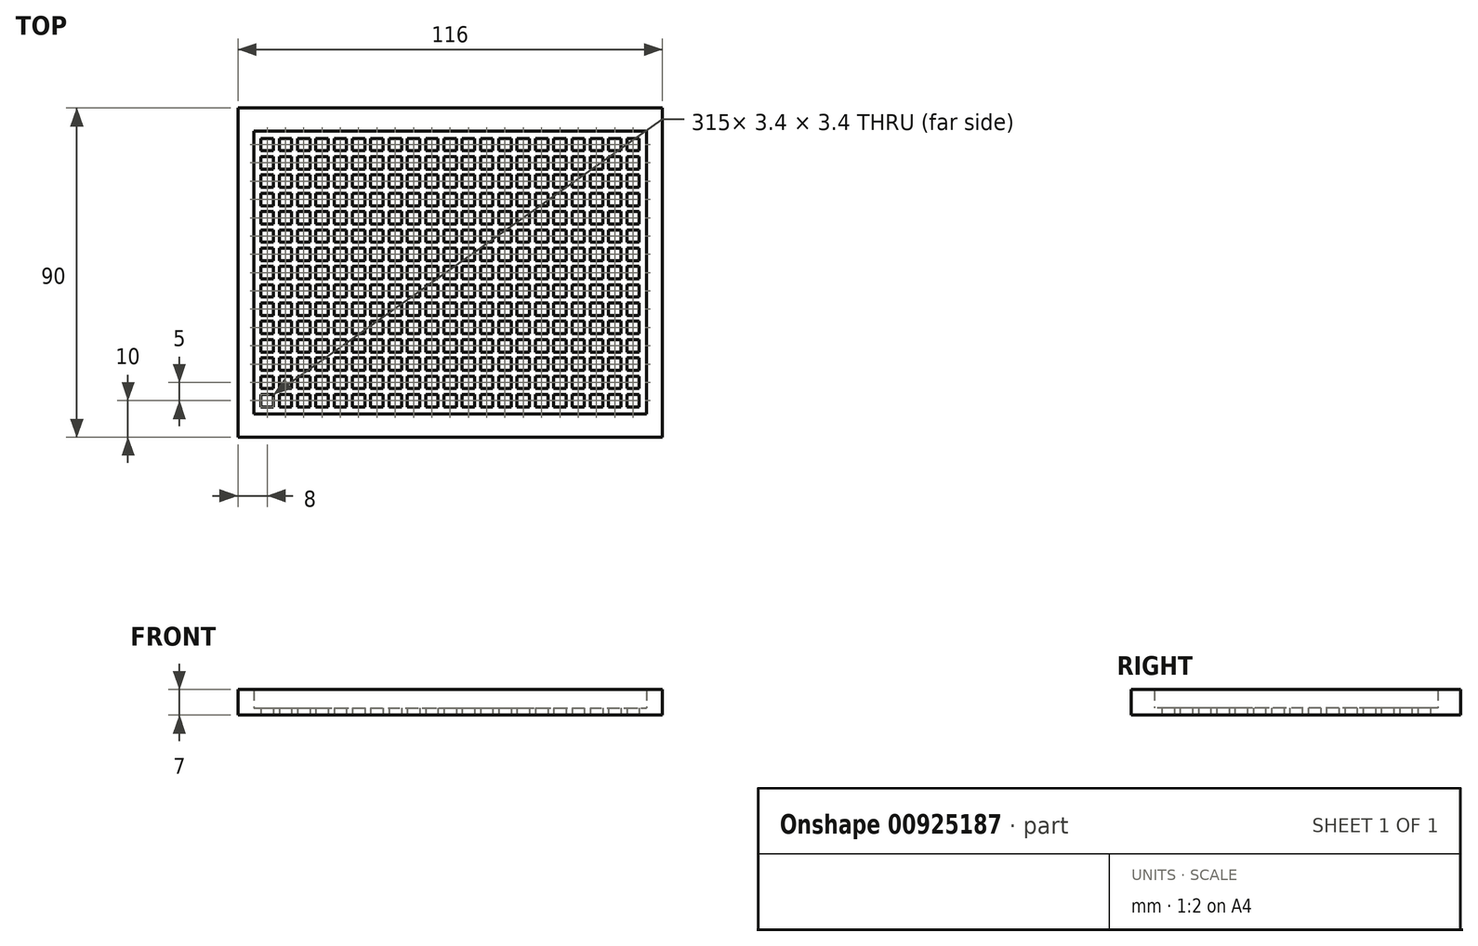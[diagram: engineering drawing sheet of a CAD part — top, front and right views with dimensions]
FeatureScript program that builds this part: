
annotation { "Feature Type Name" : "Feature", "Feature Type Description" : "" }
export const myFeature = defineFeature(function(context is Context, id is Id, definition is map)
    precondition{}
    {
        {
            var Q0;
            Q0=qCreatedBy(makeId("Top.planeOp"),FACE);
            var sketch = newSketch(context, id + "F0", { "sketchPlane" : qUnion([Q0])});
            skLineSegment(sketch, "E0.bottom", {"start": v(-58, 45) * mm, "end": v(58, 45) * mm});
            skLineSegment(sketch, "E0.top", {"start": v(-58, -45) * mm, "end": v(58, -45) * mm});
            skLineSegment(sketch, "E0.left", {"start": v(-58, 45) * mm, "end": v(-58, -45) * mm});
            skLineSegment(sketch, "E0.right", {"start": v(58, 45) * mm, "end": v(58, -45) * mm});
            skLineSegment(sketch, "E1.10.0.0", {"start": v(48.3, 1.7) * mm, "end": v(51.7, 1.7) * mm});
            skLineSegment(sketch, "E1.10.0.1", {"start": v(51.7, 1.7) * mm, "end": v(51.7, -1.7) * mm});
            skLineSegment(sketch, "E1.10.0.2", {"start": v(48.3, -1.7) * mm, "end": v(51.7, -1.7) * mm});
            skLineSegment(sketch, "E1.10.0.3", {"start": v(48.3, 1.7) * mm, "end": v(48.3, -1.7) * mm});
            skLineSegment(sketch, "E1.10.1.0", {"start": v(48.3, 6.7) * mm, "end": v(51.7, 6.7) * mm});
            skLineSegment(sketch, "E1.10.1.1", {"start": v(51.7, 6.7) * mm, "end": v(51.7, 3.3) * mm});
            skLineSegment(sketch, "E1.10.1.2", {"start": v(48.3, 3.3) * mm, "end": v(51.7, 3.3) * mm});
            skLineSegment(sketch, "E1.10.1.3", {"start": v(48.3, 6.7) * mm, "end": v(48.3, 3.3) * mm});
            skLineSegment(sketch, "E1.10.2.0", {"start": v(48.3, 11.7) * mm, "end": v(51.7, 11.7) * mm});
            skLineSegment(sketch, "E1.10.2.1", {"start": v(51.7, 11.7) * mm, "end": v(51.7, 8.3) * mm});
            skLineSegment(sketch, "E1.10.2.2", {"start": v(48.3, 8.3) * mm, "end": v(51.7, 8.3) * mm});
            skLineSegment(sketch, "E1.10.2.3", {"start": v(48.3, 11.7) * mm, "end": v(48.3, 8.3) * mm});
            skLineSegment(sketch, "E1.10.3.0", {"start": v(48.3, 16.7) * mm, "end": v(51.7, 16.7) * mm});
            skLineSegment(sketch, "E1.10.3.1", {"start": v(51.7, 16.7) * mm, "end": v(51.7, 13.3) * mm});
            skLineSegment(sketch, "E1.10.3.2", {"start": v(48.3, 13.3) * mm, "end": v(51.7, 13.3) * mm});
            skLineSegment(sketch, "E1.10.3.3", {"start": v(48.3, 16.7) * mm, "end": v(48.3, 13.3) * mm});
            skLineSegment(sketch, "E1.10.4.0", {"start": v(48.3, 21.7) * mm, "end": v(51.7, 21.7) * mm});
            skLineSegment(sketch, "E1.10.4.1", {"start": v(51.7, 21.7) * mm, "end": v(51.7, 18.3) * mm});
            skLineSegment(sketch, "E1.10.4.2", {"start": v(48.3, 18.3) * mm, "end": v(51.7, 18.3) * mm});
            skLineSegment(sketch, "E1.10.4.3", {"start": v(48.3, 21.7) * mm, "end": v(48.3, 18.3) * mm});
            skLineSegment(sketch, "E1.10.5.0", {"start": v(48.3, 26.7) * mm, "end": v(51.7, 26.7) * mm});
            skLineSegment(sketch, "E1.10.5.1", {"start": v(51.7, 26.7) * mm, "end": v(51.7, 23.3) * mm});
            skLineSegment(sketch, "E1.10.5.2", {"start": v(48.3, 23.3) * mm, "end": v(51.7, 23.3) * mm});
            skLineSegment(sketch, "E1.10.5.3", {"start": v(48.3, 26.7) * mm, "end": v(48.3, 23.3) * mm});
            skLineSegment(sketch, "E1.10.6.0", {"start": v(48.3, 31.7) * mm, "end": v(51.7, 31.7) * mm});
            skLineSegment(sketch, "E1.10.6.1", {"start": v(51.7, 31.7) * mm, "end": v(51.7, 28.3) * mm});
            skLineSegment(sketch, "E1.10.6.2", {"start": v(48.3, 28.3) * mm, "end": v(51.7, 28.3) * mm});
            skLineSegment(sketch, "E1.10.6.3", {"start": v(48.3, 31.7) * mm, "end": v(48.3, 28.3) * mm});
            skLineSegment(sketch, "E1.10.7.0", {"start": v(48.3, 36.7) * mm, "end": v(51.7, 36.7) * mm});
            skLineSegment(sketch, "E1.10.7.1", {"start": v(51.7, 36.7) * mm, "end": v(51.7, 33.3) * mm});
            skLineSegment(sketch, "E1.10.7.2", {"start": v(48.3, 33.3) * mm, "end": v(51.7, 33.3) * mm});
            skLineSegment(sketch, "E1.10.7.3", {"start": v(48.3, 36.7) * mm, "end": v(48.3, 33.3) * mm});
            skLineSegment(sketch, "E2.0.1.4", {"start": v(48.3, -3.3) * mm, "end": v(51.7, -3.3) * mm});
            skLineSegment(sketch, "E2.0.1.13", {"start": v(48.3, -3.3) * mm, "end": v(48.3, -6.7) * mm});
            skLineSegment(sketch, "E2.0.1.19", {"start": v(51.7, -3.3) * mm, "end": v(51.7, -6.7) * mm});
            skLineSegment(sketch, "E2.0.1.21", {"start": v(48.3, -6.7) * mm, "end": v(51.7, -6.7) * mm});
            skLineSegment(sketch, "E2.0.2.4", {"start": v(48.3, -8.3) * mm, "end": v(51.7, -8.3) * mm});
            skLineSegment(sketch, "E2.0.2.13", {"start": v(48.3, -8.3) * mm, "end": v(48.3, -11.7) * mm});
            skLineSegment(sketch, "E2.0.2.19", {"start": v(51.7, -8.3) * mm, "end": v(51.7, -11.7) * mm});
            skLineSegment(sketch, "E2.0.2.21", {"start": v(48.3, -11.7) * mm, "end": v(51.7, -11.7) * mm});
            skLineSegment(sketch, "E2.0.3.4", {"start": v(48.3, -13.3) * mm, "end": v(51.7, -13.3) * mm});
            skLineSegment(sketch, "E2.0.3.13", {"start": v(48.3, -13.3) * mm, "end": v(48.3, -16.7) * mm});
            skLineSegment(sketch, "E2.0.3.19", {"start": v(51.7, -13.3) * mm, "end": v(51.7, -16.7) * mm});
            skLineSegment(sketch, "E2.0.3.21", {"start": v(48.3, -16.7) * mm, "end": v(51.7, -16.7) * mm});
            skLineSegment(sketch, "E2.0.4.4", {"start": v(48.3, -18.3) * mm, "end": v(51.7, -18.3) * mm});
            skLineSegment(sketch, "E2.0.4.13", {"start": v(48.3, -18.3) * mm, "end": v(48.3, -21.7) * mm});
            skLineSegment(sketch, "E2.0.4.19", {"start": v(51.7, -18.3) * mm, "end": v(51.7, -21.7) * mm});
            skLineSegment(sketch, "E2.0.4.21", {"start": v(48.3, -21.7) * mm, "end": v(51.7, -21.7) * mm});
            skLineSegment(sketch, "E2.0.5.4", {"start": v(48.3, -23.3) * mm, "end": v(51.7, -23.3) * mm});
            skLineSegment(sketch, "E2.0.5.13", {"start": v(48.3, -23.3) * mm, "end": v(48.3, -26.7) * mm});
            skLineSegment(sketch, "E2.0.5.19", {"start": v(51.7, -23.3) * mm, "end": v(51.7, -26.7) * mm});
            skLineSegment(sketch, "E2.0.5.21", {"start": v(48.3, -26.7) * mm, "end": v(51.7, -26.7) * mm});
            skLineSegment(sketch, "E2.0.6.4", {"start": v(48.3, -28.3) * mm, "end": v(51.7, -28.3) * mm});
            skLineSegment(sketch, "E2.0.6.13", {"start": v(48.3, -28.3) * mm, "end": v(48.3, -31.7) * mm});
            skLineSegment(sketch, "E2.0.6.19", {"start": v(51.7, -28.3) * mm, "end": v(51.7, -31.7) * mm});
            skLineSegment(sketch, "E2.0.6.21", {"start": v(48.3, -31.7) * mm, "end": v(51.7, -31.7) * mm});
            skLineSegment(sketch, "E2.0.7.4", {"start": v(48.3, -33.3) * mm, "end": v(51.7, -33.3) * mm});
            skLineSegment(sketch, "E2.0.7.13", {"start": v(48.3, -33.3) * mm, "end": v(48.3, -36.7) * mm});
            skLineSegment(sketch, "E2.0.7.19", {"start": v(51.7, -33.3) * mm, "end": v(51.7, -36.7) * mm});
            skLineSegment(sketch, "E2.0.7.21", {"start": v(48.3, -36.7) * mm, "end": v(51.7, -36.7) * mm});
            skLineSegment(sketch, "E3.1.0.0", {"start": v(43.3, 36.7) * mm, "end": v(43.3, 33.3) * mm});
            skLineSegment(sketch, "E3.1.0.1", {"start": v(43.3, -21.7) * mm, "end": v(46.7, -21.7) * mm});
            skLineSegment(sketch, "E3.1.0.2", {"start": v(43.3, -3.3) * mm, "end": v(43.3, -6.7) * mm});
            skLineSegment(sketch, "E3.1.0.3", {"start": v(43.3, 8.3) * mm, "end": v(46.7, 8.3) * mm});
            skLineSegment(sketch, "E3.1.0.4", {"start": v(43.3, -33.3) * mm, "end": v(46.7, -33.3) * mm});
            skLineSegment(sketch, "E3.1.0.5", {"start": v(43.3, 31.7) * mm, "end": v(43.3, 28.3) * mm});
            skLineSegment(sketch, "E3.1.0.6", {"start": v(43.3, 1.7) * mm, "end": v(43.3, -1.7) * mm});
            skLineSegment(sketch, "E3.1.0.7", {"start": v(43.3, -18.3) * mm, "end": v(43.3, -21.7) * mm});
            skLineSegment(sketch, "E3.1.0.8", {"start": v(46.7, -33.3) * mm, "end": v(46.7, -36.7) * mm});
            skLineSegment(sketch, "E3.1.0.9", {"start": v(43.3, 16.7) * mm, "end": v(43.3, 13.3) * mm});
            skLineSegment(sketch, "E3.1.0.10", {"start": v(43.3, -8.3) * mm, "end": v(43.3, -11.7) * mm});
            skLineSegment(sketch, "E3.1.0.11", {"start": v(43.3, -36.7) * mm, "end": v(46.7, -36.7) * mm});
            skLineSegment(sketch, "E3.1.0.12", {"start": v(46.7, 26.7) * mm, "end": v(46.7, 23.3) * mm});
            skLineSegment(sketch, "E3.1.0.13", {"start": v(46.7, -28.3) * mm, "end": v(46.7, -31.7) * mm});
            skLineSegment(sketch, "E3.1.0.14", {"start": v(43.3, 23.3) * mm, "end": v(46.7, 23.3) * mm});
            skLineSegment(sketch, "E3.1.0.15", {"start": v(46.7, 6.7) * mm, "end": v(46.7, 3.3) * mm});
            skLineSegment(sketch, "E3.1.0.16", {"start": v(43.3, -28.3) * mm, "end": v(46.7, -28.3) * mm});
            skLineSegment(sketch, "E3.1.0.17", {"start": v(43.3, 13.3) * mm, "end": v(46.7, 13.3) * mm});
            skLineSegment(sketch, "E3.1.0.18", {"start": v(43.3, 33.3) * mm, "end": v(46.7, 33.3) * mm});
            skLineSegment(sketch, "E3.1.0.19", {"start": v(43.3, 3.3) * mm, "end": v(46.7, 3.3) * mm});
            skLineSegment(sketch, "E3.1.0.20", {"start": v(46.7, -13.3) * mm, "end": v(46.7, -16.7) * mm});
            skLineSegment(sketch, "E3.1.0.21", {"start": v(46.7, 16.7) * mm, "end": v(46.7, 13.3) * mm});
            skLineSegment(sketch, "E3.1.0.22", {"start": v(43.3, -23.3) * mm, "end": v(43.3, -26.7) * mm});
            skLineSegment(sketch, "E3.1.0.23", {"start": v(43.3, -28.3) * mm, "end": v(43.3, -31.7) * mm});
            skLineSegment(sketch, "E3.1.0.24", {"start": v(43.3, -13.3) * mm, "end": v(43.3, -16.7) * mm});
            skLineSegment(sketch, "E3.1.0.25", {"start": v(43.3, -23.3) * mm, "end": v(46.7, -23.3) * mm});
            skLineSegment(sketch, "E3.1.0.26", {"start": v(43.3, 1.7) * mm, "end": v(46.7, 1.7) * mm});
            skLineSegment(sketch, "E3.1.0.27", {"start": v(46.7, -3.3) * mm, "end": v(46.7, -6.7) * mm});
            skLineSegment(sketch, "E3.1.0.28", {"start": v(43.3, 28.3) * mm, "end": v(46.7, 28.3) * mm});
            skLineSegment(sketch, "E3.1.0.29", {"start": v(43.3, 21.7) * mm, "end": v(46.7, 21.7) * mm});
            skLineSegment(sketch, "E3.1.0.30", {"start": v(43.3, -18.3) * mm, "end": v(46.7, -18.3) * mm});
            skLineSegment(sketch, "E3.1.0.31", {"start": v(43.3, -13.3) * mm, "end": v(46.7, -13.3) * mm});
            skLineSegment(sketch, "E3.1.0.32", {"start": v(46.7, 1.7) * mm, "end": v(46.7, -1.7) * mm});
            skLineSegment(sketch, "E3.1.0.33", {"start": v(46.7, 36.7) * mm, "end": v(46.7, 33.3) * mm});
            skLineSegment(sketch, "E3.1.0.34", {"start": v(43.3, 18.3) * mm, "end": v(46.7, 18.3) * mm});
            skLineSegment(sketch, "E3.1.0.35", {"start": v(46.7, -18.3) * mm, "end": v(46.7, -21.7) * mm});
            skLineSegment(sketch, "E3.1.0.36", {"start": v(43.3, -33.3) * mm, "end": v(43.3, -36.7) * mm});
            skLineSegment(sketch, "E3.1.0.37", {"start": v(43.3, -3.3) * mm, "end": v(46.7, -3.3) * mm});
            skLineSegment(sketch, "E3.1.0.38", {"start": v(46.7, 21.7) * mm, "end": v(46.7, 18.3) * mm});
            skLineSegment(sketch, "E3.1.0.39", {"start": v(46.7, -8.3) * mm, "end": v(46.7, -11.7) * mm});
            skLineSegment(sketch, "E3.1.0.40", {"start": v(43.3, -16.7) * mm, "end": v(46.7, -16.7) * mm});
            skLineSegment(sketch, "E3.1.0.41", {"start": v(43.3, -31.7) * mm, "end": v(46.7, -31.7) * mm});
            skLineSegment(sketch, "E3.1.0.42", {"start": v(46.7, 31.7) * mm, "end": v(46.7, 28.3) * mm});
            skLineSegment(sketch, "E3.1.0.43", {"start": v(43.3, 26.7) * mm, "end": v(43.3, 23.3) * mm});
            skLineSegment(sketch, "E3.1.0.44", {"start": v(43.3, -1.7) * mm, "end": v(46.7, -1.7) * mm});
            skLineSegment(sketch, "E3.1.0.45", {"start": v(43.3, -26.7) * mm, "end": v(46.7, -26.7) * mm});
            skLineSegment(sketch, "E3.1.0.46", {"start": v(43.3, -8.3) * mm, "end": v(46.7, -8.3) * mm});
            skLineSegment(sketch, "E3.1.0.47", {"start": v(46.7, 11.7) * mm, "end": v(46.7, 8.3) * mm});
            skLineSegment(sketch, "E3.1.0.48", {"start": v(43.3, 6.7) * mm, "end": v(43.3, 3.3) * mm});
            skLineSegment(sketch, "E3.1.0.49", {"start": v(43.3, 16.7) * mm, "end": v(46.7, 16.7) * mm});
            skLineSegment(sketch, "E3.1.0.50", {"start": v(43.3, -11.7) * mm, "end": v(46.7, -11.7) * mm});
            skLineSegment(sketch, "E3.1.0.51", {"start": v(43.3, 6.7) * mm, "end": v(46.7, 6.7) * mm});
            skLineSegment(sketch, "E3.1.0.52", {"start": v(43.3, 11.7) * mm, "end": v(43.3, 8.3) * mm});
            skLineSegment(sketch, "E3.1.0.53", {"start": v(43.3, 11.7) * mm, "end": v(46.7, 11.7) * mm});
            skLineSegment(sketch, "E3.1.0.54", {"start": v(43.3, 36.7) * mm, "end": v(46.7, 36.7) * mm});
            skLineSegment(sketch, "E3.1.0.55", {"start": v(46.7, -23.3) * mm, "end": v(46.7, -26.7) * mm});
            skLineSegment(sketch, "E3.1.0.56", {"start": v(43.3, 26.7) * mm, "end": v(46.7, 26.7) * mm});
            skLineSegment(sketch, "E3.1.0.57", {"start": v(43.3, 31.7) * mm, "end": v(46.7, 31.7) * mm});
            skLineSegment(sketch, "E3.1.0.58", {"start": v(43.3, 21.7) * mm, "end": v(43.3, 18.3) * mm});
            skLineSegment(sketch, "E3.1.0.59", {"start": v(43.3, -6.7) * mm, "end": v(46.7, -6.7) * mm});
            skLineSegment(sketch, "E3.2.0.0", {"start": v(38.3, 36.7) * mm, "end": v(38.3, 33.3) * mm});
            skLineSegment(sketch, "E3.2.0.1", {"start": v(38.3, -21.7) * mm, "end": v(41.7, -21.7) * mm});
            skLineSegment(sketch, "E3.2.0.2", {"start": v(38.3, -3.3) * mm, "end": v(38.3, -6.7) * mm});
            skLineSegment(sketch, "E3.2.0.3", {"start": v(38.3, 8.3) * mm, "end": v(41.7, 8.3) * mm});
            skLineSegment(sketch, "E3.2.0.4", {"start": v(38.3, -33.3) * mm, "end": v(41.7, -33.3) * mm});
            skLineSegment(sketch, "E3.2.0.5", {"start": v(38.3, 31.7) * mm, "end": v(38.3, 28.3) * mm});
            skLineSegment(sketch, "E3.2.0.6", {"start": v(38.3, 1.7) * mm, "end": v(38.3, -1.7) * mm});
            skLineSegment(sketch, "E3.2.0.7", {"start": v(38.3, -18.3) * mm, "end": v(38.3, -21.7) * mm});
            skLineSegment(sketch, "E3.2.0.8", {"start": v(41.7, -33.3) * mm, "end": v(41.7, -36.7) * mm});
            skLineSegment(sketch, "E3.2.0.9", {"start": v(38.3, 16.7) * mm, "end": v(38.3, 13.3) * mm});
            skLineSegment(sketch, "E3.2.0.10", {"start": v(38.3, -8.3) * mm, "end": v(38.3, -11.7) * mm});
            skLineSegment(sketch, "E3.2.0.11", {"start": v(38.3, -36.7) * mm, "end": v(41.7, -36.7) * mm});
            skLineSegment(sketch, "E3.2.0.12", {"start": v(41.7, 26.7) * mm, "end": v(41.7, 23.3) * mm});
            skLineSegment(sketch, "E3.2.0.13", {"start": v(41.7, -28.3) * mm, "end": v(41.7, -31.7) * mm});
            skLineSegment(sketch, "E3.2.0.14", {"start": v(38.3, 23.3) * mm, "end": v(41.7, 23.3) * mm});
            skLineSegment(sketch, "E3.2.0.15", {"start": v(41.7, 6.7) * mm, "end": v(41.7, 3.3) * mm});
            skLineSegment(sketch, "E3.2.0.16", {"start": v(38.3, -28.3) * mm, "end": v(41.7, -28.3) * mm});
            skLineSegment(sketch, "E3.2.0.17", {"start": v(38.3, 13.3) * mm, "end": v(41.7, 13.3) * mm});
            skLineSegment(sketch, "E3.2.0.18", {"start": v(38.3, 33.3) * mm, "end": v(41.7, 33.3) * mm});
            skLineSegment(sketch, "E3.2.0.19", {"start": v(38.3, 3.3) * mm, "end": v(41.7, 3.3) * mm});
            skLineSegment(sketch, "E3.2.0.20", {"start": v(41.7, -13.3) * mm, "end": v(41.7, -16.7) * mm});
            skLineSegment(sketch, "E3.2.0.21", {"start": v(41.7, 16.7) * mm, "end": v(41.7, 13.3) * mm});
            skLineSegment(sketch, "E3.2.0.22", {"start": v(38.3, -23.3) * mm, "end": v(38.3, -26.7) * mm});
            skLineSegment(sketch, "E3.2.0.23", {"start": v(38.3, -28.3) * mm, "end": v(38.3, -31.7) * mm});
            skLineSegment(sketch, "E3.2.0.24", {"start": v(38.3, -13.3) * mm, "end": v(38.3, -16.7) * mm});
            skLineSegment(sketch, "E3.2.0.25", {"start": v(38.3, -23.3) * mm, "end": v(41.7, -23.3) * mm});
            skLineSegment(sketch, "E3.2.0.26", {"start": v(38.3, 1.7) * mm, "end": v(41.7, 1.7) * mm});
            skLineSegment(sketch, "E3.2.0.27", {"start": v(41.7, -3.3) * mm, "end": v(41.7, -6.7) * mm});
            skLineSegment(sketch, "E3.2.0.28", {"start": v(38.3, 28.3) * mm, "end": v(41.7, 28.3) * mm});
            skLineSegment(sketch, "E3.2.0.29", {"start": v(38.3, 21.7) * mm, "end": v(41.7, 21.7) * mm});
            skLineSegment(sketch, "E3.2.0.30", {"start": v(38.3, -18.3) * mm, "end": v(41.7, -18.3) * mm});
            skLineSegment(sketch, "E3.2.0.31", {"start": v(38.3, -13.3) * mm, "end": v(41.7, -13.3) * mm});
            skLineSegment(sketch, "E3.2.0.32", {"start": v(41.7, 1.7) * mm, "end": v(41.7, -1.7) * mm});
            skLineSegment(sketch, "E3.2.0.33", {"start": v(41.7, 36.7) * mm, "end": v(41.7, 33.3) * mm});
            skLineSegment(sketch, "E3.2.0.34", {"start": v(38.3, 18.3) * mm, "end": v(41.7, 18.3) * mm});
            skLineSegment(sketch, "E3.2.0.35", {"start": v(41.7, -18.3) * mm, "end": v(41.7, -21.7) * mm});
            skLineSegment(sketch, "E3.2.0.36", {"start": v(38.3, -33.3) * mm, "end": v(38.3, -36.7) * mm});
            skLineSegment(sketch, "E3.2.0.37", {"start": v(38.3, -3.3) * mm, "end": v(41.7, -3.3) * mm});
            skLineSegment(sketch, "E3.2.0.38", {"start": v(41.7, 21.7) * mm, "end": v(41.7, 18.3) * mm});
            skLineSegment(sketch, "E3.2.0.39", {"start": v(41.7, -8.3) * mm, "end": v(41.7, -11.7) * mm});
            skLineSegment(sketch, "E3.2.0.40", {"start": v(38.3, -16.7) * mm, "end": v(41.7, -16.7) * mm});
            skLineSegment(sketch, "E3.2.0.41", {"start": v(38.3, -31.7) * mm, "end": v(41.7, -31.7) * mm});
            skLineSegment(sketch, "E3.2.0.42", {"start": v(41.7, 31.7) * mm, "end": v(41.7, 28.3) * mm});
            skLineSegment(sketch, "E3.2.0.43", {"start": v(38.3, 26.7) * mm, "end": v(38.3, 23.3) * mm});
            skLineSegment(sketch, "E3.2.0.44", {"start": v(38.3, -1.7) * mm, "end": v(41.7, -1.7) * mm});
            skLineSegment(sketch, "E3.2.0.45", {"start": v(38.3, -26.7) * mm, "end": v(41.7, -26.7) * mm});
            skLineSegment(sketch, "E3.2.0.46", {"start": v(38.3, -8.3) * mm, "end": v(41.7, -8.3) * mm});
            skLineSegment(sketch, "E3.2.0.47", {"start": v(41.7, 11.7) * mm, "end": v(41.7, 8.3) * mm});
            skLineSegment(sketch, "E3.2.0.48", {"start": v(38.3, 6.7) * mm, "end": v(38.3, 3.3) * mm});
            skLineSegment(sketch, "E3.2.0.49", {"start": v(38.3, 16.7) * mm, "end": v(41.7, 16.7) * mm});
            skLineSegment(sketch, "E3.2.0.50", {"start": v(38.3, -11.7) * mm, "end": v(41.7, -11.7) * mm});
            skLineSegment(sketch, "E3.2.0.51", {"start": v(38.3, 6.7) * mm, "end": v(41.7, 6.7) * mm});
            skLineSegment(sketch, "E3.2.0.52", {"start": v(38.3, 11.7) * mm, "end": v(38.3, 8.3) * mm});
            skLineSegment(sketch, "E3.2.0.53", {"start": v(38.3, 11.7) * mm, "end": v(41.7, 11.7) * mm});
            skLineSegment(sketch, "E3.2.0.54", {"start": v(38.3, 36.7) * mm, "end": v(41.7, 36.7) * mm});
            skLineSegment(sketch, "E3.2.0.55", {"start": v(41.7, -23.3) * mm, "end": v(41.7, -26.7) * mm});
            skLineSegment(sketch, "E3.2.0.56", {"start": v(38.3, 26.7) * mm, "end": v(41.7, 26.7) * mm});
            skLineSegment(sketch, "E3.2.0.57", {"start": v(38.3, 31.7) * mm, "end": v(41.7, 31.7) * mm});
            skLineSegment(sketch, "E3.2.0.58", {"start": v(38.3, 21.7) * mm, "end": v(38.3, 18.3) * mm});
            skLineSegment(sketch, "E3.2.0.59", {"start": v(38.3, -6.7) * mm, "end": v(41.7, -6.7) * mm});
            skLineSegment(sketch, "E3.3.0.0", {"start": v(33.3, 36.7) * mm, "end": v(33.3, 33.3) * mm});
            skLineSegment(sketch, "E3.3.0.1", {"start": v(33.3, -21.7) * mm, "end": v(36.7, -21.7) * mm});
            skLineSegment(sketch, "E3.3.0.2", {"start": v(33.3, -3.3) * mm, "end": v(33.3, -6.7) * mm});
            skLineSegment(sketch, "E3.3.0.3", {"start": v(33.3, 8.3) * mm, "end": v(36.7, 8.3) * mm});
            skLineSegment(sketch, "E3.3.0.4", {"start": v(33.3, -33.3) * mm, "end": v(36.7, -33.3) * mm});
            skLineSegment(sketch, "E3.3.0.5", {"start": v(33.3, 31.7) * mm, "end": v(33.3, 28.3) * mm});
            skLineSegment(sketch, "E3.3.0.6", {"start": v(33.3, 1.7) * mm, "end": v(33.3, -1.7) * mm});
            skLineSegment(sketch, "E3.3.0.7", {"start": v(33.3, -18.3) * mm, "end": v(33.3, -21.7) * mm});
            skLineSegment(sketch, "E3.3.0.8", {"start": v(36.7, -33.3) * mm, "end": v(36.7, -36.7) * mm});
            skLineSegment(sketch, "E3.3.0.9", {"start": v(33.3, 16.7) * mm, "end": v(33.3, 13.3) * mm});
            skLineSegment(sketch, "E3.3.0.10", {"start": v(33.3, -8.3) * mm, "end": v(33.3, -11.7) * mm});
            skLineSegment(sketch, "E3.3.0.11", {"start": v(33.3, -36.7) * mm, "end": v(36.7, -36.7) * mm});
            skLineSegment(sketch, "E3.3.0.12", {"start": v(36.7, 26.7) * mm, "end": v(36.7, 23.3) * mm});
            skLineSegment(sketch, "E3.3.0.13", {"start": v(36.7, -28.3) * mm, "end": v(36.7, -31.7) * mm});
            skLineSegment(sketch, "E3.3.0.14", {"start": v(33.3, 23.3) * mm, "end": v(36.7, 23.3) * mm});
            skLineSegment(sketch, "E3.3.0.15", {"start": v(36.7, 6.7) * mm, "end": v(36.7, 3.3) * mm});
            skLineSegment(sketch, "E3.3.0.16", {"start": v(33.3, -28.3) * mm, "end": v(36.7, -28.3) * mm});
            skLineSegment(sketch, "E3.3.0.17", {"start": v(33.3, 13.3) * mm, "end": v(36.7, 13.3) * mm});
            skLineSegment(sketch, "E3.3.0.18", {"start": v(33.3, 33.3) * mm, "end": v(36.7, 33.3) * mm});
            skLineSegment(sketch, "E3.3.0.19", {"start": v(33.3, 3.3) * mm, "end": v(36.7, 3.3) * mm});
            skLineSegment(sketch, "E3.3.0.20", {"start": v(36.7, -13.3) * mm, "end": v(36.7, -16.7) * mm});
            skLineSegment(sketch, "E3.3.0.21", {"start": v(36.7, 16.7) * mm, "end": v(36.7, 13.3) * mm});
            skLineSegment(sketch, "E3.3.0.22", {"start": v(33.3, -23.3) * mm, "end": v(33.3, -26.7) * mm});
            skLineSegment(sketch, "E3.3.0.23", {"start": v(33.3, -28.3) * mm, "end": v(33.3, -31.7) * mm});
            skLineSegment(sketch, "E3.3.0.24", {"start": v(33.3, -13.3) * mm, "end": v(33.3, -16.7) * mm});
            skLineSegment(sketch, "E3.3.0.25", {"start": v(33.3, -23.3) * mm, "end": v(36.7, -23.3) * mm});
            skLineSegment(sketch, "E3.3.0.26", {"start": v(33.3, 1.7) * mm, "end": v(36.7, 1.7) * mm});
            skLineSegment(sketch, "E3.3.0.27", {"start": v(36.7, -3.3) * mm, "end": v(36.7, -6.7) * mm});
            skLineSegment(sketch, "E3.3.0.28", {"start": v(33.3, 28.3) * mm, "end": v(36.7, 28.3) * mm});
            skLineSegment(sketch, "E3.3.0.29", {"start": v(33.3, 21.7) * mm, "end": v(36.7, 21.7) * mm});
            skLineSegment(sketch, "E3.3.0.30", {"start": v(33.3, -18.3) * mm, "end": v(36.7, -18.3) * mm});
            skLineSegment(sketch, "E3.3.0.31", {"start": v(33.3, -13.3) * mm, "end": v(36.7, -13.3) * mm});
            skLineSegment(sketch, "E3.3.0.32", {"start": v(36.7, 1.7) * mm, "end": v(36.7, -1.7) * mm});
            skLineSegment(sketch, "E3.3.0.33", {"start": v(36.7, 36.7) * mm, "end": v(36.7, 33.3) * mm});
            skLineSegment(sketch, "E3.3.0.34", {"start": v(33.3, 18.3) * mm, "end": v(36.7, 18.3) * mm});
            skLineSegment(sketch, "E3.3.0.35", {"start": v(36.7, -18.3) * mm, "end": v(36.7, -21.7) * mm});
            skLineSegment(sketch, "E3.3.0.36", {"start": v(33.3, -33.3) * mm, "end": v(33.3, -36.7) * mm});
            skLineSegment(sketch, "E3.3.0.37", {"start": v(33.3, -3.3) * mm, "end": v(36.7, -3.3) * mm});
            skLineSegment(sketch, "E3.3.0.38", {"start": v(36.7, 21.7) * mm, "end": v(36.7, 18.3) * mm});
            skLineSegment(sketch, "E3.3.0.39", {"start": v(36.7, -8.3) * mm, "end": v(36.7, -11.7) * mm});
            skLineSegment(sketch, "E3.3.0.40", {"start": v(33.3, -16.7) * mm, "end": v(36.7, -16.7) * mm});
            skLineSegment(sketch, "E3.3.0.41", {"start": v(33.3, -31.7) * mm, "end": v(36.7, -31.7) * mm});
            skLineSegment(sketch, "E3.3.0.42", {"start": v(36.7, 31.7) * mm, "end": v(36.7, 28.3) * mm});
            skLineSegment(sketch, "E3.3.0.43", {"start": v(33.3, 26.7) * mm, "end": v(33.3, 23.3) * mm});
            skLineSegment(sketch, "E3.3.0.44", {"start": v(33.3, -1.7) * mm, "end": v(36.7, -1.7) * mm});
            skLineSegment(sketch, "E3.3.0.45", {"start": v(33.3, -26.7) * mm, "end": v(36.7, -26.7) * mm});
            skLineSegment(sketch, "E3.3.0.46", {"start": v(33.3, -8.3) * mm, "end": v(36.7, -8.3) * mm});
            skLineSegment(sketch, "E3.3.0.47", {"start": v(36.7, 11.7) * mm, "end": v(36.7, 8.3) * mm});
            skLineSegment(sketch, "E3.3.0.48", {"start": v(33.3, 6.7) * mm, "end": v(33.3, 3.3) * mm});
            skLineSegment(sketch, "E3.3.0.49", {"start": v(33.3, 16.7) * mm, "end": v(36.7, 16.7) * mm});
            skLineSegment(sketch, "E3.3.0.50", {"start": v(33.3, -11.7) * mm, "end": v(36.7, -11.7) * mm});
            skLineSegment(sketch, "E3.3.0.51", {"start": v(33.3, 6.7) * mm, "end": v(36.7, 6.7) * mm});
            skLineSegment(sketch, "E3.3.0.52", {"start": v(33.3, 11.7) * mm, "end": v(33.3, 8.3) * mm});
            skLineSegment(sketch, "E3.3.0.53", {"start": v(33.3, 11.7) * mm, "end": v(36.7, 11.7) * mm});
            skLineSegment(sketch, "E3.3.0.54", {"start": v(33.3, 36.7) * mm, "end": v(36.7, 36.7) * mm});
            skLineSegment(sketch, "E3.3.0.55", {"start": v(36.7, -23.3) * mm, "end": v(36.7, -26.7) * mm});
            skLineSegment(sketch, "E3.3.0.56", {"start": v(33.3, 26.7) * mm, "end": v(36.7, 26.7) * mm});
            skLineSegment(sketch, "E3.3.0.57", {"start": v(33.3, 31.7) * mm, "end": v(36.7, 31.7) * mm});
            skLineSegment(sketch, "E3.3.0.58", {"start": v(33.3, 21.7) * mm, "end": v(33.3, 18.3) * mm});
            skLineSegment(sketch, "E3.3.0.59", {"start": v(33.3, -6.7) * mm, "end": v(36.7, -6.7) * mm});
            skLineSegment(sketch, "E3.4.0.0", {"start": v(28.3, 36.7) * mm, "end": v(28.3, 33.3) * mm});
            skLineSegment(sketch, "E3.4.0.1", {"start": v(28.3, -21.7) * mm, "end": v(31.7, -21.7) * mm});
            skLineSegment(sketch, "E3.4.0.2", {"start": v(28.3, -3.3) * mm, "end": v(28.3, -6.7) * mm});
            skLineSegment(sketch, "E3.4.0.3", {"start": v(28.3, 8.3) * mm, "end": v(31.7, 8.3) * mm});
            skLineSegment(sketch, "E3.4.0.4", {"start": v(28.3, -33.3) * mm, "end": v(31.7, -33.3) * mm});
            skLineSegment(sketch, "E3.4.0.5", {"start": v(28.3, 31.7) * mm, "end": v(28.3, 28.3) * mm});
            skLineSegment(sketch, "E3.4.0.6", {"start": v(28.3, 1.7) * mm, "end": v(28.3, -1.7) * mm});
            skLineSegment(sketch, "E3.4.0.7", {"start": v(28.3, -18.3) * mm, "end": v(28.3, -21.7) * mm});
            skLineSegment(sketch, "E3.4.0.8", {"start": v(31.7, -33.3) * mm, "end": v(31.7, -36.7) * mm});
            skLineSegment(sketch, "E3.4.0.9", {"start": v(28.3, 16.7) * mm, "end": v(28.3, 13.3) * mm});
            skLineSegment(sketch, "E3.4.0.10", {"start": v(28.3, -8.3) * mm, "end": v(28.3, -11.7) * mm});
            skLineSegment(sketch, "E3.4.0.11", {"start": v(28.3, -36.7) * mm, "end": v(31.7, -36.7) * mm});
            skLineSegment(sketch, "E3.4.0.12", {"start": v(31.7, 26.7) * mm, "end": v(31.7, 23.3) * mm});
            skLineSegment(sketch, "E3.4.0.13", {"start": v(31.7, -28.3) * mm, "end": v(31.7, -31.7) * mm});
            skLineSegment(sketch, "E3.4.0.14", {"start": v(28.3, 23.3) * mm, "end": v(31.7, 23.3) * mm});
            skLineSegment(sketch, "E3.4.0.15", {"start": v(31.7, 6.7) * mm, "end": v(31.7, 3.3) * mm});
            skLineSegment(sketch, "E3.4.0.16", {"start": v(28.3, -28.3) * mm, "end": v(31.7, -28.3) * mm});
            skLineSegment(sketch, "E3.4.0.17", {"start": v(28.3, 13.3) * mm, "end": v(31.7, 13.3) * mm});
            skLineSegment(sketch, "E3.4.0.18", {"start": v(28.3, 33.3) * mm, "end": v(31.7, 33.3) * mm});
            skLineSegment(sketch, "E3.4.0.19", {"start": v(28.3, 3.3) * mm, "end": v(31.7, 3.3) * mm});
            skLineSegment(sketch, "E3.4.0.20", {"start": v(31.7, -13.3) * mm, "end": v(31.7, -16.7) * mm});
            skLineSegment(sketch, "E3.4.0.21", {"start": v(31.7, 16.7) * mm, "end": v(31.7, 13.3) * mm});
            skLineSegment(sketch, "E3.4.0.22", {"start": v(28.3, -23.3) * mm, "end": v(28.3, -26.7) * mm});
            skLineSegment(sketch, "E3.4.0.23", {"start": v(28.3, -28.3) * mm, "end": v(28.3, -31.7) * mm});
            skLineSegment(sketch, "E3.4.0.24", {"start": v(28.3, -13.3) * mm, "end": v(28.3, -16.7) * mm});
            skLineSegment(sketch, "E3.4.0.25", {"start": v(28.3, -23.3) * mm, "end": v(31.7, -23.3) * mm});
            skLineSegment(sketch, "E3.4.0.26", {"start": v(28.3, 1.7) * mm, "end": v(31.7, 1.7) * mm});
            skLineSegment(sketch, "E3.4.0.27", {"start": v(31.7, -3.3) * mm, "end": v(31.7, -6.7) * mm});
            skLineSegment(sketch, "E3.4.0.28", {"start": v(28.3, 28.3) * mm, "end": v(31.7, 28.3) * mm});
            skLineSegment(sketch, "E3.4.0.29", {"start": v(28.3, 21.7) * mm, "end": v(31.7, 21.7) * mm});
            skLineSegment(sketch, "E3.4.0.30", {"start": v(28.3, -18.3) * mm, "end": v(31.7, -18.3) * mm});
            skLineSegment(sketch, "E3.4.0.31", {"start": v(28.3, -13.3) * mm, "end": v(31.7, -13.3) * mm});
            skLineSegment(sketch, "E3.4.0.32", {"start": v(31.7, 1.7) * mm, "end": v(31.7, -1.7) * mm});
            skLineSegment(sketch, "E3.4.0.33", {"start": v(31.7, 36.7) * mm, "end": v(31.7, 33.3) * mm});
            skLineSegment(sketch, "E3.4.0.34", {"start": v(28.3, 18.3) * mm, "end": v(31.7, 18.3) * mm});
            skLineSegment(sketch, "E3.4.0.35", {"start": v(31.7, -18.3) * mm, "end": v(31.7, -21.7) * mm});
            skLineSegment(sketch, "E3.4.0.36", {"start": v(28.3, -33.3) * mm, "end": v(28.3, -36.7) * mm});
            skLineSegment(sketch, "E3.4.0.37", {"start": v(28.3, -3.3) * mm, "end": v(31.7, -3.3) * mm});
            skLineSegment(sketch, "E3.4.0.38", {"start": v(31.7, 21.7) * mm, "end": v(31.7, 18.3) * mm});
            skLineSegment(sketch, "E3.4.0.39", {"start": v(31.7, -8.3) * mm, "end": v(31.7, -11.7) * mm});
            skLineSegment(sketch, "E3.4.0.40", {"start": v(28.3, -16.7) * mm, "end": v(31.7, -16.7) * mm});
            skLineSegment(sketch, "E3.4.0.41", {"start": v(28.3, -31.7) * mm, "end": v(31.7, -31.7) * mm});
            skLineSegment(sketch, "E3.4.0.42", {"start": v(31.7, 31.7) * mm, "end": v(31.7, 28.3) * mm});
            skLineSegment(sketch, "E3.4.0.43", {"start": v(28.3, 26.7) * mm, "end": v(28.3, 23.3) * mm});
            skLineSegment(sketch, "E3.4.0.44", {"start": v(28.3, -1.7) * mm, "end": v(31.7, -1.7) * mm});
            skLineSegment(sketch, "E3.4.0.45", {"start": v(28.3, -26.7) * mm, "end": v(31.7, -26.7) * mm});
            skLineSegment(sketch, "E3.4.0.46", {"start": v(28.3, -8.3) * mm, "end": v(31.7, -8.3) * mm});
            skLineSegment(sketch, "E3.4.0.47", {"start": v(31.7, 11.7) * mm, "end": v(31.7, 8.3) * mm});
            skLineSegment(sketch, "E3.4.0.48", {"start": v(28.3, 6.7) * mm, "end": v(28.3, 3.3) * mm});
            skLineSegment(sketch, "E3.4.0.49", {"start": v(28.3, 16.7) * mm, "end": v(31.7, 16.7) * mm});
            skLineSegment(sketch, "E3.4.0.50", {"start": v(28.3, -11.7) * mm, "end": v(31.7, -11.7) * mm});
            skLineSegment(sketch, "E3.4.0.51", {"start": v(28.3, 6.7) * mm, "end": v(31.7, 6.7) * mm});
            skLineSegment(sketch, "E3.4.0.52", {"start": v(28.3, 11.7) * mm, "end": v(28.3, 8.3) * mm});
            skLineSegment(sketch, "E3.4.0.53", {"start": v(28.3, 11.7) * mm, "end": v(31.7, 11.7) * mm});
            skLineSegment(sketch, "E3.4.0.54", {"start": v(28.3, 36.7) * mm, "end": v(31.7, 36.7) * mm});
            skLineSegment(sketch, "E3.4.0.55", {"start": v(31.7, -23.3) * mm, "end": v(31.7, -26.7) * mm});
            skLineSegment(sketch, "E3.4.0.56", {"start": v(28.3, 26.7) * mm, "end": v(31.7, 26.7) * mm});
            skLineSegment(sketch, "E3.4.0.57", {"start": v(28.3, 31.7) * mm, "end": v(31.7, 31.7) * mm});
            skLineSegment(sketch, "E3.4.0.58", {"start": v(28.3, 21.7) * mm, "end": v(28.3, 18.3) * mm});
            skLineSegment(sketch, "E3.4.0.59", {"start": v(28.3, -6.7) * mm, "end": v(31.7, -6.7) * mm});
            skLineSegment(sketch, "E3.5.0.0", {"start": v(23.3, 36.7) * mm, "end": v(23.3, 33.3) * mm});
            skLineSegment(sketch, "E3.5.0.1", {"start": v(23.3, -21.7) * mm, "end": v(26.7, -21.7) * mm});
            skLineSegment(sketch, "E3.5.0.2", {"start": v(23.3, -3.3) * mm, "end": v(23.3, -6.7) * mm});
            skLineSegment(sketch, "E3.5.0.3", {"start": v(23.3, 8.3) * mm, "end": v(26.7, 8.3) * mm});
            skLineSegment(sketch, "E3.5.0.4", {"start": v(23.3, -33.3) * mm, "end": v(26.7, -33.3) * mm});
            skLineSegment(sketch, "E3.5.0.5", {"start": v(23.3, 31.7) * mm, "end": v(23.3, 28.3) * mm});
            skLineSegment(sketch, "E3.5.0.6", {"start": v(23.3, 1.7) * mm, "end": v(23.3, -1.7) * mm});
            skLineSegment(sketch, "E3.5.0.7", {"start": v(23.3, -18.3) * mm, "end": v(23.3, -21.7) * mm});
            skLineSegment(sketch, "E3.5.0.8", {"start": v(26.7, -33.3) * mm, "end": v(26.7, -36.7) * mm});
            skLineSegment(sketch, "E3.5.0.9", {"start": v(23.3, 16.7) * mm, "end": v(23.3, 13.3) * mm});
            skLineSegment(sketch, "E3.5.0.10", {"start": v(23.3, -8.3) * mm, "end": v(23.3, -11.7) * mm});
            skLineSegment(sketch, "E3.5.0.11", {"start": v(23.3, -36.7) * mm, "end": v(26.7, -36.7) * mm});
            skLineSegment(sketch, "E3.5.0.12", {"start": v(26.7, 26.7) * mm, "end": v(26.7, 23.3) * mm});
            skLineSegment(sketch, "E3.5.0.13", {"start": v(26.7, -28.3) * mm, "end": v(26.7, -31.7) * mm});
            skLineSegment(sketch, "E3.5.0.14", {"start": v(23.3, 23.3) * mm, "end": v(26.7, 23.3) * mm});
            skLineSegment(sketch, "E3.5.0.15", {"start": v(26.7, 6.7) * mm, "end": v(26.7, 3.3) * mm});
            skLineSegment(sketch, "E3.5.0.16", {"start": v(23.3, -28.3) * mm, "end": v(26.7, -28.3) * mm});
            skLineSegment(sketch, "E3.5.0.17", {"start": v(23.3, 13.3) * mm, "end": v(26.7, 13.3) * mm});
            skLineSegment(sketch, "E3.5.0.18", {"start": v(23.3, 33.3) * mm, "end": v(26.7, 33.3) * mm});
            skLineSegment(sketch, "E3.5.0.19", {"start": v(23.3, 3.3) * mm, "end": v(26.7, 3.3) * mm});
            skLineSegment(sketch, "E3.5.0.20", {"start": v(26.7, -13.3) * mm, "end": v(26.7, -16.7) * mm});
            skLineSegment(sketch, "E3.5.0.21", {"start": v(26.7, 16.7) * mm, "end": v(26.7, 13.3) * mm});
            skLineSegment(sketch, "E3.5.0.22", {"start": v(23.3, -23.3) * mm, "end": v(23.3, -26.7) * mm});
            skLineSegment(sketch, "E3.5.0.23", {"start": v(23.3, -28.3) * mm, "end": v(23.3, -31.7) * mm});
            skLineSegment(sketch, "E3.5.0.24", {"start": v(23.3, -13.3) * mm, "end": v(23.3, -16.7) * mm});
            skLineSegment(sketch, "E3.5.0.25", {"start": v(23.3, -23.3) * mm, "end": v(26.7, -23.3) * mm});
            skLineSegment(sketch, "E3.5.0.26", {"start": v(23.3, 1.7) * mm, "end": v(26.7, 1.7) * mm});
            skLineSegment(sketch, "E3.5.0.27", {"start": v(26.7, -3.3) * mm, "end": v(26.7, -6.7) * mm});
            skLineSegment(sketch, "E3.5.0.28", {"start": v(23.3, 28.3) * mm, "end": v(26.7, 28.3) * mm});
            skLineSegment(sketch, "E3.5.0.29", {"start": v(23.3, 21.7) * mm, "end": v(26.7, 21.7) * mm});
            skLineSegment(sketch, "E3.5.0.30", {"start": v(23.3, -18.3) * mm, "end": v(26.7, -18.3) * mm});
            skLineSegment(sketch, "E3.5.0.31", {"start": v(23.3, -13.3) * mm, "end": v(26.7, -13.3) * mm});
            skLineSegment(sketch, "E3.5.0.32", {"start": v(26.7, 1.7) * mm, "end": v(26.7, -1.7) * mm});
            skLineSegment(sketch, "E3.5.0.33", {"start": v(26.7, 36.7) * mm, "end": v(26.7, 33.3) * mm});
            skLineSegment(sketch, "E3.5.0.34", {"start": v(23.3, 18.3) * mm, "end": v(26.7, 18.3) * mm});
            skLineSegment(sketch, "E3.5.0.35", {"start": v(26.7, -18.3) * mm, "end": v(26.7, -21.7) * mm});
            skLineSegment(sketch, "E3.5.0.36", {"start": v(23.3, -33.3) * mm, "end": v(23.3, -36.7) * mm});
            skLineSegment(sketch, "E3.5.0.37", {"start": v(23.3, -3.3) * mm, "end": v(26.7, -3.3) * mm});
            skLineSegment(sketch, "E3.5.0.38", {"start": v(26.7, 21.7) * mm, "end": v(26.7, 18.3) * mm});
            skLineSegment(sketch, "E3.5.0.39", {"start": v(26.7, -8.3) * mm, "end": v(26.7, -11.7) * mm});
            skLineSegment(sketch, "E3.5.0.40", {"start": v(23.3, -16.7) * mm, "end": v(26.7, -16.7) * mm});
            skLineSegment(sketch, "E3.5.0.41", {"start": v(23.3, -31.7) * mm, "end": v(26.7, -31.7) * mm});
            skLineSegment(sketch, "E3.5.0.42", {"start": v(26.7, 31.7) * mm, "end": v(26.7, 28.3) * mm});
            skLineSegment(sketch, "E3.5.0.43", {"start": v(23.3, 26.7) * mm, "end": v(23.3, 23.3) * mm});
            skLineSegment(sketch, "E3.5.0.44", {"start": v(23.3, -1.7) * mm, "end": v(26.7, -1.7) * mm});
            skLineSegment(sketch, "E3.5.0.45", {"start": v(23.3, -26.7) * mm, "end": v(26.7, -26.7) * mm});
            skLineSegment(sketch, "E3.5.0.46", {"start": v(23.3, -8.3) * mm, "end": v(26.7, -8.3) * mm});
            skLineSegment(sketch, "E3.5.0.47", {"start": v(26.7, 11.7) * mm, "end": v(26.7, 8.3) * mm});
            skLineSegment(sketch, "E3.5.0.48", {"start": v(23.3, 6.7) * mm, "end": v(23.3, 3.3) * mm});
            skLineSegment(sketch, "E3.5.0.49", {"start": v(23.3, 16.7) * mm, "end": v(26.7, 16.7) * mm});
            skLineSegment(sketch, "E3.5.0.50", {"start": v(23.3, -11.7) * mm, "end": v(26.7, -11.7) * mm});
            skLineSegment(sketch, "E3.5.0.51", {"start": v(23.3, 6.7) * mm, "end": v(26.7, 6.7) * mm});
            skLineSegment(sketch, "E3.5.0.52", {"start": v(23.3, 11.7) * mm, "end": v(23.3, 8.3) * mm});
            skLineSegment(sketch, "E3.5.0.53", {"start": v(23.3, 11.7) * mm, "end": v(26.7, 11.7) * mm});
            skLineSegment(sketch, "E3.5.0.54", {"start": v(23.3, 36.7) * mm, "end": v(26.7, 36.7) * mm});
            skLineSegment(sketch, "E3.5.0.55", {"start": v(26.7, -23.3) * mm, "end": v(26.7, -26.7) * mm});
            skLineSegment(sketch, "E3.5.0.56", {"start": v(23.3, 26.7) * mm, "end": v(26.7, 26.7) * mm});
            skLineSegment(sketch, "E3.5.0.57", {"start": v(23.3, 31.7) * mm, "end": v(26.7, 31.7) * mm});
            skLineSegment(sketch, "E3.5.0.58", {"start": v(23.3, 21.7) * mm, "end": v(23.3, 18.3) * mm});
            skLineSegment(sketch, "E3.5.0.59", {"start": v(23.3, -6.7) * mm, "end": v(26.7, -6.7) * mm});
            skLineSegment(sketch, "E3.6.0.0", {"start": v(18.3, 36.7) * mm, "end": v(18.3, 33.3) * mm});
            skLineSegment(sketch, "E3.6.0.1", {"start": v(18.3, -21.7) * mm, "end": v(21.7, -21.7) * mm});
            skLineSegment(sketch, "E3.6.0.2", {"start": v(18.3, -3.3) * mm, "end": v(18.3, -6.7) * mm});
            skLineSegment(sketch, "E3.6.0.3", {"start": v(18.3, 8.3) * mm, "end": v(21.7, 8.3) * mm});
            skLineSegment(sketch, "E3.6.0.4", {"start": v(18.3, -33.3) * mm, "end": v(21.7, -33.3) * mm});
            skLineSegment(sketch, "E3.6.0.5", {"start": v(18.3, 31.7) * mm, "end": v(18.3, 28.3) * mm});
            skLineSegment(sketch, "E3.6.0.6", {"start": v(18.3, 1.7) * mm, "end": v(18.3, -1.7) * mm});
            skLineSegment(sketch, "E3.6.0.7", {"start": v(18.3, -18.3) * mm, "end": v(18.3, -21.7) * mm});
            skLineSegment(sketch, "E3.6.0.8", {"start": v(21.7, -33.3) * mm, "end": v(21.7, -36.7) * mm});
            skLineSegment(sketch, "E3.6.0.9", {"start": v(18.3, 16.7) * mm, "end": v(18.3, 13.3) * mm});
            skLineSegment(sketch, "E3.6.0.10", {"start": v(18.3, -8.3) * mm, "end": v(18.3, -11.7) * mm});
            skLineSegment(sketch, "E3.6.0.11", {"start": v(18.3, -36.7) * mm, "end": v(21.7, -36.7) * mm});
            skLineSegment(sketch, "E3.6.0.12", {"start": v(21.7, 26.7) * mm, "end": v(21.7, 23.3) * mm});
            skLineSegment(sketch, "E3.6.0.13", {"start": v(21.7, -28.3) * mm, "end": v(21.7, -31.7) * mm});
            skLineSegment(sketch, "E3.6.0.14", {"start": v(18.3, 23.3) * mm, "end": v(21.7, 23.3) * mm});
            skLineSegment(sketch, "E3.6.0.15", {"start": v(21.7, 6.7) * mm, "end": v(21.7, 3.3) * mm});
            skLineSegment(sketch, "E3.6.0.16", {"start": v(18.3, -28.3) * mm, "end": v(21.7, -28.3) * mm});
            skLineSegment(sketch, "E3.6.0.17", {"start": v(18.3, 13.3) * mm, "end": v(21.7, 13.3) * mm});
            skLineSegment(sketch, "E3.6.0.18", {"start": v(18.3, 33.3) * mm, "end": v(21.7, 33.3) * mm});
            skLineSegment(sketch, "E3.6.0.19", {"start": v(18.3, 3.3) * mm, "end": v(21.7, 3.3) * mm});
            skLineSegment(sketch, "E3.6.0.20", {"start": v(21.7, -13.3) * mm, "end": v(21.7, -16.7) * mm});
            skLineSegment(sketch, "E3.6.0.21", {"start": v(21.7, 16.7) * mm, "end": v(21.7, 13.3) * mm});
            skLineSegment(sketch, "E3.6.0.22", {"start": v(18.3, -23.3) * mm, "end": v(18.3, -26.7) * mm});
            skLineSegment(sketch, "E3.6.0.23", {"start": v(18.3, -28.3) * mm, "end": v(18.3, -31.7) * mm});
            skLineSegment(sketch, "E3.6.0.24", {"start": v(18.3, -13.3) * mm, "end": v(18.3, -16.7) * mm});
            skLineSegment(sketch, "E3.6.0.25", {"start": v(18.3, -23.3) * mm, "end": v(21.7, -23.3) * mm});
            skLineSegment(sketch, "E3.6.0.26", {"start": v(18.3, 1.7) * mm, "end": v(21.7, 1.7) * mm});
            skLineSegment(sketch, "E3.6.0.27", {"start": v(21.7, -3.3) * mm, "end": v(21.7, -6.7) * mm});
            skLineSegment(sketch, "E3.6.0.28", {"start": v(18.3, 28.3) * mm, "end": v(21.7, 28.3) * mm});
            skLineSegment(sketch, "E3.6.0.29", {"start": v(18.3, 21.7) * mm, "end": v(21.7, 21.7) * mm});
            skLineSegment(sketch, "E3.6.0.30", {"start": v(18.3, -18.3) * mm, "end": v(21.7, -18.3) * mm});
            skLineSegment(sketch, "E3.6.0.31", {"start": v(18.3, -13.3) * mm, "end": v(21.7, -13.3) * mm});
            skLineSegment(sketch, "E3.6.0.32", {"start": v(21.7, 1.7) * mm, "end": v(21.7, -1.7) * mm});
            skLineSegment(sketch, "E3.6.0.33", {"start": v(21.7, 36.7) * mm, "end": v(21.7, 33.3) * mm});
            skLineSegment(sketch, "E3.6.0.34", {"start": v(18.3, 18.3) * mm, "end": v(21.7, 18.3) * mm});
            skLineSegment(sketch, "E3.6.0.35", {"start": v(21.7, -18.3) * mm, "end": v(21.7, -21.7) * mm});
            skLineSegment(sketch, "E3.6.0.36", {"start": v(18.3, -33.3) * mm, "end": v(18.3, -36.7) * mm});
            skLineSegment(sketch, "E3.6.0.37", {"start": v(18.3, -3.3) * mm, "end": v(21.7, -3.3) * mm});
            skLineSegment(sketch, "E3.6.0.38", {"start": v(21.7, 21.7) * mm, "end": v(21.7, 18.3) * mm});
            skLineSegment(sketch, "E3.6.0.39", {"start": v(21.7, -8.3) * mm, "end": v(21.7, -11.7) * mm});
            skLineSegment(sketch, "E3.6.0.40", {"start": v(18.3, -16.7) * mm, "end": v(21.7, -16.7) * mm});
            skLineSegment(sketch, "E3.6.0.41", {"start": v(18.3, -31.7) * mm, "end": v(21.7, -31.7) * mm});
            skLineSegment(sketch, "E3.6.0.42", {"start": v(21.7, 31.7) * mm, "end": v(21.7, 28.3) * mm});
            skLineSegment(sketch, "E3.6.0.43", {"start": v(18.3, 26.7) * mm, "end": v(18.3, 23.3) * mm});
            skLineSegment(sketch, "E3.6.0.44", {"start": v(18.3, -1.7) * mm, "end": v(21.7, -1.7) * mm});
            skLineSegment(sketch, "E3.6.0.45", {"start": v(18.3, -26.7) * mm, "end": v(21.7, -26.7) * mm});
            skLineSegment(sketch, "E3.6.0.46", {"start": v(18.3, -8.3) * mm, "end": v(21.7, -8.3) * mm});
            skLineSegment(sketch, "E3.6.0.47", {"start": v(21.7, 11.7) * mm, "end": v(21.7, 8.3) * mm});
            skLineSegment(sketch, "E3.6.0.48", {"start": v(18.3, 6.7) * mm, "end": v(18.3, 3.3) * mm});
            skLineSegment(sketch, "E3.6.0.49", {"start": v(18.3, 16.7) * mm, "end": v(21.7, 16.7) * mm});
            skLineSegment(sketch, "E3.6.0.50", {"start": v(18.3, -11.7) * mm, "end": v(21.7, -11.7) * mm});
            skLineSegment(sketch, "E3.6.0.51", {"start": v(18.3, 6.7) * mm, "end": v(21.7, 6.7) * mm});
            skLineSegment(sketch, "E3.6.0.52", {"start": v(18.3, 11.7) * mm, "end": v(18.3, 8.3) * mm});
            skLineSegment(sketch, "E3.6.0.53", {"start": v(18.3, 11.7) * mm, "end": v(21.7, 11.7) * mm});
            skLineSegment(sketch, "E3.6.0.54", {"start": v(18.3, 36.7) * mm, "end": v(21.7, 36.7) * mm});
            skLineSegment(sketch, "E3.6.0.55", {"start": v(21.7, -23.3) * mm, "end": v(21.7, -26.7) * mm});
            skLineSegment(sketch, "E3.6.0.56", {"start": v(18.3, 26.7) * mm, "end": v(21.7, 26.7) * mm});
            skLineSegment(sketch, "E3.6.0.57", {"start": v(18.3, 31.7) * mm, "end": v(21.7, 31.7) * mm});
            skLineSegment(sketch, "E3.6.0.58", {"start": v(18.3, 21.7) * mm, "end": v(18.3, 18.3) * mm});
            skLineSegment(sketch, "E3.6.0.59", {"start": v(18.3, -6.7) * mm, "end": v(21.7, -6.7) * mm});
            skLineSegment(sketch, "E3.7.0.0", {"start": v(13.3, 36.7) * mm, "end": v(13.3, 33.3) * mm});
            skLineSegment(sketch, "E3.7.0.1", {"start": v(13.3, -21.7) * mm, "end": v(16.7, -21.7) * mm});
            skLineSegment(sketch, "E3.7.0.2", {"start": v(13.3, -3.3) * mm, "end": v(13.3, -6.7) * mm});
            skLineSegment(sketch, "E3.7.0.3", {"start": v(13.3, 8.3) * mm, "end": v(16.7, 8.3) * mm});
            skLineSegment(sketch, "E3.7.0.4", {"start": v(13.3, -33.3) * mm, "end": v(16.7, -33.3) * mm});
            skLineSegment(sketch, "E3.7.0.5", {"start": v(13.3, 31.7) * mm, "end": v(13.3, 28.3) * mm});
            skLineSegment(sketch, "E3.7.0.6", {"start": v(13.3, 1.7) * mm, "end": v(13.3, -1.7) * mm});
            skLineSegment(sketch, "E3.7.0.7", {"start": v(13.3, -18.3) * mm, "end": v(13.3, -21.7) * mm});
            skLineSegment(sketch, "E3.7.0.8", {"start": v(16.7, -33.3) * mm, "end": v(16.7, -36.7) * mm});
            skLineSegment(sketch, "E3.7.0.9", {"start": v(13.3, 16.7) * mm, "end": v(13.3, 13.3) * mm});
            skLineSegment(sketch, "E3.7.0.10", {"start": v(13.3, -8.3) * mm, "end": v(13.3, -11.7) * mm});
            skLineSegment(sketch, "E3.7.0.11", {"start": v(13.3, -36.7) * mm, "end": v(16.7, -36.7) * mm});
            skLineSegment(sketch, "E3.7.0.12", {"start": v(16.7, 26.7) * mm, "end": v(16.7, 23.3) * mm});
            skLineSegment(sketch, "E3.7.0.13", {"start": v(16.7, -28.3) * mm, "end": v(16.7, -31.7) * mm});
            skLineSegment(sketch, "E3.7.0.14", {"start": v(13.3, 23.3) * mm, "end": v(16.7, 23.3) * mm});
            skLineSegment(sketch, "E3.7.0.15", {"start": v(16.7, 6.7) * mm, "end": v(16.7, 3.3) * mm});
            skLineSegment(sketch, "E3.7.0.16", {"start": v(13.3, -28.3) * mm, "end": v(16.7, -28.3) * mm});
            skLineSegment(sketch, "E3.7.0.17", {"start": v(13.3, 13.3) * mm, "end": v(16.7, 13.3) * mm});
            skLineSegment(sketch, "E3.7.0.18", {"start": v(13.3, 33.3) * mm, "end": v(16.7, 33.3) * mm});
            skLineSegment(sketch, "E3.7.0.19", {"start": v(13.3, 3.3) * mm, "end": v(16.7, 3.3) * mm});
            skLineSegment(sketch, "E3.7.0.20", {"start": v(16.7, -13.3) * mm, "end": v(16.7, -16.7) * mm});
            skLineSegment(sketch, "E3.7.0.21", {"start": v(16.7, 16.7) * mm, "end": v(16.7, 13.3) * mm});
            skLineSegment(sketch, "E3.7.0.22", {"start": v(13.3, -23.3) * mm, "end": v(13.3, -26.7) * mm});
            skLineSegment(sketch, "E3.7.0.23", {"start": v(13.3, -28.3) * mm, "end": v(13.3, -31.7) * mm});
            skLineSegment(sketch, "E3.7.0.24", {"start": v(13.3, -13.3) * mm, "end": v(13.3, -16.7) * mm});
            skLineSegment(sketch, "E3.7.0.25", {"start": v(13.3, -23.3) * mm, "end": v(16.7, -23.3) * mm});
            skLineSegment(sketch, "E3.7.0.26", {"start": v(13.3, 1.7) * mm, "end": v(16.7, 1.7) * mm});
            skLineSegment(sketch, "E3.7.0.27", {"start": v(16.7, -3.3) * mm, "end": v(16.7, -6.7) * mm});
            skLineSegment(sketch, "E3.7.0.28", {"start": v(13.3, 28.3) * mm, "end": v(16.7, 28.3) * mm});
            skLineSegment(sketch, "E3.7.0.29", {"start": v(13.3, 21.7) * mm, "end": v(16.7, 21.7) * mm});
            skLineSegment(sketch, "E3.7.0.30", {"start": v(13.3, -18.3) * mm, "end": v(16.7, -18.3) * mm});
            skLineSegment(sketch, "E3.7.0.31", {"start": v(13.3, -13.3) * mm, "end": v(16.7, -13.3) * mm});
            skLineSegment(sketch, "E3.7.0.32", {"start": v(16.7, 1.7) * mm, "end": v(16.7, -1.7) * mm});
            skLineSegment(sketch, "E3.7.0.33", {"start": v(16.7, 36.7) * mm, "end": v(16.7, 33.3) * mm});
            skLineSegment(sketch, "E3.7.0.34", {"start": v(13.3, 18.3) * mm, "end": v(16.7, 18.3) * mm});
            skLineSegment(sketch, "E3.7.0.35", {"start": v(16.7, -18.3) * mm, "end": v(16.7, -21.7) * mm});
            skLineSegment(sketch, "E3.7.0.36", {"start": v(13.3, -33.3) * mm, "end": v(13.3, -36.7) * mm});
            skLineSegment(sketch, "E3.7.0.37", {"start": v(13.3, -3.3) * mm, "end": v(16.7, -3.3) * mm});
            skLineSegment(sketch, "E3.7.0.38", {"start": v(16.7, 21.7) * mm, "end": v(16.7, 18.3) * mm});
            skLineSegment(sketch, "E3.7.0.39", {"start": v(16.7, -8.3) * mm, "end": v(16.7, -11.7) * mm});
            skLineSegment(sketch, "E3.7.0.40", {"start": v(13.3, -16.7) * mm, "end": v(16.7, -16.7) * mm});
            skLineSegment(sketch, "E3.7.0.41", {"start": v(13.3, -31.7) * mm, "end": v(16.7, -31.7) * mm});
            skLineSegment(sketch, "E3.7.0.42", {"start": v(16.7, 31.7) * mm, "end": v(16.7, 28.3) * mm});
            skLineSegment(sketch, "E3.7.0.43", {"start": v(13.3, 26.7) * mm, "end": v(13.3, 23.3) * mm});
            skLineSegment(sketch, "E3.7.0.44", {"start": v(13.3, -1.7) * mm, "end": v(16.7, -1.7) * mm});
            skLineSegment(sketch, "E3.7.0.45", {"start": v(13.3, -26.7) * mm, "end": v(16.7, -26.7) * mm});
            skLineSegment(sketch, "E3.7.0.46", {"start": v(13.3, -8.3) * mm, "end": v(16.7, -8.3) * mm});
            skLineSegment(sketch, "E3.7.0.47", {"start": v(16.7, 11.7) * mm, "end": v(16.7, 8.3) * mm});
            skLineSegment(sketch, "E3.7.0.48", {"start": v(13.3, 6.7) * mm, "end": v(13.3, 3.3) * mm});
            skLineSegment(sketch, "E3.7.0.49", {"start": v(13.3, 16.7) * mm, "end": v(16.7, 16.7) * mm});
            skLineSegment(sketch, "E3.7.0.50", {"start": v(13.3, -11.7) * mm, "end": v(16.7, -11.7) * mm});
            skLineSegment(sketch, "E3.7.0.51", {"start": v(13.3, 6.7) * mm, "end": v(16.7, 6.7) * mm});
            skLineSegment(sketch, "E3.7.0.52", {"start": v(13.3, 11.7) * mm, "end": v(13.3, 8.3) * mm});
            skLineSegment(sketch, "E3.7.0.53", {"start": v(13.3, 11.7) * mm, "end": v(16.7, 11.7) * mm});
            skLineSegment(sketch, "E3.7.0.54", {"start": v(13.3, 36.7) * mm, "end": v(16.7, 36.7) * mm});
            skLineSegment(sketch, "E3.7.0.55", {"start": v(16.7, -23.3) * mm, "end": v(16.7, -26.7) * mm});
            skLineSegment(sketch, "E3.7.0.56", {"start": v(13.3, 26.7) * mm, "end": v(16.7, 26.7) * mm});
            skLineSegment(sketch, "E3.7.0.57", {"start": v(13.3, 31.7) * mm, "end": v(16.7, 31.7) * mm});
            skLineSegment(sketch, "E3.7.0.58", {"start": v(13.3, 21.7) * mm, "end": v(13.3, 18.3) * mm});
            skLineSegment(sketch, "E3.7.0.59", {"start": v(13.3, -6.7) * mm, "end": v(16.7, -6.7) * mm});
            skLineSegment(sketch, "E3.8.0.0", {"start": v(8.3, 36.7) * mm, "end": v(8.3, 33.3) * mm});
            skLineSegment(sketch, "E3.8.0.1", {"start": v(8.3, -21.7) * mm, "end": v(11.7, -21.7) * mm});
            skLineSegment(sketch, "E3.8.0.2", {"start": v(8.3, -3.3) * mm, "end": v(8.3, -6.7) * mm});
            skLineSegment(sketch, "E3.8.0.3", {"start": v(8.3, 8.3) * mm, "end": v(11.7, 8.3) * mm});
            skLineSegment(sketch, "E3.8.0.4", {"start": v(8.3, -33.3) * mm, "end": v(11.7, -33.3) * mm});
            skLineSegment(sketch, "E3.8.0.5", {"start": v(8.3, 31.7) * mm, "end": v(8.3, 28.3) * mm});
            skLineSegment(sketch, "E3.8.0.6", {"start": v(8.3, 1.7) * mm, "end": v(8.3, -1.7) * mm});
            skLineSegment(sketch, "E3.8.0.7", {"start": v(8.3, -18.3) * mm, "end": v(8.3, -21.7) * mm});
            skLineSegment(sketch, "E3.8.0.8", {"start": v(11.7, -33.3) * mm, "end": v(11.7, -36.7) * mm});
            skLineSegment(sketch, "E3.8.0.9", {"start": v(8.3, 16.7) * mm, "end": v(8.3, 13.3) * mm});
            skLineSegment(sketch, "E3.8.0.10", {"start": v(8.3, -8.3) * mm, "end": v(8.3, -11.7) * mm});
            skLineSegment(sketch, "E3.8.0.11", {"start": v(8.3, -36.7) * mm, "end": v(11.7, -36.7) * mm});
            skLineSegment(sketch, "E3.8.0.12", {"start": v(11.7, 26.7) * mm, "end": v(11.7, 23.3) * mm});
            skLineSegment(sketch, "E3.8.0.13", {"start": v(11.7, -28.3) * mm, "end": v(11.7, -31.7) * mm});
            skLineSegment(sketch, "E3.8.0.14", {"start": v(8.3, 23.3) * mm, "end": v(11.7, 23.3) * mm});
            skLineSegment(sketch, "E3.8.0.15", {"start": v(11.7, 6.7) * mm, "end": v(11.7, 3.3) * mm});
            skLineSegment(sketch, "E3.8.0.16", {"start": v(8.3, -28.3) * mm, "end": v(11.7, -28.3) * mm});
            skLineSegment(sketch, "E3.8.0.17", {"start": v(8.3, 13.3) * mm, "end": v(11.7, 13.3) * mm});
            skLineSegment(sketch, "E3.8.0.18", {"start": v(8.3, 33.3) * mm, "end": v(11.7, 33.3) * mm});
            skLineSegment(sketch, "E3.8.0.19", {"start": v(8.3, 3.3) * mm, "end": v(11.7, 3.3) * mm});
            skLineSegment(sketch, "E3.8.0.20", {"start": v(11.7, -13.3) * mm, "end": v(11.7, -16.7) * mm});
            skLineSegment(sketch, "E3.8.0.21", {"start": v(11.7, 16.7) * mm, "end": v(11.7, 13.3) * mm});
            skLineSegment(sketch, "E3.8.0.22", {"start": v(8.3, -23.3) * mm, "end": v(8.3, -26.7) * mm});
            skLineSegment(sketch, "E3.8.0.23", {"start": v(8.3, -28.3) * mm, "end": v(8.3, -31.7) * mm});
            skLineSegment(sketch, "E3.8.0.24", {"start": v(8.3, -13.3) * mm, "end": v(8.3, -16.7) * mm});
            skLineSegment(sketch, "E3.8.0.25", {"start": v(8.3, -23.3) * mm, "end": v(11.7, -23.3) * mm});
            skLineSegment(sketch, "E3.8.0.26", {"start": v(8.3, 1.7) * mm, "end": v(11.7, 1.7) * mm});
            skLineSegment(sketch, "E3.8.0.27", {"start": v(11.7, -3.3) * mm, "end": v(11.7, -6.7) * mm});
            skLineSegment(sketch, "E3.8.0.28", {"start": v(8.3, 28.3) * mm, "end": v(11.7, 28.3) * mm});
            skLineSegment(sketch, "E3.8.0.29", {"start": v(8.3, 21.7) * mm, "end": v(11.7, 21.7) * mm});
            skLineSegment(sketch, "E3.8.0.30", {"start": v(8.3, -18.3) * mm, "end": v(11.7, -18.3) * mm});
            skLineSegment(sketch, "E3.8.0.31", {"start": v(8.3, -13.3) * mm, "end": v(11.7, -13.3) * mm});
            skLineSegment(sketch, "E3.8.0.32", {"start": v(11.7, 1.7) * mm, "end": v(11.7, -1.7) * mm});
            skLineSegment(sketch, "E3.8.0.33", {"start": v(11.7, 36.7) * mm, "end": v(11.7, 33.3) * mm});
            skLineSegment(sketch, "E3.8.0.34", {"start": v(8.3, 18.3) * mm, "end": v(11.7, 18.3) * mm});
            skLineSegment(sketch, "E3.8.0.35", {"start": v(11.7, -18.3) * mm, "end": v(11.7, -21.7) * mm});
            skLineSegment(sketch, "E3.8.0.36", {"start": v(8.3, -33.3) * mm, "end": v(8.3, -36.7) * mm});
            skLineSegment(sketch, "E3.8.0.37", {"start": v(8.3, -3.3) * mm, "end": v(11.7, -3.3) * mm});
            skLineSegment(sketch, "E3.8.0.38", {"start": v(11.7, 21.7) * mm, "end": v(11.7, 18.3) * mm});
            skLineSegment(sketch, "E3.8.0.39", {"start": v(11.7, -8.3) * mm, "end": v(11.7, -11.7) * mm});
            skLineSegment(sketch, "E3.8.0.40", {"start": v(8.3, -16.7) * mm, "end": v(11.7, -16.7) * mm});
            skLineSegment(sketch, "E3.8.0.41", {"start": v(8.3, -31.7) * mm, "end": v(11.7, -31.7) * mm});
            skLineSegment(sketch, "E3.8.0.42", {"start": v(11.7, 31.7) * mm, "end": v(11.7, 28.3) * mm});
            skLineSegment(sketch, "E3.8.0.43", {"start": v(8.3, 26.7) * mm, "end": v(8.3, 23.3) * mm});
            skLineSegment(sketch, "E3.8.0.44", {"start": v(8.3, -1.7) * mm, "end": v(11.7, -1.7) * mm});
            skLineSegment(sketch, "E3.8.0.45", {"start": v(8.3, -26.7) * mm, "end": v(11.7, -26.7) * mm});
            skLineSegment(sketch, "E3.8.0.46", {"start": v(8.3, -8.3) * mm, "end": v(11.7, -8.3) * mm});
            skLineSegment(sketch, "E3.8.0.47", {"start": v(11.7, 11.7) * mm, "end": v(11.7, 8.3) * mm});
            skLineSegment(sketch, "E3.8.0.48", {"start": v(8.3, 6.7) * mm, "end": v(8.3, 3.3) * mm});
            skLineSegment(sketch, "E3.8.0.49", {"start": v(8.3, 16.7) * mm, "end": v(11.7, 16.7) * mm});
            skLineSegment(sketch, "E3.8.0.50", {"start": v(8.3, -11.7) * mm, "end": v(11.7, -11.7) * mm});
            skLineSegment(sketch, "E3.8.0.51", {"start": v(8.3, 6.7) * mm, "end": v(11.7, 6.7) * mm});
            skLineSegment(sketch, "E3.8.0.52", {"start": v(8.3, 11.7) * mm, "end": v(8.3, 8.3) * mm});
            skLineSegment(sketch, "E3.8.0.53", {"start": v(8.3, 11.7) * mm, "end": v(11.7, 11.7) * mm});
            skLineSegment(sketch, "E3.8.0.54", {"start": v(8.3, 36.7) * mm, "end": v(11.7, 36.7) * mm});
            skLineSegment(sketch, "E3.8.0.55", {"start": v(11.7, -23.3) * mm, "end": v(11.7, -26.7) * mm});
            skLineSegment(sketch, "E3.8.0.56", {"start": v(8.3, 26.7) * mm, "end": v(11.7, 26.7) * mm});
            skLineSegment(sketch, "E3.8.0.57", {"start": v(8.3, 31.7) * mm, "end": v(11.7, 31.7) * mm});
            skLineSegment(sketch, "E3.8.0.58", {"start": v(8.3, 21.7) * mm, "end": v(8.3, 18.3) * mm});
            skLineSegment(sketch, "E3.8.0.59", {"start": v(8.3, -6.7) * mm, "end": v(11.7, -6.7) * mm});
            skLineSegment(sketch, "E3.9.0.0", {"start": v(3.3, 36.7) * mm, "end": v(3.3, 33.3) * mm});
            skLineSegment(sketch, "E3.9.0.1", {"start": v(3.3, -21.7) * mm, "end": v(6.7, -21.7) * mm});
            skLineSegment(sketch, "E3.9.0.2", {"start": v(3.3, -3.3) * mm, "end": v(3.3, -6.7) * mm});
            skLineSegment(sketch, "E3.9.0.3", {"start": v(3.3, 8.3) * mm, "end": v(6.7, 8.3) * mm});
            skLineSegment(sketch, "E3.9.0.4", {"start": v(3.3, -33.3) * mm, "end": v(6.7, -33.3) * mm});
            skLineSegment(sketch, "E3.9.0.5", {"start": v(3.3, 31.7) * mm, "end": v(3.3, 28.3) * mm});
            skLineSegment(sketch, "E3.9.0.6", {"start": v(3.3, 1.7) * mm, "end": v(3.3, -1.7) * mm});
            skLineSegment(sketch, "E3.9.0.7", {"start": v(3.3, -18.3) * mm, "end": v(3.3, -21.7) * mm});
            skLineSegment(sketch, "E3.9.0.8", {"start": v(6.7, -33.3) * mm, "end": v(6.7, -36.7) * mm});
            skLineSegment(sketch, "E3.9.0.9", {"start": v(3.3, 16.7) * mm, "end": v(3.3, 13.3) * mm});
            skLineSegment(sketch, "E3.9.0.10", {"start": v(3.3, -8.3) * mm, "end": v(3.3, -11.7) * mm});
            skLineSegment(sketch, "E3.9.0.11", {"start": v(3.3, -36.7) * mm, "end": v(6.7, -36.7) * mm});
            skLineSegment(sketch, "E3.9.0.12", {"start": v(6.7, 26.7) * mm, "end": v(6.7, 23.3) * mm});
            skLineSegment(sketch, "E3.9.0.13", {"start": v(6.7, -28.3) * mm, "end": v(6.7, -31.7) * mm});
            skLineSegment(sketch, "E3.9.0.14", {"start": v(3.3, 23.3) * mm, "end": v(6.7, 23.3) * mm});
            skLineSegment(sketch, "E3.9.0.15", {"start": v(6.7, 6.7) * mm, "end": v(6.7, 3.3) * mm});
            skLineSegment(sketch, "E3.9.0.16", {"start": v(3.3, -28.3) * mm, "end": v(6.7, -28.3) * mm});
            skLineSegment(sketch, "E3.9.0.17", {"start": v(3.3, 13.3) * mm, "end": v(6.7, 13.3) * mm});
            skLineSegment(sketch, "E3.9.0.18", {"start": v(3.3, 33.3) * mm, "end": v(6.7, 33.3) * mm});
            skLineSegment(sketch, "E3.9.0.19", {"start": v(3.3, 3.3) * mm, "end": v(6.7, 3.3) * mm});
            skLineSegment(sketch, "E3.9.0.20", {"start": v(6.7, -13.3) * mm, "end": v(6.7, -16.7) * mm});
            skLineSegment(sketch, "E3.9.0.21", {"start": v(6.7, 16.7) * mm, "end": v(6.7, 13.3) * mm});
            skLineSegment(sketch, "E3.9.0.22", {"start": v(3.3, -23.3) * mm, "end": v(3.3, -26.7) * mm});
            skLineSegment(sketch, "E3.9.0.23", {"start": v(3.3, -28.3) * mm, "end": v(3.3, -31.7) * mm});
            skLineSegment(sketch, "E3.9.0.24", {"start": v(3.3, -13.3) * mm, "end": v(3.3, -16.7) * mm});
            skLineSegment(sketch, "E3.9.0.25", {"start": v(3.3, -23.3) * mm, "end": v(6.7, -23.3) * mm});
            skLineSegment(sketch, "E3.9.0.26", {"start": v(3.3, 1.7) * mm, "end": v(6.7, 1.7) * mm});
            skLineSegment(sketch, "E3.9.0.27", {"start": v(6.7, -3.3) * mm, "end": v(6.7, -6.7) * mm});
            skLineSegment(sketch, "E3.9.0.28", {"start": v(3.3, 28.3) * mm, "end": v(6.7, 28.3) * mm});
            skLineSegment(sketch, "E3.9.0.29", {"start": v(3.3, 21.7) * mm, "end": v(6.7, 21.7) * mm});
            skLineSegment(sketch, "E3.9.0.30", {"start": v(3.3, -18.3) * mm, "end": v(6.7, -18.3) * mm});
            skLineSegment(sketch, "E3.9.0.31", {"start": v(3.3, -13.3) * mm, "end": v(6.7, -13.3) * mm});
            skLineSegment(sketch, "E3.9.0.32", {"start": v(6.7, 1.7) * mm, "end": v(6.7, -1.7) * mm});
            skLineSegment(sketch, "E3.9.0.33", {"start": v(6.7, 36.7) * mm, "end": v(6.7, 33.3) * mm});
            skLineSegment(sketch, "E3.9.0.34", {"start": v(3.3, 18.3) * mm, "end": v(6.7, 18.3) * mm});
            skLineSegment(sketch, "E3.9.0.35", {"start": v(6.7, -18.3) * mm, "end": v(6.7, -21.7) * mm});
            skLineSegment(sketch, "E3.9.0.36", {"start": v(3.3, -33.3) * mm, "end": v(3.3, -36.7) * mm});
            skLineSegment(sketch, "E3.9.0.37", {"start": v(3.3, -3.3) * mm, "end": v(6.7, -3.3) * mm});
            skLineSegment(sketch, "E3.9.0.38", {"start": v(6.7, 21.7) * mm, "end": v(6.7, 18.3) * mm});
            skLineSegment(sketch, "E3.9.0.39", {"start": v(6.7, -8.3) * mm, "end": v(6.7, -11.7) * mm});
            skLineSegment(sketch, "E3.9.0.40", {"start": v(3.3, -16.7) * mm, "end": v(6.7, -16.7) * mm});
            skLineSegment(sketch, "E3.9.0.41", {"start": v(3.3, -31.7) * mm, "end": v(6.7, -31.7) * mm});
            skLineSegment(sketch, "E3.9.0.42", {"start": v(6.7, 31.7) * mm, "end": v(6.7, 28.3) * mm});
            skLineSegment(sketch, "E3.9.0.43", {"start": v(3.3, 26.7) * mm, "end": v(3.3, 23.3) * mm});
            skLineSegment(sketch, "E3.9.0.44", {"start": v(3.3, -1.7) * mm, "end": v(6.7, -1.7) * mm});
            skLineSegment(sketch, "E3.9.0.45", {"start": v(3.3, -26.7) * mm, "end": v(6.7, -26.7) * mm});
            skLineSegment(sketch, "E3.9.0.46", {"start": v(3.3, -8.3) * mm, "end": v(6.7, -8.3) * mm});
            skLineSegment(sketch, "E3.9.0.47", {"start": v(6.7, 11.7) * mm, "end": v(6.7, 8.3) * mm});
            skLineSegment(sketch, "E3.9.0.48", {"start": v(3.3, 6.7) * mm, "end": v(3.3, 3.3) * mm});
            skLineSegment(sketch, "E3.9.0.49", {"start": v(3.3, 16.7) * mm, "end": v(6.7, 16.7) * mm});
            skLineSegment(sketch, "E3.9.0.50", {"start": v(3.3, -11.7) * mm, "end": v(6.7, -11.7) * mm});
            skLineSegment(sketch, "E3.9.0.51", {"start": v(3.3, 6.7) * mm, "end": v(6.7, 6.7) * mm});
            skLineSegment(sketch, "E3.9.0.52", {"start": v(3.3, 11.7) * mm, "end": v(3.3, 8.3) * mm});
            skLineSegment(sketch, "E3.9.0.53", {"start": v(3.3, 11.7) * mm, "end": v(6.7, 11.7) * mm});
            skLineSegment(sketch, "E3.9.0.54", {"start": v(3.3, 36.7) * mm, "end": v(6.7, 36.7) * mm});
            skLineSegment(sketch, "E3.9.0.55", {"start": v(6.7, -23.3) * mm, "end": v(6.7, -26.7) * mm});
            skLineSegment(sketch, "E3.9.0.56", {"start": v(3.3, 26.7) * mm, "end": v(6.7, 26.7) * mm});
            skLineSegment(sketch, "E3.9.0.57", {"start": v(3.3, 31.7) * mm, "end": v(6.7, 31.7) * mm});
            skLineSegment(sketch, "E3.9.0.58", {"start": v(3.3, 21.7) * mm, "end": v(3.3, 18.3) * mm});
            skLineSegment(sketch, "E3.9.0.59", {"start": v(3.3, -6.7) * mm, "end": v(6.7, -6.7) * mm});
            skLineSegment(sketch, "E3.10.0.0", {"start": v(-1.7, 36.7) * mm, "end": v(-1.7, 33.3) * mm});
            skLineSegment(sketch, "E3.10.0.1", {"start": v(-1.7, -21.7) * mm, "end": v(1.7, -21.7) * mm});
            skLineSegment(sketch, "E3.10.0.2", {"start": v(-1.7, -3.3) * mm, "end": v(-1.7, -6.7) * mm});
            skLineSegment(sketch, "E3.10.0.3", {"start": v(-1.7, 8.3) * mm, "end": v(1.7, 8.3) * mm});
            skLineSegment(sketch, "E3.10.0.4", {"start": v(-1.7, -33.3) * mm, "end": v(1.7, -33.3) * mm});
            skLineSegment(sketch, "E3.10.0.5", {"start": v(-1.7, 31.7) * mm, "end": v(-1.7, 28.3) * mm});
            skLineSegment(sketch, "E3.10.0.6", {"start": v(-1.7, 1.7) * mm, "end": v(-1.7, -1.7) * mm});
            skLineSegment(sketch, "E3.10.0.7", {"start": v(-1.7, -18.3) * mm, "end": v(-1.7, -21.7) * mm});
            skLineSegment(sketch, "E3.10.0.8", {"start": v(1.7, -33.3) * mm, "end": v(1.7, -36.7) * mm});
            skLineSegment(sketch, "E3.10.0.9", {"start": v(-1.7, 16.7) * mm, "end": v(-1.7, 13.3) * mm});
            skLineSegment(sketch, "E3.10.0.10", {"start": v(-1.7, -8.3) * mm, "end": v(-1.7, -11.7) * mm});
            skLineSegment(sketch, "E3.10.0.11", {"start": v(-1.7, -36.7) * mm, "end": v(1.7, -36.7) * mm});
            skLineSegment(sketch, "E3.10.0.12", {"start": v(1.7, 26.7) * mm, "end": v(1.7, 23.3) * mm});
            skLineSegment(sketch, "E3.10.0.13", {"start": v(1.7, -28.3) * mm, "end": v(1.7, -31.7) * mm});
            skLineSegment(sketch, "E3.10.0.14", {"start": v(-1.7, 23.3) * mm, "end": v(1.7, 23.3) * mm});
            skLineSegment(sketch, "E3.10.0.15", {"start": v(1.7, 6.7) * mm, "end": v(1.7, 3.3) * mm});
            skLineSegment(sketch, "E3.10.0.16", {"start": v(-1.7, -28.3) * mm, "end": v(1.7, -28.3) * mm});
            skLineSegment(sketch, "E3.10.0.17", {"start": v(-1.7, 13.3) * mm, "end": v(1.7, 13.3) * mm});
            skLineSegment(sketch, "E3.10.0.18", {"start": v(-1.7, 33.3) * mm, "end": v(1.7, 33.3) * mm});
            skLineSegment(sketch, "E3.10.0.19", {"start": v(-1.7, 3.3) * mm, "end": v(1.7, 3.3) * mm});
            skLineSegment(sketch, "E3.10.0.20", {"start": v(1.7, -13.3) * mm, "end": v(1.7, -16.7) * mm});
            skLineSegment(sketch, "E3.10.0.21", {"start": v(1.7, 16.7) * mm, "end": v(1.7, 13.3) * mm});
            skLineSegment(sketch, "E3.10.0.22", {"start": v(-1.7, -23.3) * mm, "end": v(-1.7, -26.7) * mm});
            skLineSegment(sketch, "E3.10.0.23", {"start": v(-1.7, -28.3) * mm, "end": v(-1.7, -31.7) * mm});
            skLineSegment(sketch, "E3.10.0.24", {"start": v(-1.7, -13.3) * mm, "end": v(-1.7, -16.7) * mm});
            skLineSegment(sketch, "E3.10.0.25", {"start": v(-1.7, -23.3) * mm, "end": v(1.7, -23.3) * mm});
            skLineSegment(sketch, "E3.10.0.26", {"start": v(-1.7, 1.7) * mm, "end": v(1.7, 1.7) * mm});
            skLineSegment(sketch, "E3.10.0.27", {"start": v(1.7, -3.3) * mm, "end": v(1.7, -6.7) * mm});
            skLineSegment(sketch, "E3.10.0.28", {"start": v(-1.7, 28.3) * mm, "end": v(1.7, 28.3) * mm});
            skLineSegment(sketch, "E3.10.0.29", {"start": v(-1.7, 21.7) * mm, "end": v(1.7, 21.7) * mm});
            skLineSegment(sketch, "E3.10.0.30", {"start": v(-1.7, -18.3) * mm, "end": v(1.7, -18.3) * mm});
            skLineSegment(sketch, "E3.10.0.31", {"start": v(-1.7, -13.3) * mm, "end": v(1.7, -13.3) * mm});
            skLineSegment(sketch, "E3.10.0.32", {"start": v(1.7, 1.7) * mm, "end": v(1.7, -1.7) * mm});
            skLineSegment(sketch, "E3.10.0.33", {"start": v(1.7, 36.7) * mm, "end": v(1.7, 33.3) * mm});
            skLineSegment(sketch, "E3.10.0.34", {"start": v(-1.7, 18.3) * mm, "end": v(1.7, 18.3) * mm});
            skLineSegment(sketch, "E3.10.0.35", {"start": v(1.7, -18.3) * mm, "end": v(1.7, -21.7) * mm});
            skLineSegment(sketch, "E3.10.0.36", {"start": v(-1.7, -33.3) * mm, "end": v(-1.7, -36.7) * mm});
            skLineSegment(sketch, "E3.10.0.37", {"start": v(-1.7, -3.3) * mm, "end": v(1.7, -3.3) * mm});
            skLineSegment(sketch, "E3.10.0.38", {"start": v(1.7, 21.7) * mm, "end": v(1.7, 18.3) * mm});
            skLineSegment(sketch, "E3.10.0.39", {"start": v(1.7, -8.3) * mm, "end": v(1.7, -11.7) * mm});
            skLineSegment(sketch, "E3.10.0.40", {"start": v(-1.7, -16.7) * mm, "end": v(1.7, -16.7) * mm});
            skLineSegment(sketch, "E3.10.0.41", {"start": v(-1.7, -31.7) * mm, "end": v(1.7, -31.7) * mm});
            skLineSegment(sketch, "E3.10.0.42", {"start": v(1.7, 31.7) * mm, "end": v(1.7, 28.3) * mm});
            skLineSegment(sketch, "E3.10.0.43", {"start": v(-1.7, 26.7) * mm, "end": v(-1.7, 23.3) * mm});
            skLineSegment(sketch, "E3.10.0.44", {"start": v(-1.7, -1.7) * mm, "end": v(1.7, -1.7) * mm});
            skLineSegment(sketch, "E3.10.0.45", {"start": v(-1.7, -26.7) * mm, "end": v(1.7, -26.7) * mm});
            skLineSegment(sketch, "E3.10.0.46", {"start": v(-1.7, -8.3) * mm, "end": v(1.7, -8.3) * mm});
            skLineSegment(sketch, "E3.10.0.47", {"start": v(1.7, 11.7) * mm, "end": v(1.7, 8.3) * mm});
            skLineSegment(sketch, "E3.10.0.48", {"start": v(-1.7, 6.7) * mm, "end": v(-1.7, 3.3) * mm});
            skLineSegment(sketch, "E3.10.0.49", {"start": v(-1.7, 16.7) * mm, "end": v(1.7, 16.7) * mm});
            skLineSegment(sketch, "E3.10.0.50", {"start": v(-1.7, -11.7) * mm, "end": v(1.7, -11.7) * mm});
            skLineSegment(sketch, "E3.10.0.51", {"start": v(-1.7, 6.7) * mm, "end": v(1.7, 6.7) * mm});
            skLineSegment(sketch, "E3.10.0.52", {"start": v(-1.7, 11.7) * mm, "end": v(-1.7, 8.3) * mm});
            skLineSegment(sketch, "E3.10.0.53", {"start": v(-1.7, 11.7) * mm, "end": v(1.7, 11.7) * mm});
            skLineSegment(sketch, "E3.10.0.54", {"start": v(-1.7, 36.7) * mm, "end": v(1.7, 36.7) * mm});
            skLineSegment(sketch, "E3.10.0.55", {"start": v(1.7, -23.3) * mm, "end": v(1.7, -26.7) * mm});
            skLineSegment(sketch, "E3.10.0.56", {"start": v(-1.7, 26.7) * mm, "end": v(1.7, 26.7) * mm});
            skLineSegment(sketch, "E3.10.0.57", {"start": v(-1.7, 31.7) * mm, "end": v(1.7, 31.7) * mm});
            skLineSegment(sketch, "E3.10.0.58", {"start": v(-1.7, 21.7) * mm, "end": v(-1.7, 18.3) * mm});
            skLineSegment(sketch, "E3.10.0.59", {"start": v(-1.7, -6.7) * mm, "end": v(1.7, -6.7) * mm});
            skLineSegment(sketch, "E3.11.0.0", {"start": v(-6.7, 36.7) * mm, "end": v(-6.7, 33.3) * mm});
            skLineSegment(sketch, "E3.11.0.1", {"start": v(-6.7, -21.7) * mm, "end": v(-3.3, -21.7) * mm});
            skLineSegment(sketch, "E3.11.0.2", {"start": v(-6.7, -3.3) * mm, "end": v(-6.7, -6.7) * mm});
            skLineSegment(sketch, "E3.11.0.3", {"start": v(-6.7, 8.3) * mm, "end": v(-3.3, 8.3) * mm});
            skLineSegment(sketch, "E3.11.0.4", {"start": v(-6.7, -33.3) * mm, "end": v(-3.3, -33.3) * mm});
            skLineSegment(sketch, "E3.11.0.5", {"start": v(-6.7, 31.7) * mm, "end": v(-6.7, 28.3) * mm});
            skLineSegment(sketch, "E3.11.0.6", {"start": v(-6.7, 1.7) * mm, "end": v(-6.7, -1.7) * mm});
            skLineSegment(sketch, "E3.11.0.7", {"start": v(-6.7, -18.3) * mm, "end": v(-6.7, -21.7) * mm});
            skLineSegment(sketch, "E3.11.0.8", {"start": v(-3.3, -33.3) * mm, "end": v(-3.3, -36.7) * mm});
            skLineSegment(sketch, "E3.11.0.9", {"start": v(-6.7, 16.7) * mm, "end": v(-6.7, 13.3) * mm});
            skLineSegment(sketch, "E3.11.0.10", {"start": v(-6.7, -8.3) * mm, "end": v(-6.7, -11.7) * mm});
            skLineSegment(sketch, "E3.11.0.11", {"start": v(-6.7, -36.7) * mm, "end": v(-3.3, -36.7) * mm});
            skLineSegment(sketch, "E3.11.0.12", {"start": v(-3.3, 26.7) * mm, "end": v(-3.3, 23.3) * mm});
            skLineSegment(sketch, "E3.11.0.13", {"start": v(-3.3, -28.3) * mm, "end": v(-3.3, -31.7) * mm});
            skLineSegment(sketch, "E3.11.0.14", {"start": v(-6.7, 23.3) * mm, "end": v(-3.3, 23.3) * mm});
            skLineSegment(sketch, "E3.11.0.15", {"start": v(-3.3, 6.7) * mm, "end": v(-3.3, 3.3) * mm});
            skLineSegment(sketch, "E3.11.0.16", {"start": v(-6.7, -28.3) * mm, "end": v(-3.3, -28.3) * mm});
            skLineSegment(sketch, "E3.11.0.17", {"start": v(-6.7, 13.3) * mm, "end": v(-3.3, 13.3) * mm});
            skLineSegment(sketch, "E3.11.0.18", {"start": v(-6.7, 33.3) * mm, "end": v(-3.3, 33.3) * mm});
            skLineSegment(sketch, "E3.11.0.19", {"start": v(-6.7, 3.3) * mm, "end": v(-3.3, 3.3) * mm});
            skLineSegment(sketch, "E3.11.0.20", {"start": v(-3.3, -13.3) * mm, "end": v(-3.3, -16.7) * mm});
            skLineSegment(sketch, "E3.11.0.21", {"start": v(-3.3, 16.7) * mm, "end": v(-3.3, 13.3) * mm});
            skLineSegment(sketch, "E3.11.0.22", {"start": v(-6.7, -23.3) * mm, "end": v(-6.7, -26.7) * mm});
            skLineSegment(sketch, "E3.11.0.23", {"start": v(-6.7, -28.3) * mm, "end": v(-6.7, -31.7) * mm});
            skLineSegment(sketch, "E3.11.0.24", {"start": v(-6.7, -13.3) * mm, "end": v(-6.7, -16.7) * mm});
            skLineSegment(sketch, "E3.11.0.25", {"start": v(-6.7, -23.3) * mm, "end": v(-3.3, -23.3) * mm});
            skLineSegment(sketch, "E3.11.0.26", {"start": v(-6.7, 1.7) * mm, "end": v(-3.3, 1.7) * mm});
            skLineSegment(sketch, "E3.11.0.27", {"start": v(-3.3, -3.3) * mm, "end": v(-3.3, -6.7) * mm});
            skLineSegment(sketch, "E3.11.0.28", {"start": v(-6.7, 28.3) * mm, "end": v(-3.3, 28.3) * mm});
            skLineSegment(sketch, "E3.11.0.29", {"start": v(-6.7, 21.7) * mm, "end": v(-3.3, 21.7) * mm});
            skLineSegment(sketch, "E3.11.0.30", {"start": v(-6.7, -18.3) * mm, "end": v(-3.3, -18.3) * mm});
            skLineSegment(sketch, "E3.11.0.31", {"start": v(-6.7, -13.3) * mm, "end": v(-3.3, -13.3) * mm});
            skLineSegment(sketch, "E3.11.0.32", {"start": v(-3.3, 1.7) * mm, "end": v(-3.3, -1.7) * mm});
            skLineSegment(sketch, "E3.11.0.33", {"start": v(-3.3, 36.7) * mm, "end": v(-3.3, 33.3) * mm});
            skLineSegment(sketch, "E3.11.0.34", {"start": v(-6.7, 18.3) * mm, "end": v(-3.3, 18.3) * mm});
            skLineSegment(sketch, "E3.11.0.35", {"start": v(-3.3, -18.3) * mm, "end": v(-3.3, -21.7) * mm});
            skLineSegment(sketch, "E3.11.0.36", {"start": v(-6.7, -33.3) * mm, "end": v(-6.7, -36.7) * mm});
            skLineSegment(sketch, "E3.11.0.37", {"start": v(-6.7, -3.3) * mm, "end": v(-3.3, -3.3) * mm});
            skLineSegment(sketch, "E3.11.0.38", {"start": v(-3.3, 21.7) * mm, "end": v(-3.3, 18.3) * mm});
            skLineSegment(sketch, "E3.11.0.39", {"start": v(-3.3, -8.3) * mm, "end": v(-3.3, -11.7) * mm});
            skLineSegment(sketch, "E3.11.0.40", {"start": v(-6.7, -16.7) * mm, "end": v(-3.3, -16.7) * mm});
            skLineSegment(sketch, "E3.11.0.41", {"start": v(-6.7, -31.7) * mm, "end": v(-3.3, -31.7) * mm});
            skLineSegment(sketch, "E3.11.0.42", {"start": v(-3.3, 31.7) * mm, "end": v(-3.3, 28.3) * mm});
            skLineSegment(sketch, "E3.11.0.43", {"start": v(-6.7, 26.7) * mm, "end": v(-6.7, 23.3) * mm});
            skLineSegment(sketch, "E3.11.0.44", {"start": v(-6.7, -1.7) * mm, "end": v(-3.3, -1.7) * mm});
            skLineSegment(sketch, "E3.11.0.45", {"start": v(-6.7, -26.7) * mm, "end": v(-3.3, -26.7) * mm});
            skLineSegment(sketch, "E3.11.0.46", {"start": v(-6.7, -8.3) * mm, "end": v(-3.3, -8.3) * mm});
            skLineSegment(sketch, "E3.11.0.47", {"start": v(-3.3, 11.7) * mm, "end": v(-3.3, 8.3) * mm});
            skLineSegment(sketch, "E3.11.0.48", {"start": v(-6.7, 6.7) * mm, "end": v(-6.7, 3.3) * mm});
            skLineSegment(sketch, "E3.11.0.49", {"start": v(-6.7, 16.7) * mm, "end": v(-3.3, 16.7) * mm});
            skLineSegment(sketch, "E3.11.0.50", {"start": v(-6.7, -11.7) * mm, "end": v(-3.3, -11.7) * mm});
            skLineSegment(sketch, "E3.11.0.51", {"start": v(-6.7, 6.7) * mm, "end": v(-3.3, 6.7) * mm});
            skLineSegment(sketch, "E3.11.0.52", {"start": v(-6.7, 11.7) * mm, "end": v(-6.7, 8.3) * mm});
            skLineSegment(sketch, "E3.11.0.53", {"start": v(-6.7, 11.7) * mm, "end": v(-3.3, 11.7) * mm});
            skLineSegment(sketch, "E3.11.0.54", {"start": v(-6.7, 36.7) * mm, "end": v(-3.3, 36.7) * mm});
            skLineSegment(sketch, "E3.11.0.55", {"start": v(-3.3, -23.3) * mm, "end": v(-3.3, -26.7) * mm});
            skLineSegment(sketch, "E3.11.0.56", {"start": v(-6.7, 26.7) * mm, "end": v(-3.3, 26.7) * mm});
            skLineSegment(sketch, "E3.11.0.57", {"start": v(-6.7, 31.7) * mm, "end": v(-3.3, 31.7) * mm});
            skLineSegment(sketch, "E3.11.0.58", {"start": v(-6.7, 21.7) * mm, "end": v(-6.7, 18.3) * mm});
            skLineSegment(sketch, "E3.11.0.59", {"start": v(-6.7, -6.7) * mm, "end": v(-3.3, -6.7) * mm});
            skLineSegment(sketch, "E3.12.0.0", {"start": v(-11.7, 36.7) * mm, "end": v(-11.7, 33.3) * mm});
            skLineSegment(sketch, "E3.12.0.1", {"start": v(-11.7, -21.7) * mm, "end": v(-8.3, -21.7) * mm});
            skLineSegment(sketch, "E3.12.0.2", {"start": v(-11.7, -3.3) * mm, "end": v(-11.7, -6.7) * mm});
            skLineSegment(sketch, "E3.12.0.3", {"start": v(-11.7, 8.3) * mm, "end": v(-8.3, 8.3) * mm});
            skLineSegment(sketch, "E3.12.0.4", {"start": v(-11.7, -33.3) * mm, "end": v(-8.3, -33.3) * mm});
            skLineSegment(sketch, "E3.12.0.5", {"start": v(-11.7, 31.7) * mm, "end": v(-11.7, 28.3) * mm});
            skLineSegment(sketch, "E3.12.0.6", {"start": v(-11.7, 1.7) * mm, "end": v(-11.7, -1.7) * mm});
            skLineSegment(sketch, "E3.12.0.7", {"start": v(-11.7, -18.3) * mm, "end": v(-11.7, -21.7) * mm});
            skLineSegment(sketch, "E3.12.0.8", {"start": v(-8.3, -33.3) * mm, "end": v(-8.3, -36.7) * mm});
            skLineSegment(sketch, "E3.12.0.9", {"start": v(-11.7, 16.7) * mm, "end": v(-11.7, 13.3) * mm});
            skLineSegment(sketch, "E3.12.0.10", {"start": v(-11.7, -8.3) * mm, "end": v(-11.7, -11.7) * mm});
            skLineSegment(sketch, "E3.12.0.11", {"start": v(-11.7, -36.7) * mm, "end": v(-8.3, -36.7) * mm});
            skLineSegment(sketch, "E3.12.0.12", {"start": v(-8.3, 26.7) * mm, "end": v(-8.3, 23.3) * mm});
            skLineSegment(sketch, "E3.12.0.13", {"start": v(-8.3, -28.3) * mm, "end": v(-8.3, -31.7) * mm});
            skLineSegment(sketch, "E3.12.0.14", {"start": v(-11.7, 23.3) * mm, "end": v(-8.3, 23.3) * mm});
            skLineSegment(sketch, "E3.12.0.15", {"start": v(-8.3, 6.7) * mm, "end": v(-8.3, 3.3) * mm});
            skLineSegment(sketch, "E3.12.0.16", {"start": v(-11.7, -28.3) * mm, "end": v(-8.3, -28.3) * mm});
            skLineSegment(sketch, "E3.12.0.17", {"start": v(-11.7, 13.3) * mm, "end": v(-8.3, 13.3) * mm});
            skLineSegment(sketch, "E3.12.0.18", {"start": v(-11.7, 33.3) * mm, "end": v(-8.3, 33.3) * mm});
            skLineSegment(sketch, "E3.12.0.19", {"start": v(-11.7, 3.3) * mm, "end": v(-8.3, 3.3) * mm});
            skLineSegment(sketch, "E3.12.0.20", {"start": v(-8.3, -13.3) * mm, "end": v(-8.3, -16.7) * mm});
            skLineSegment(sketch, "E3.12.0.21", {"start": v(-8.3, 16.7) * mm, "end": v(-8.3, 13.3) * mm});
            skLineSegment(sketch, "E3.12.0.22", {"start": v(-11.7, -23.3) * mm, "end": v(-11.7, -26.7) * mm});
            skLineSegment(sketch, "E3.12.0.23", {"start": v(-11.7, -28.3) * mm, "end": v(-11.7, -31.7) * mm});
            skLineSegment(sketch, "E3.12.0.24", {"start": v(-11.7, -13.3) * mm, "end": v(-11.7, -16.7) * mm});
            skLineSegment(sketch, "E3.12.0.25", {"start": v(-11.7, -23.3) * mm, "end": v(-8.3, -23.3) * mm});
            skLineSegment(sketch, "E3.12.0.26", {"start": v(-11.7, 1.7) * mm, "end": v(-8.3, 1.7) * mm});
            skLineSegment(sketch, "E3.12.0.27", {"start": v(-8.3, -3.3) * mm, "end": v(-8.3, -6.7) * mm});
            skLineSegment(sketch, "E3.12.0.28", {"start": v(-11.7, 28.3) * mm, "end": v(-8.3, 28.3) * mm});
            skLineSegment(sketch, "E3.12.0.29", {"start": v(-11.7, 21.7) * mm, "end": v(-8.3, 21.7) * mm});
            skLineSegment(sketch, "E3.12.0.30", {"start": v(-11.7, -18.3) * mm, "end": v(-8.3, -18.3) * mm});
            skLineSegment(sketch, "E3.12.0.31", {"start": v(-11.7, -13.3) * mm, "end": v(-8.3, -13.3) * mm});
            skLineSegment(sketch, "E3.12.0.32", {"start": v(-8.3, 1.7) * mm, "end": v(-8.3, -1.7) * mm});
            skLineSegment(sketch, "E3.12.0.33", {"start": v(-8.3, 36.7) * mm, "end": v(-8.3, 33.3) * mm});
            skLineSegment(sketch, "E3.12.0.34", {"start": v(-11.7, 18.3) * mm, "end": v(-8.3, 18.3) * mm});
            skLineSegment(sketch, "E3.12.0.35", {"start": v(-8.3, -18.3) * mm, "end": v(-8.3, -21.7) * mm});
            skLineSegment(sketch, "E3.12.0.36", {"start": v(-11.7, -33.3) * mm, "end": v(-11.7, -36.7) * mm});
            skLineSegment(sketch, "E3.12.0.37", {"start": v(-11.7, -3.3) * mm, "end": v(-8.3, -3.3) * mm});
            skLineSegment(sketch, "E3.12.0.38", {"start": v(-8.3, 21.7) * mm, "end": v(-8.3, 18.3) * mm});
            skLineSegment(sketch, "E3.12.0.39", {"start": v(-8.3, -8.3) * mm, "end": v(-8.3, -11.7) * mm});
            skLineSegment(sketch, "E3.12.0.40", {"start": v(-11.7, -16.7) * mm, "end": v(-8.3, -16.7) * mm});
            skLineSegment(sketch, "E3.12.0.41", {"start": v(-11.7, -31.7) * mm, "end": v(-8.3, -31.7) * mm});
            skLineSegment(sketch, "E3.12.0.42", {"start": v(-8.3, 31.7) * mm, "end": v(-8.3, 28.3) * mm});
            skLineSegment(sketch, "E3.12.0.43", {"start": v(-11.7, 26.7) * mm, "end": v(-11.7, 23.3) * mm});
            skLineSegment(sketch, "E3.12.0.44", {"start": v(-11.7, -1.7) * mm, "end": v(-8.3, -1.7) * mm});
            skLineSegment(sketch, "E3.12.0.45", {"start": v(-11.7, -26.7) * mm, "end": v(-8.3, -26.7) * mm});
            skLineSegment(sketch, "E3.12.0.46", {"start": v(-11.7, -8.3) * mm, "end": v(-8.3, -8.3) * mm});
            skLineSegment(sketch, "E3.12.0.47", {"start": v(-8.3, 11.7) * mm, "end": v(-8.3, 8.3) * mm});
            skLineSegment(sketch, "E3.12.0.48", {"start": v(-11.7, 6.7) * mm, "end": v(-11.7, 3.3) * mm});
            skLineSegment(sketch, "E3.12.0.49", {"start": v(-11.7, 16.7) * mm, "end": v(-8.3, 16.7) * mm});
            skLineSegment(sketch, "E3.12.0.50", {"start": v(-11.7, -11.7) * mm, "end": v(-8.3, -11.7) * mm});
            skLineSegment(sketch, "E3.12.0.51", {"start": v(-11.7, 6.7) * mm, "end": v(-8.3, 6.7) * mm});
            skLineSegment(sketch, "E3.12.0.52", {"start": v(-11.7, 11.7) * mm, "end": v(-11.7, 8.3) * mm});
            skLineSegment(sketch, "E3.12.0.53", {"start": v(-11.7, 11.7) * mm, "end": v(-8.3, 11.7) * mm});
            skLineSegment(sketch, "E3.12.0.54", {"start": v(-11.7, 36.7) * mm, "end": v(-8.3, 36.7) * mm});
            skLineSegment(sketch, "E3.12.0.55", {"start": v(-8.3, -23.3) * mm, "end": v(-8.3, -26.7) * mm});
            skLineSegment(sketch, "E3.12.0.56", {"start": v(-11.7, 26.7) * mm, "end": v(-8.3, 26.7) * mm});
            skLineSegment(sketch, "E3.12.0.57", {"start": v(-11.7, 31.7) * mm, "end": v(-8.3, 31.7) * mm});
            skLineSegment(sketch, "E3.12.0.58", {"start": v(-11.7, 21.7) * mm, "end": v(-11.7, 18.3) * mm});
            skLineSegment(sketch, "E3.12.0.59", {"start": v(-11.7, -6.7) * mm, "end": v(-8.3, -6.7) * mm});
            skLineSegment(sketch, "E3.13.0.0", {"start": v(-16.7, 36.7) * mm, "end": v(-16.7, 33.3) * mm});
            skLineSegment(sketch, "E3.13.0.1", {"start": v(-16.7, -21.7) * mm, "end": v(-13.3, -21.7) * mm});
            skLineSegment(sketch, "E3.13.0.2", {"start": v(-16.7, -3.3) * mm, "end": v(-16.7, -6.7) * mm});
            skLineSegment(sketch, "E3.13.0.3", {"start": v(-16.7, 8.3) * mm, "end": v(-13.3, 8.3) * mm});
            skLineSegment(sketch, "E3.13.0.4", {"start": v(-16.7, -33.3) * mm, "end": v(-13.3, -33.3) * mm});
            skLineSegment(sketch, "E3.13.0.5", {"start": v(-16.7, 31.7) * mm, "end": v(-16.7, 28.3) * mm});
            skLineSegment(sketch, "E3.13.0.6", {"start": v(-16.7, 1.7) * mm, "end": v(-16.7, -1.7) * mm});
            skLineSegment(sketch, "E3.13.0.7", {"start": v(-16.7, -18.3) * mm, "end": v(-16.7, -21.7) * mm});
            skLineSegment(sketch, "E3.13.0.8", {"start": v(-13.3, -33.3) * mm, "end": v(-13.3, -36.7) * mm});
            skLineSegment(sketch, "E3.13.0.9", {"start": v(-16.7, 16.7) * mm, "end": v(-16.7, 13.3) * mm});
            skLineSegment(sketch, "E3.13.0.10", {"start": v(-16.7, -8.3) * mm, "end": v(-16.7, -11.7) * mm});
            skLineSegment(sketch, "E3.13.0.11", {"start": v(-16.7, -36.7) * mm, "end": v(-13.3, -36.7) * mm});
            skLineSegment(sketch, "E3.13.0.12", {"start": v(-13.3, 26.7) * mm, "end": v(-13.3, 23.3) * mm});
            skLineSegment(sketch, "E3.13.0.13", {"start": v(-13.3, -28.3) * mm, "end": v(-13.3, -31.7) * mm});
            skLineSegment(sketch, "E3.13.0.14", {"start": v(-16.7, 23.3) * mm, "end": v(-13.3, 23.3) * mm});
            skLineSegment(sketch, "E3.13.0.15", {"start": v(-13.3, 6.7) * mm, "end": v(-13.3, 3.3) * mm});
            skLineSegment(sketch, "E3.13.0.16", {"start": v(-16.7, -28.3) * mm, "end": v(-13.3, -28.3) * mm});
            skLineSegment(sketch, "E3.13.0.17", {"start": v(-16.7, 13.3) * mm, "end": v(-13.3, 13.3) * mm});
            skLineSegment(sketch, "E3.13.0.18", {"start": v(-16.7, 33.3) * mm, "end": v(-13.3, 33.3) * mm});
            skLineSegment(sketch, "E3.13.0.19", {"start": v(-16.7, 3.3) * mm, "end": v(-13.3, 3.3) * mm});
            skLineSegment(sketch, "E3.13.0.20", {"start": v(-13.3, -13.3) * mm, "end": v(-13.3, -16.7) * mm});
            skLineSegment(sketch, "E3.13.0.21", {"start": v(-13.3, 16.7) * mm, "end": v(-13.3, 13.3) * mm});
            skLineSegment(sketch, "E3.13.0.22", {"start": v(-16.7, -23.3) * mm, "end": v(-16.7, -26.7) * mm});
            skLineSegment(sketch, "E3.13.0.23", {"start": v(-16.7, -28.3) * mm, "end": v(-16.7, -31.7) * mm});
            skLineSegment(sketch, "E3.13.0.24", {"start": v(-16.7, -13.3) * mm, "end": v(-16.7, -16.7) * mm});
            skLineSegment(sketch, "E3.13.0.25", {"start": v(-16.7, -23.3) * mm, "end": v(-13.3, -23.3) * mm});
            skLineSegment(sketch, "E3.13.0.26", {"start": v(-16.7, 1.7) * mm, "end": v(-13.3, 1.7) * mm});
            skLineSegment(sketch, "E3.13.0.27", {"start": v(-13.3, -3.3) * mm, "end": v(-13.3, -6.7) * mm});
            skLineSegment(sketch, "E3.13.0.28", {"start": v(-16.7, 28.3) * mm, "end": v(-13.3, 28.3) * mm});
            skLineSegment(sketch, "E3.13.0.29", {"start": v(-16.7, 21.7) * mm, "end": v(-13.3, 21.7) * mm});
            skLineSegment(sketch, "E3.13.0.30", {"start": v(-16.7, -18.3) * mm, "end": v(-13.3, -18.3) * mm});
            skLineSegment(sketch, "E3.13.0.31", {"start": v(-16.7, -13.3) * mm, "end": v(-13.3, -13.3) * mm});
            skLineSegment(sketch, "E3.13.0.32", {"start": v(-13.3, 1.7) * mm, "end": v(-13.3, -1.7) * mm});
            skLineSegment(sketch, "E3.13.0.33", {"start": v(-13.3, 36.7) * mm, "end": v(-13.3, 33.3) * mm});
            skLineSegment(sketch, "E3.13.0.34", {"start": v(-16.7, 18.3) * mm, "end": v(-13.3, 18.3) * mm});
            skLineSegment(sketch, "E3.13.0.35", {"start": v(-13.3, -18.3) * mm, "end": v(-13.3, -21.7) * mm});
            skLineSegment(sketch, "E3.13.0.36", {"start": v(-16.7, -33.3) * mm, "end": v(-16.7, -36.7) * mm});
            skLineSegment(sketch, "E3.13.0.37", {"start": v(-16.7, -3.3) * mm, "end": v(-13.3, -3.3) * mm});
            skLineSegment(sketch, "E3.13.0.38", {"start": v(-13.3, 21.7) * mm, "end": v(-13.3, 18.3) * mm});
            skLineSegment(sketch, "E3.13.0.39", {"start": v(-13.3, -8.3) * mm, "end": v(-13.3, -11.7) * mm});
            skLineSegment(sketch, "E3.13.0.40", {"start": v(-16.7, -16.7) * mm, "end": v(-13.3, -16.7) * mm});
            skLineSegment(sketch, "E3.13.0.41", {"start": v(-16.7, -31.7) * mm, "end": v(-13.3, -31.7) * mm});
            skLineSegment(sketch, "E3.13.0.42", {"start": v(-13.3, 31.7) * mm, "end": v(-13.3, 28.3) * mm});
            skLineSegment(sketch, "E3.13.0.43", {"start": v(-16.7, 26.7) * mm, "end": v(-16.7, 23.3) * mm});
            skLineSegment(sketch, "E3.13.0.44", {"start": v(-16.7, -1.7) * mm, "end": v(-13.3, -1.7) * mm});
            skLineSegment(sketch, "E3.13.0.45", {"start": v(-16.7, -26.7) * mm, "end": v(-13.3, -26.7) * mm});
            skLineSegment(sketch, "E3.13.0.46", {"start": v(-16.7, -8.3) * mm, "end": v(-13.3, -8.3) * mm});
            skLineSegment(sketch, "E3.13.0.47", {"start": v(-13.3, 11.7) * mm, "end": v(-13.3, 8.3) * mm});
            skLineSegment(sketch, "E3.13.0.48", {"start": v(-16.7, 6.7) * mm, "end": v(-16.7, 3.3) * mm});
            skLineSegment(sketch, "E3.13.0.49", {"start": v(-16.7, 16.7) * mm, "end": v(-13.3, 16.7) * mm});
            skLineSegment(sketch, "E3.13.0.50", {"start": v(-16.7, -11.7) * mm, "end": v(-13.3, -11.7) * mm});
            skLineSegment(sketch, "E3.13.0.51", {"start": v(-16.7, 6.7) * mm, "end": v(-13.3, 6.7) * mm});
            skLineSegment(sketch, "E3.13.0.52", {"start": v(-16.7, 11.7) * mm, "end": v(-16.7, 8.3) * mm});
            skLineSegment(sketch, "E3.13.0.53", {"start": v(-16.7, 11.7) * mm, "end": v(-13.3, 11.7) * mm});
            skLineSegment(sketch, "E3.13.0.54", {"start": v(-16.7, 36.7) * mm, "end": v(-13.3, 36.7) * mm});
            skLineSegment(sketch, "E3.13.0.55", {"start": v(-13.3, -23.3) * mm, "end": v(-13.3, -26.7) * mm});
            skLineSegment(sketch, "E3.13.0.56", {"start": v(-16.7, 26.7) * mm, "end": v(-13.3, 26.7) * mm});
            skLineSegment(sketch, "E3.13.0.57", {"start": v(-16.7, 31.7) * mm, "end": v(-13.3, 31.7) * mm});
            skLineSegment(sketch, "E3.13.0.58", {"start": v(-16.7, 21.7) * mm, "end": v(-16.7, 18.3) * mm});
            skLineSegment(sketch, "E3.13.0.59", {"start": v(-16.7, -6.7) * mm, "end": v(-13.3, -6.7) * mm});
            skLineSegment(sketch, "E3.14.0.0", {"start": v(-21.7, 36.7) * mm, "end": v(-21.7, 33.3) * mm});
            skLineSegment(sketch, "E3.14.0.1", {"start": v(-21.7, -21.7) * mm, "end": v(-18.3, -21.7) * mm});
            skLineSegment(sketch, "E3.14.0.2", {"start": v(-21.7, -3.3) * mm, "end": v(-21.7, -6.7) * mm});
            skLineSegment(sketch, "E3.14.0.3", {"start": v(-21.7, 8.3) * mm, "end": v(-18.3, 8.3) * mm});
            skLineSegment(sketch, "E3.14.0.4", {"start": v(-21.7, -33.3) * mm, "end": v(-18.3, -33.3) * mm});
            skLineSegment(sketch, "E3.14.0.5", {"start": v(-21.7, 31.7) * mm, "end": v(-21.7, 28.3) * mm});
            skLineSegment(sketch, "E3.14.0.6", {"start": v(-21.7, 1.7) * mm, "end": v(-21.7, -1.7) * mm});
            skLineSegment(sketch, "E3.14.0.7", {"start": v(-21.7, -18.3) * mm, "end": v(-21.7, -21.7) * mm});
            skLineSegment(sketch, "E3.14.0.8", {"start": v(-18.3, -33.3) * mm, "end": v(-18.3, -36.7) * mm});
            skLineSegment(sketch, "E3.14.0.9", {"start": v(-21.7, 16.7) * mm, "end": v(-21.7, 13.3) * mm});
            skLineSegment(sketch, "E3.14.0.10", {"start": v(-21.7, -8.3) * mm, "end": v(-21.7, -11.7) * mm});
            skLineSegment(sketch, "E3.14.0.11", {"start": v(-21.7, -36.7) * mm, "end": v(-18.3, -36.7) * mm});
            skLineSegment(sketch, "E3.14.0.12", {"start": v(-18.3, 26.7) * mm, "end": v(-18.3, 23.3) * mm});
            skLineSegment(sketch, "E3.14.0.13", {"start": v(-18.3, -28.3) * mm, "end": v(-18.3, -31.7) * mm});
            skLineSegment(sketch, "E3.14.0.14", {"start": v(-21.7, 23.3) * mm, "end": v(-18.3, 23.3) * mm});
            skLineSegment(sketch, "E3.14.0.15", {"start": v(-18.3, 6.7) * mm, "end": v(-18.3, 3.3) * mm});
            skLineSegment(sketch, "E3.14.0.16", {"start": v(-21.7, -28.3) * mm, "end": v(-18.3, -28.3) * mm});
            skLineSegment(sketch, "E3.14.0.17", {"start": v(-21.7, 13.3) * mm, "end": v(-18.3, 13.3) * mm});
            skLineSegment(sketch, "E3.14.0.18", {"start": v(-21.7, 33.3) * mm, "end": v(-18.3, 33.3) * mm});
            skLineSegment(sketch, "E3.14.0.19", {"start": v(-21.7, 3.3) * mm, "end": v(-18.3, 3.3) * mm});
            skLineSegment(sketch, "E3.14.0.20", {"start": v(-18.3, -13.3) * mm, "end": v(-18.3, -16.7) * mm});
            skLineSegment(sketch, "E3.14.0.21", {"start": v(-18.3, 16.7) * mm, "end": v(-18.3, 13.3) * mm});
            skLineSegment(sketch, "E3.14.0.22", {"start": v(-21.7, -23.3) * mm, "end": v(-21.7, -26.7) * mm});
            skLineSegment(sketch, "E3.14.0.23", {"start": v(-21.7, -28.3) * mm, "end": v(-21.7, -31.7) * mm});
            skLineSegment(sketch, "E3.14.0.24", {"start": v(-21.7, -13.3) * mm, "end": v(-21.7, -16.7) * mm});
            skLineSegment(sketch, "E3.14.0.25", {"start": v(-21.7, -23.3) * mm, "end": v(-18.3, -23.3) * mm});
            skLineSegment(sketch, "E3.14.0.26", {"start": v(-21.7, 1.7) * mm, "end": v(-18.3, 1.7) * mm});
            skLineSegment(sketch, "E3.14.0.27", {"start": v(-18.3, -3.3) * mm, "end": v(-18.3, -6.7) * mm});
            skLineSegment(sketch, "E3.14.0.28", {"start": v(-21.7, 28.3) * mm, "end": v(-18.3, 28.3) * mm});
            skLineSegment(sketch, "E3.14.0.29", {"start": v(-21.7, 21.7) * mm, "end": v(-18.3, 21.7) * mm});
            skLineSegment(sketch, "E3.14.0.30", {"start": v(-21.7, -18.3) * mm, "end": v(-18.3, -18.3) * mm});
            skLineSegment(sketch, "E3.14.0.31", {"start": v(-21.7, -13.3) * mm, "end": v(-18.3, -13.3) * mm});
            skLineSegment(sketch, "E3.14.0.32", {"start": v(-18.3, 1.7) * mm, "end": v(-18.3, -1.7) * mm});
            skLineSegment(sketch, "E3.14.0.33", {"start": v(-18.3, 36.7) * mm, "end": v(-18.3, 33.3) * mm});
            skLineSegment(sketch, "E3.14.0.34", {"start": v(-21.7, 18.3) * mm, "end": v(-18.3, 18.3) * mm});
            skLineSegment(sketch, "E3.14.0.35", {"start": v(-18.3, -18.3) * mm, "end": v(-18.3, -21.7) * mm});
            skLineSegment(sketch, "E3.14.0.36", {"start": v(-21.7, -33.3) * mm, "end": v(-21.7, -36.7) * mm});
            skLineSegment(sketch, "E3.14.0.37", {"start": v(-21.7, -3.3) * mm, "end": v(-18.3, -3.3) * mm});
            skLineSegment(sketch, "E3.14.0.38", {"start": v(-18.3, 21.7) * mm, "end": v(-18.3, 18.3) * mm});
            skLineSegment(sketch, "E3.14.0.39", {"start": v(-18.3, -8.3) * mm, "end": v(-18.3, -11.7) * mm});
            skLineSegment(sketch, "E3.14.0.40", {"start": v(-21.7, -16.7) * mm, "end": v(-18.3, -16.7) * mm});
            skLineSegment(sketch, "E3.14.0.41", {"start": v(-21.7, -31.7) * mm, "end": v(-18.3, -31.7) * mm});
            skLineSegment(sketch, "E3.14.0.42", {"start": v(-18.3, 31.7) * mm, "end": v(-18.3, 28.3) * mm});
            skLineSegment(sketch, "E3.14.0.43", {"start": v(-21.7, 26.7) * mm, "end": v(-21.7, 23.3) * mm});
            skLineSegment(sketch, "E3.14.0.44", {"start": v(-21.7, -1.7) * mm, "end": v(-18.3, -1.7) * mm});
            skLineSegment(sketch, "E3.14.0.45", {"start": v(-21.7, -26.7) * mm, "end": v(-18.3, -26.7) * mm});
            skLineSegment(sketch, "E3.14.0.46", {"start": v(-21.7, -8.3) * mm, "end": v(-18.3, -8.3) * mm});
            skLineSegment(sketch, "E3.14.0.47", {"start": v(-18.3, 11.7) * mm, "end": v(-18.3, 8.3) * mm});
            skLineSegment(sketch, "E3.14.0.48", {"start": v(-21.7, 6.7) * mm, "end": v(-21.7, 3.3) * mm});
            skLineSegment(sketch, "E3.14.0.49", {"start": v(-21.7, 16.7) * mm, "end": v(-18.3, 16.7) * mm});
            skLineSegment(sketch, "E3.14.0.50", {"start": v(-21.7, -11.7) * mm, "end": v(-18.3, -11.7) * mm});
            skLineSegment(sketch, "E3.14.0.51", {"start": v(-21.7, 6.7) * mm, "end": v(-18.3, 6.7) * mm});
            skLineSegment(sketch, "E3.14.0.52", {"start": v(-21.7, 11.7) * mm, "end": v(-21.7, 8.3) * mm});
            skLineSegment(sketch, "E3.14.0.53", {"start": v(-21.7, 11.7) * mm, "end": v(-18.3, 11.7) * mm});
            skLineSegment(sketch, "E3.14.0.54", {"start": v(-21.7, 36.7) * mm, "end": v(-18.3, 36.7) * mm});
            skLineSegment(sketch, "E3.14.0.55", {"start": v(-18.3, -23.3) * mm, "end": v(-18.3, -26.7) * mm});
            skLineSegment(sketch, "E3.14.0.56", {"start": v(-21.7, 26.7) * mm, "end": v(-18.3, 26.7) * mm});
            skLineSegment(sketch, "E3.14.0.57", {"start": v(-21.7, 31.7) * mm, "end": v(-18.3, 31.7) * mm});
            skLineSegment(sketch, "E3.14.0.58", {"start": v(-21.7, 21.7) * mm, "end": v(-21.7, 18.3) * mm});
            skLineSegment(sketch, "E3.14.0.59", {"start": v(-21.7, -6.7) * mm, "end": v(-18.3, -6.7) * mm});
            skLineSegment(sketch, "E3.15.0.0", {"start": v(-26.7, 36.7) * mm, "end": v(-26.7, 33.3) * mm});
            skLineSegment(sketch, "E3.15.0.1", {"start": v(-26.7, -21.7) * mm, "end": v(-23.3, -21.7) * mm});
            skLineSegment(sketch, "E3.15.0.2", {"start": v(-26.7, -3.3) * mm, "end": v(-26.7, -6.7) * mm});
            skLineSegment(sketch, "E3.15.0.3", {"start": v(-26.7, 8.3) * mm, "end": v(-23.3, 8.3) * mm});
            skLineSegment(sketch, "E3.15.0.4", {"start": v(-26.7, -33.3) * mm, "end": v(-23.3, -33.3) * mm});
            skLineSegment(sketch, "E3.15.0.5", {"start": v(-26.7, 31.7) * mm, "end": v(-26.7, 28.3) * mm});
            skLineSegment(sketch, "E3.15.0.6", {"start": v(-26.7, 1.7) * mm, "end": v(-26.7, -1.7) * mm});
            skLineSegment(sketch, "E3.15.0.7", {"start": v(-26.7, -18.3) * mm, "end": v(-26.7, -21.7) * mm});
            skLineSegment(sketch, "E3.15.0.8", {"start": v(-23.3, -33.3) * mm, "end": v(-23.3, -36.7) * mm});
            skLineSegment(sketch, "E3.15.0.9", {"start": v(-26.7, 16.7) * mm, "end": v(-26.7, 13.3) * mm});
            skLineSegment(sketch, "E3.15.0.10", {"start": v(-26.7, -8.3) * mm, "end": v(-26.7, -11.7) * mm});
            skLineSegment(sketch, "E3.15.0.11", {"start": v(-26.7, -36.7) * mm, "end": v(-23.3, -36.7) * mm});
            skLineSegment(sketch, "E3.15.0.12", {"start": v(-23.3, 26.7) * mm, "end": v(-23.3, 23.3) * mm});
            skLineSegment(sketch, "E3.15.0.13", {"start": v(-23.3, -28.3) * mm, "end": v(-23.3, -31.7) * mm});
            skLineSegment(sketch, "E3.15.0.14", {"start": v(-26.7, 23.3) * mm, "end": v(-23.3, 23.3) * mm});
            skLineSegment(sketch, "E3.15.0.15", {"start": v(-23.3, 6.7) * mm, "end": v(-23.3, 3.3) * mm});
            skLineSegment(sketch, "E3.15.0.16", {"start": v(-26.7, -28.3) * mm, "end": v(-23.3, -28.3) * mm});
            skLineSegment(sketch, "E3.15.0.17", {"start": v(-26.7, 13.3) * mm, "end": v(-23.3, 13.3) * mm});
            skLineSegment(sketch, "E3.15.0.18", {"start": v(-26.7, 33.3) * mm, "end": v(-23.3, 33.3) * mm});
            skLineSegment(sketch, "E3.15.0.19", {"start": v(-26.7, 3.3) * mm, "end": v(-23.3, 3.3) * mm});
            skLineSegment(sketch, "E3.15.0.20", {"start": v(-23.3, -13.3) * mm, "end": v(-23.3, -16.7) * mm});
            skLineSegment(sketch, "E3.15.0.21", {"start": v(-23.3, 16.7) * mm, "end": v(-23.3, 13.3) * mm});
            skLineSegment(sketch, "E3.15.0.22", {"start": v(-26.7, -23.3) * mm, "end": v(-26.7, -26.7) * mm});
            skLineSegment(sketch, "E3.15.0.23", {"start": v(-26.7, -28.3) * mm, "end": v(-26.7, -31.7) * mm});
            skLineSegment(sketch, "E3.15.0.24", {"start": v(-26.7, -13.3) * mm, "end": v(-26.7, -16.7) * mm});
            skLineSegment(sketch, "E3.15.0.25", {"start": v(-26.7, -23.3) * mm, "end": v(-23.3, -23.3) * mm});
            skLineSegment(sketch, "E3.15.0.26", {"start": v(-26.7, 1.7) * mm, "end": v(-23.3, 1.7) * mm});
            skLineSegment(sketch, "E3.15.0.27", {"start": v(-23.3, -3.3) * mm, "end": v(-23.3, -6.7) * mm});
            skLineSegment(sketch, "E3.15.0.28", {"start": v(-26.7, 28.3) * mm, "end": v(-23.3, 28.3) * mm});
            skLineSegment(sketch, "E3.15.0.29", {"start": v(-26.7, 21.7) * mm, "end": v(-23.3, 21.7) * mm});
            skLineSegment(sketch, "E3.15.0.30", {"start": v(-26.7, -18.3) * mm, "end": v(-23.3, -18.3) * mm});
            skLineSegment(sketch, "E3.15.0.31", {"start": v(-26.7, -13.3) * mm, "end": v(-23.3, -13.3) * mm});
            skLineSegment(sketch, "E3.15.0.32", {"start": v(-23.3, 1.7) * mm, "end": v(-23.3, -1.7) * mm});
            skLineSegment(sketch, "E3.15.0.33", {"start": v(-23.3, 36.7) * mm, "end": v(-23.3, 33.3) * mm});
            skLineSegment(sketch, "E3.15.0.34", {"start": v(-26.7, 18.3) * mm, "end": v(-23.3, 18.3) * mm});
            skLineSegment(sketch, "E3.15.0.35", {"start": v(-23.3, -18.3) * mm, "end": v(-23.3, -21.7) * mm});
            skLineSegment(sketch, "E3.15.0.36", {"start": v(-26.7, -33.3) * mm, "end": v(-26.7, -36.7) * mm});
            skLineSegment(sketch, "E3.15.0.37", {"start": v(-26.7, -3.3) * mm, "end": v(-23.3, -3.3) * mm});
            skLineSegment(sketch, "E3.15.0.38", {"start": v(-23.3, 21.7) * mm, "end": v(-23.3, 18.3) * mm});
            skLineSegment(sketch, "E3.15.0.39", {"start": v(-23.3, -8.3) * mm, "end": v(-23.3, -11.7) * mm});
            skLineSegment(sketch, "E3.15.0.40", {"start": v(-26.7, -16.7) * mm, "end": v(-23.3, -16.7) * mm});
            skLineSegment(sketch, "E3.15.0.41", {"start": v(-26.7, -31.7) * mm, "end": v(-23.3, -31.7) * mm});
            skLineSegment(sketch, "E3.15.0.42", {"start": v(-23.3, 31.7) * mm, "end": v(-23.3, 28.3) * mm});
            skLineSegment(sketch, "E3.15.0.43", {"start": v(-26.7, 26.7) * mm, "end": v(-26.7, 23.3) * mm});
            skLineSegment(sketch, "E3.15.0.44", {"start": v(-26.7, -1.7) * mm, "end": v(-23.3, -1.7) * mm});
            skLineSegment(sketch, "E3.15.0.45", {"start": v(-26.7, -26.7) * mm, "end": v(-23.3, -26.7) * mm});
            skLineSegment(sketch, "E3.15.0.46", {"start": v(-26.7, -8.3) * mm, "end": v(-23.3, -8.3) * mm});
            skLineSegment(sketch, "E3.15.0.47", {"start": v(-23.3, 11.7) * mm, "end": v(-23.3, 8.3) * mm});
            skLineSegment(sketch, "E3.15.0.48", {"start": v(-26.7, 6.7) * mm, "end": v(-26.7, 3.3) * mm});
            skLineSegment(sketch, "E3.15.0.49", {"start": v(-26.7, 16.7) * mm, "end": v(-23.3, 16.7) * mm});
            skLineSegment(sketch, "E3.15.0.50", {"start": v(-26.7, -11.7) * mm, "end": v(-23.3, -11.7) * mm});
            skLineSegment(sketch, "E3.15.0.51", {"start": v(-26.7, 6.7) * mm, "end": v(-23.3, 6.7) * mm});
            skLineSegment(sketch, "E3.15.0.52", {"start": v(-26.7, 11.7) * mm, "end": v(-26.7, 8.3) * mm});
            skLineSegment(sketch, "E3.15.0.53", {"start": v(-26.7, 11.7) * mm, "end": v(-23.3, 11.7) * mm});
            skLineSegment(sketch, "E3.15.0.54", {"start": v(-26.7, 36.7) * mm, "end": v(-23.3, 36.7) * mm});
            skLineSegment(sketch, "E3.15.0.55", {"start": v(-23.3, -23.3) * mm, "end": v(-23.3, -26.7) * mm});
            skLineSegment(sketch, "E3.15.0.56", {"start": v(-26.7, 26.7) * mm, "end": v(-23.3, 26.7) * mm});
            skLineSegment(sketch, "E3.15.0.57", {"start": v(-26.7, 31.7) * mm, "end": v(-23.3, 31.7) * mm});
            skLineSegment(sketch, "E3.15.0.58", {"start": v(-26.7, 21.7) * mm, "end": v(-26.7, 18.3) * mm});
            skLineSegment(sketch, "E3.15.0.59", {"start": v(-26.7, -6.7) * mm, "end": v(-23.3, -6.7) * mm});
            skLineSegment(sketch, "E3.16.0.0", {"start": v(-31.7, 36.7) * mm, "end": v(-31.7, 33.3) * mm});
            skLineSegment(sketch, "E3.16.0.1", {"start": v(-31.7, -21.7) * mm, "end": v(-28.3, -21.7) * mm});
            skLineSegment(sketch, "E3.16.0.2", {"start": v(-31.7, -3.3) * mm, "end": v(-31.7, -6.7) * mm});
            skLineSegment(sketch, "E3.16.0.3", {"start": v(-31.7, 8.3) * mm, "end": v(-28.3, 8.3) * mm});
            skLineSegment(sketch, "E3.16.0.4", {"start": v(-31.7, -33.3) * mm, "end": v(-28.3, -33.3) * mm});
            skLineSegment(sketch, "E3.16.0.5", {"start": v(-31.7, 31.7) * mm, "end": v(-31.7, 28.3) * mm});
            skLineSegment(sketch, "E3.16.0.6", {"start": v(-31.7, 1.7) * mm, "end": v(-31.7, -1.7) * mm});
            skLineSegment(sketch, "E3.16.0.7", {"start": v(-31.7, -18.3) * mm, "end": v(-31.7, -21.7) * mm});
            skLineSegment(sketch, "E3.16.0.8", {"start": v(-28.3, -33.3) * mm, "end": v(-28.3, -36.7) * mm});
            skLineSegment(sketch, "E3.16.0.9", {"start": v(-31.7, 16.7) * mm, "end": v(-31.7, 13.3) * mm});
            skLineSegment(sketch, "E3.16.0.10", {"start": v(-31.7, -8.3) * mm, "end": v(-31.7, -11.7) * mm});
            skLineSegment(sketch, "E3.16.0.11", {"start": v(-31.7, -36.7) * mm, "end": v(-28.3, -36.7) * mm});
            skLineSegment(sketch, "E3.16.0.12", {"start": v(-28.3, 26.7) * mm, "end": v(-28.3, 23.3) * mm});
            skLineSegment(sketch, "E3.16.0.13", {"start": v(-28.3, -28.3) * mm, "end": v(-28.3, -31.7) * mm});
            skLineSegment(sketch, "E3.16.0.14", {"start": v(-31.7, 23.3) * mm, "end": v(-28.3, 23.3) * mm});
            skLineSegment(sketch, "E3.16.0.15", {"start": v(-28.3, 6.7) * mm, "end": v(-28.3, 3.3) * mm});
            skLineSegment(sketch, "E3.16.0.16", {"start": v(-31.7, -28.3) * mm, "end": v(-28.3, -28.3) * mm});
            skLineSegment(sketch, "E3.16.0.17", {"start": v(-31.7, 13.3) * mm, "end": v(-28.3, 13.3) * mm});
            skLineSegment(sketch, "E3.16.0.18", {"start": v(-31.7, 33.3) * mm, "end": v(-28.3, 33.3) * mm});
            skLineSegment(sketch, "E3.16.0.19", {"start": v(-31.7, 3.3) * mm, "end": v(-28.3, 3.3) * mm});
            skLineSegment(sketch, "E3.16.0.20", {"start": v(-28.3, -13.3) * mm, "end": v(-28.3, -16.7) * mm});
            skLineSegment(sketch, "E3.16.0.21", {"start": v(-28.3, 16.7) * mm, "end": v(-28.3, 13.3) * mm});
            skLineSegment(sketch, "E3.16.0.22", {"start": v(-31.7, -23.3) * mm, "end": v(-31.7, -26.7) * mm});
            skLineSegment(sketch, "E3.16.0.23", {"start": v(-31.7, -28.3) * mm, "end": v(-31.7, -31.7) * mm});
            skLineSegment(sketch, "E3.16.0.24", {"start": v(-31.7, -13.3) * mm, "end": v(-31.7, -16.7) * mm});
            skLineSegment(sketch, "E3.16.0.25", {"start": v(-31.7, -23.3) * mm, "end": v(-28.3, -23.3) * mm});
            skLineSegment(sketch, "E3.16.0.26", {"start": v(-31.7, 1.7) * mm, "end": v(-28.3, 1.7) * mm});
            skLineSegment(sketch, "E3.16.0.27", {"start": v(-28.3, -3.3) * mm, "end": v(-28.3, -6.7) * mm});
            skLineSegment(sketch, "E3.16.0.28", {"start": v(-31.7, 28.3) * mm, "end": v(-28.3, 28.3) * mm});
            skLineSegment(sketch, "E3.16.0.29", {"start": v(-31.7, 21.7) * mm, "end": v(-28.3, 21.7) * mm});
            skLineSegment(sketch, "E3.16.0.30", {"start": v(-31.7, -18.3) * mm, "end": v(-28.3, -18.3) * mm});
            skLineSegment(sketch, "E3.16.0.31", {"start": v(-31.7, -13.3) * mm, "end": v(-28.3, -13.3) * mm});
            skLineSegment(sketch, "E3.16.0.32", {"start": v(-28.3, 1.7) * mm, "end": v(-28.3, -1.7) * mm});
            skLineSegment(sketch, "E3.16.0.33", {"start": v(-28.3, 36.7) * mm, "end": v(-28.3, 33.3) * mm});
            skLineSegment(sketch, "E3.16.0.34", {"start": v(-31.7, 18.3) * mm, "end": v(-28.3, 18.3) * mm});
            skLineSegment(sketch, "E3.16.0.35", {"start": v(-28.3, -18.3) * mm, "end": v(-28.3, -21.7) * mm});
            skLineSegment(sketch, "E3.16.0.36", {"start": v(-31.7, -33.3) * mm, "end": v(-31.7, -36.7) * mm});
            skLineSegment(sketch, "E3.16.0.37", {"start": v(-31.7, -3.3) * mm, "end": v(-28.3, -3.3) * mm});
            skLineSegment(sketch, "E3.16.0.38", {"start": v(-28.3, 21.7) * mm, "end": v(-28.3, 18.3) * mm});
            skLineSegment(sketch, "E3.16.0.39", {"start": v(-28.3, -8.3) * mm, "end": v(-28.3, -11.7) * mm});
            skLineSegment(sketch, "E3.16.0.40", {"start": v(-31.7, -16.7) * mm, "end": v(-28.3, -16.7) * mm});
            skLineSegment(sketch, "E3.16.0.41", {"start": v(-31.7, -31.7) * mm, "end": v(-28.3, -31.7) * mm});
            skLineSegment(sketch, "E3.16.0.42", {"start": v(-28.3, 31.7) * mm, "end": v(-28.3, 28.3) * mm});
            skLineSegment(sketch, "E3.16.0.43", {"start": v(-31.7, 26.7) * mm, "end": v(-31.7, 23.3) * mm});
            skLineSegment(sketch, "E3.16.0.44", {"start": v(-31.7, -1.7) * mm, "end": v(-28.3, -1.7) * mm});
            skLineSegment(sketch, "E3.16.0.45", {"start": v(-31.7, -26.7) * mm, "end": v(-28.3, -26.7) * mm});
            skLineSegment(sketch, "E3.16.0.46", {"start": v(-31.7, -8.3) * mm, "end": v(-28.3, -8.3) * mm});
            skLineSegment(sketch, "E3.16.0.47", {"start": v(-28.3, 11.7) * mm, "end": v(-28.3, 8.3) * mm});
            skLineSegment(sketch, "E3.16.0.48", {"start": v(-31.7, 6.7) * mm, "end": v(-31.7, 3.3) * mm});
            skLineSegment(sketch, "E3.16.0.49", {"start": v(-31.7, 16.7) * mm, "end": v(-28.3, 16.7) * mm});
            skLineSegment(sketch, "E3.16.0.50", {"start": v(-31.7, -11.7) * mm, "end": v(-28.3, -11.7) * mm});
            skLineSegment(sketch, "E3.16.0.51", {"start": v(-31.7, 6.7) * mm, "end": v(-28.3, 6.7) * mm});
            skLineSegment(sketch, "E3.16.0.52", {"start": v(-31.7, 11.7) * mm, "end": v(-31.7, 8.3) * mm});
            skLineSegment(sketch, "E3.16.0.53", {"start": v(-31.7, 11.7) * mm, "end": v(-28.3, 11.7) * mm});
            skLineSegment(sketch, "E3.16.0.54", {"start": v(-31.7, 36.7) * mm, "end": v(-28.3, 36.7) * mm});
            skLineSegment(sketch, "E3.16.0.55", {"start": v(-28.3, -23.3) * mm, "end": v(-28.3, -26.7) * mm});
            skLineSegment(sketch, "E3.16.0.56", {"start": v(-31.7, 26.7) * mm, "end": v(-28.3, 26.7) * mm});
            skLineSegment(sketch, "E3.16.0.57", {"start": v(-31.7, 31.7) * mm, "end": v(-28.3, 31.7) * mm});
            skLineSegment(sketch, "E3.16.0.58", {"start": v(-31.7, 21.7) * mm, "end": v(-31.7, 18.3) * mm});
            skLineSegment(sketch, "E3.16.0.59", {"start": v(-31.7, -6.7) * mm, "end": v(-28.3, -6.7) * mm});
            skLineSegment(sketch, "E3.17.0.0", {"start": v(-36.7, 36.7) * mm, "end": v(-36.7, 33.3) * mm});
            skLineSegment(sketch, "E3.17.0.1", {"start": v(-36.7, -21.7) * mm, "end": v(-33.3, -21.7) * mm});
            skLineSegment(sketch, "E3.17.0.2", {"start": v(-36.7, -3.3) * mm, "end": v(-36.7, -6.7) * mm});
            skLineSegment(sketch, "E3.17.0.3", {"start": v(-36.7, 8.3) * mm, "end": v(-33.3, 8.3) * mm});
            skLineSegment(sketch, "E3.17.0.4", {"start": v(-36.7, -33.3) * mm, "end": v(-33.3, -33.3) * mm});
            skLineSegment(sketch, "E3.17.0.5", {"start": v(-36.7, 31.7) * mm, "end": v(-36.7, 28.3) * mm});
            skLineSegment(sketch, "E3.17.0.6", {"start": v(-36.7, 1.7) * mm, "end": v(-36.7, -1.7) * mm});
            skLineSegment(sketch, "E3.17.0.7", {"start": v(-36.7, -18.3) * mm, "end": v(-36.7, -21.7) * mm});
            skLineSegment(sketch, "E3.17.0.8", {"start": v(-33.3, -33.3) * mm, "end": v(-33.3, -36.7) * mm});
            skLineSegment(sketch, "E3.17.0.9", {"start": v(-36.7, 16.7) * mm, "end": v(-36.7, 13.3) * mm});
            skLineSegment(sketch, "E3.17.0.10", {"start": v(-36.7, -8.3) * mm, "end": v(-36.7, -11.7) * mm});
            skLineSegment(sketch, "E3.17.0.11", {"start": v(-36.7, -36.7) * mm, "end": v(-33.3, -36.7) * mm});
            skLineSegment(sketch, "E3.17.0.12", {"start": v(-33.3, 26.7) * mm, "end": v(-33.3, 23.3) * mm});
            skLineSegment(sketch, "E3.17.0.13", {"start": v(-33.3, -28.3) * mm, "end": v(-33.3, -31.7) * mm});
            skLineSegment(sketch, "E3.17.0.14", {"start": v(-36.7, 23.3) * mm, "end": v(-33.3, 23.3) * mm});
            skLineSegment(sketch, "E3.17.0.15", {"start": v(-33.3, 6.7) * mm, "end": v(-33.3, 3.3) * mm});
            skLineSegment(sketch, "E3.17.0.16", {"start": v(-36.7, -28.3) * mm, "end": v(-33.3, -28.3) * mm});
            skLineSegment(sketch, "E3.17.0.17", {"start": v(-36.7, 13.3) * mm, "end": v(-33.3, 13.3) * mm});
            skLineSegment(sketch, "E3.17.0.18", {"start": v(-36.7, 33.3) * mm, "end": v(-33.3, 33.3) * mm});
            skLineSegment(sketch, "E3.17.0.19", {"start": v(-36.7, 3.3) * mm, "end": v(-33.3, 3.3) * mm});
            skLineSegment(sketch, "E3.17.0.20", {"start": v(-33.3, -13.3) * mm, "end": v(-33.3, -16.7) * mm});
            skLineSegment(sketch, "E3.17.0.21", {"start": v(-33.3, 16.7) * mm, "end": v(-33.3, 13.3) * mm});
            skLineSegment(sketch, "E3.17.0.22", {"start": v(-36.7, -23.3) * mm, "end": v(-36.7, -26.7) * mm});
            skLineSegment(sketch, "E3.17.0.23", {"start": v(-36.7, -28.3) * mm, "end": v(-36.7, -31.7) * mm});
            skLineSegment(sketch, "E3.17.0.24", {"start": v(-36.7, -13.3) * mm, "end": v(-36.7, -16.7) * mm});
            skLineSegment(sketch, "E3.17.0.25", {"start": v(-36.7, -23.3) * mm, "end": v(-33.3, -23.3) * mm});
            skLineSegment(sketch, "E3.17.0.26", {"start": v(-36.7, 1.7) * mm, "end": v(-33.3, 1.7) * mm});
            skLineSegment(sketch, "E3.17.0.27", {"start": v(-33.3, -3.3) * mm, "end": v(-33.3, -6.7) * mm});
            skLineSegment(sketch, "E3.17.0.28", {"start": v(-36.7, 28.3) * mm, "end": v(-33.3, 28.3) * mm});
            skLineSegment(sketch, "E3.17.0.29", {"start": v(-36.7, 21.7) * mm, "end": v(-33.3, 21.7) * mm});
            skLineSegment(sketch, "E3.17.0.30", {"start": v(-36.7, -18.3) * mm, "end": v(-33.3, -18.3) * mm});
            skLineSegment(sketch, "E3.17.0.31", {"start": v(-36.7, -13.3) * mm, "end": v(-33.3, -13.3) * mm});
            skLineSegment(sketch, "E3.17.0.32", {"start": v(-33.3, 1.7) * mm, "end": v(-33.3, -1.7) * mm});
            skLineSegment(sketch, "E3.17.0.33", {"start": v(-33.3, 36.7) * mm, "end": v(-33.3, 33.3) * mm});
            skLineSegment(sketch, "E3.17.0.34", {"start": v(-36.7, 18.3) * mm, "end": v(-33.3, 18.3) * mm});
            skLineSegment(sketch, "E3.17.0.35", {"start": v(-33.3, -18.3) * mm, "end": v(-33.3, -21.7) * mm});
            skLineSegment(sketch, "E3.17.0.36", {"start": v(-36.7, -33.3) * mm, "end": v(-36.7, -36.7) * mm});
            skLineSegment(sketch, "E3.17.0.37", {"start": v(-36.7, -3.3) * mm, "end": v(-33.3, -3.3) * mm});
            skLineSegment(sketch, "E3.17.0.38", {"start": v(-33.3, 21.7) * mm, "end": v(-33.3, 18.3) * mm});
            skLineSegment(sketch, "E3.17.0.39", {"start": v(-33.3, -8.3) * mm, "end": v(-33.3, -11.7) * mm});
            skLineSegment(sketch, "E3.17.0.40", {"start": v(-36.7, -16.7) * mm, "end": v(-33.3, -16.7) * mm});
            skLineSegment(sketch, "E3.17.0.41", {"start": v(-36.7, -31.7) * mm, "end": v(-33.3, -31.7) * mm});
            skLineSegment(sketch, "E3.17.0.42", {"start": v(-33.3, 31.7) * mm, "end": v(-33.3, 28.3) * mm});
            skLineSegment(sketch, "E3.17.0.43", {"start": v(-36.7, 26.7) * mm, "end": v(-36.7, 23.3) * mm});
            skLineSegment(sketch, "E3.17.0.44", {"start": v(-36.7, -1.7) * mm, "end": v(-33.3, -1.7) * mm});
            skLineSegment(sketch, "E3.17.0.45", {"start": v(-36.7, -26.7) * mm, "end": v(-33.3, -26.7) * mm});
            skLineSegment(sketch, "E3.17.0.46", {"start": v(-36.7, -8.3) * mm, "end": v(-33.3, -8.3) * mm});
            skLineSegment(sketch, "E3.17.0.47", {"start": v(-33.3, 11.7) * mm, "end": v(-33.3, 8.3) * mm});
            skLineSegment(sketch, "E3.17.0.48", {"start": v(-36.7, 6.7) * mm, "end": v(-36.7, 3.3) * mm});
            skLineSegment(sketch, "E3.17.0.49", {"start": v(-36.7, 16.7) * mm, "end": v(-33.3, 16.7) * mm});
            skLineSegment(sketch, "E3.17.0.50", {"start": v(-36.7, -11.7) * mm, "end": v(-33.3, -11.7) * mm});
            skLineSegment(sketch, "E3.17.0.51", {"start": v(-36.7, 6.7) * mm, "end": v(-33.3, 6.7) * mm});
            skLineSegment(sketch, "E3.17.0.52", {"start": v(-36.7, 11.7) * mm, "end": v(-36.7, 8.3) * mm});
            skLineSegment(sketch, "E3.17.0.53", {"start": v(-36.7, 11.7) * mm, "end": v(-33.3, 11.7) * mm});
            skLineSegment(sketch, "E3.17.0.54", {"start": v(-36.7, 36.7) * mm, "end": v(-33.3, 36.7) * mm});
            skLineSegment(sketch, "E3.17.0.55", {"start": v(-33.3, -23.3) * mm, "end": v(-33.3, -26.7) * mm});
            skLineSegment(sketch, "E3.17.0.56", {"start": v(-36.7, 26.7) * mm, "end": v(-33.3, 26.7) * mm});
            skLineSegment(sketch, "E3.17.0.57", {"start": v(-36.7, 31.7) * mm, "end": v(-33.3, 31.7) * mm});
            skLineSegment(sketch, "E3.17.0.58", {"start": v(-36.7, 21.7) * mm, "end": v(-36.7, 18.3) * mm});
            skLineSegment(sketch, "E3.17.0.59", {"start": v(-36.7, -6.7) * mm, "end": v(-33.3, -6.7) * mm});
            skLineSegment(sketch, "E3.18.0.0", {"start": v(-41.7, 36.7) * mm, "end": v(-41.7, 33.3) * mm});
            skLineSegment(sketch, "E3.18.0.1", {"start": v(-41.7, -21.7) * mm, "end": v(-38.3, -21.7) * mm});
            skLineSegment(sketch, "E3.18.0.2", {"start": v(-41.7, -3.3) * mm, "end": v(-41.7, -6.7) * mm});
            skLineSegment(sketch, "E3.18.0.3", {"start": v(-41.7, 8.3) * mm, "end": v(-38.3, 8.3) * mm});
            skLineSegment(sketch, "E3.18.0.4", {"start": v(-41.7, -33.3) * mm, "end": v(-38.3, -33.3) * mm});
            skLineSegment(sketch, "E3.18.0.5", {"start": v(-41.7, 31.7) * mm, "end": v(-41.7, 28.3) * mm});
            skLineSegment(sketch, "E3.18.0.6", {"start": v(-41.7, 1.7) * mm, "end": v(-41.7, -1.7) * mm});
            skLineSegment(sketch, "E3.18.0.7", {"start": v(-41.7, -18.3) * mm, "end": v(-41.7, -21.7) * mm});
            skLineSegment(sketch, "E3.18.0.8", {"start": v(-38.3, -33.3) * mm, "end": v(-38.3, -36.7) * mm});
            skLineSegment(sketch, "E3.18.0.9", {"start": v(-41.7, 16.7) * mm, "end": v(-41.7, 13.3) * mm});
            skLineSegment(sketch, "E3.18.0.10", {"start": v(-41.7, -8.3) * mm, "end": v(-41.7, -11.7) * mm});
            skLineSegment(sketch, "E3.18.0.11", {"start": v(-41.7, -36.7) * mm, "end": v(-38.3, -36.7) * mm});
            skLineSegment(sketch, "E3.18.0.12", {"start": v(-38.3, 26.7) * mm, "end": v(-38.3, 23.3) * mm});
            skLineSegment(sketch, "E3.18.0.13", {"start": v(-38.3, -28.3) * mm, "end": v(-38.3, -31.7) * mm});
            skLineSegment(sketch, "E3.18.0.14", {"start": v(-41.7, 23.3) * mm, "end": v(-38.3, 23.3) * mm});
            skLineSegment(sketch, "E3.18.0.15", {"start": v(-38.3, 6.7) * mm, "end": v(-38.3, 3.3) * mm});
            skLineSegment(sketch, "E3.18.0.16", {"start": v(-41.7, -28.3) * mm, "end": v(-38.3, -28.3) * mm});
            skLineSegment(sketch, "E3.18.0.17", {"start": v(-41.7, 13.3) * mm, "end": v(-38.3, 13.3) * mm});
            skLineSegment(sketch, "E3.18.0.18", {"start": v(-41.7, 33.3) * mm, "end": v(-38.3, 33.3) * mm});
            skLineSegment(sketch, "E3.18.0.19", {"start": v(-41.7, 3.3) * mm, "end": v(-38.3, 3.3) * mm});
            skLineSegment(sketch, "E3.18.0.20", {"start": v(-38.3, -13.3) * mm, "end": v(-38.3, -16.7) * mm});
            skLineSegment(sketch, "E3.18.0.21", {"start": v(-38.3, 16.7) * mm, "end": v(-38.3, 13.3) * mm});
            skLineSegment(sketch, "E3.18.0.22", {"start": v(-41.7, -23.3) * mm, "end": v(-41.7, -26.7) * mm});
            skLineSegment(sketch, "E3.18.0.23", {"start": v(-41.7, -28.3) * mm, "end": v(-41.7, -31.7) * mm});
            skLineSegment(sketch, "E3.18.0.24", {"start": v(-41.7, -13.3) * mm, "end": v(-41.7, -16.7) * mm});
            skLineSegment(sketch, "E3.18.0.25", {"start": v(-41.7, -23.3) * mm, "end": v(-38.3, -23.3) * mm});
            skLineSegment(sketch, "E3.18.0.26", {"start": v(-41.7, 1.7) * mm, "end": v(-38.3, 1.7) * mm});
            skLineSegment(sketch, "E3.18.0.27", {"start": v(-38.3, -3.3) * mm, "end": v(-38.3, -6.7) * mm});
            skLineSegment(sketch, "E3.18.0.28", {"start": v(-41.7, 28.3) * mm, "end": v(-38.3, 28.3) * mm});
            skLineSegment(sketch, "E3.18.0.29", {"start": v(-41.7, 21.7) * mm, "end": v(-38.3, 21.7) * mm});
            skLineSegment(sketch, "E3.18.0.30", {"start": v(-41.7, -18.3) * mm, "end": v(-38.3, -18.3) * mm});
            skLineSegment(sketch, "E3.18.0.31", {"start": v(-41.7, -13.3) * mm, "end": v(-38.3, -13.3) * mm});
            skLineSegment(sketch, "E3.18.0.32", {"start": v(-38.3, 1.7) * mm, "end": v(-38.3, -1.7) * mm});
            skLineSegment(sketch, "E3.18.0.33", {"start": v(-38.3, 36.7) * mm, "end": v(-38.3, 33.3) * mm});
            skLineSegment(sketch, "E3.18.0.34", {"start": v(-41.7, 18.3) * mm, "end": v(-38.3, 18.3) * mm});
            skLineSegment(sketch, "E3.18.0.35", {"start": v(-38.3, -18.3) * mm, "end": v(-38.3, -21.7) * mm});
            skLineSegment(sketch, "E3.18.0.36", {"start": v(-41.7, -33.3) * mm, "end": v(-41.7, -36.7) * mm});
            skLineSegment(sketch, "E3.18.0.37", {"start": v(-41.7, -3.3) * mm, "end": v(-38.3, -3.3) * mm});
            skLineSegment(sketch, "E3.18.0.38", {"start": v(-38.3, 21.7) * mm, "end": v(-38.3, 18.3) * mm});
            skLineSegment(sketch, "E3.18.0.39", {"start": v(-38.3, -8.3) * mm, "end": v(-38.3, -11.7) * mm});
            skLineSegment(sketch, "E3.18.0.40", {"start": v(-41.7, -16.7) * mm, "end": v(-38.3, -16.7) * mm});
            skLineSegment(sketch, "E3.18.0.41", {"start": v(-41.7, -31.7) * mm, "end": v(-38.3, -31.7) * mm});
            skLineSegment(sketch, "E3.18.0.42", {"start": v(-38.3, 31.7) * mm, "end": v(-38.3, 28.3) * mm});
            skLineSegment(sketch, "E3.18.0.43", {"start": v(-41.7, 26.7) * mm, "end": v(-41.7, 23.3) * mm});
            skLineSegment(sketch, "E3.18.0.44", {"start": v(-41.7, -1.7) * mm, "end": v(-38.3, -1.7) * mm});
            skLineSegment(sketch, "E3.18.0.45", {"start": v(-41.7, -26.7) * mm, "end": v(-38.3, -26.7) * mm});
            skLineSegment(sketch, "E3.18.0.46", {"start": v(-41.7, -8.3) * mm, "end": v(-38.3, -8.3) * mm});
            skLineSegment(sketch, "E3.18.0.47", {"start": v(-38.3, 11.7) * mm, "end": v(-38.3, 8.3) * mm});
            skLineSegment(sketch, "E3.18.0.48", {"start": v(-41.7, 6.7) * mm, "end": v(-41.7, 3.3) * mm});
            skLineSegment(sketch, "E3.18.0.49", {"start": v(-41.7, 16.7) * mm, "end": v(-38.3, 16.7) * mm});
            skLineSegment(sketch, "E3.18.0.50", {"start": v(-41.7, -11.7) * mm, "end": v(-38.3, -11.7) * mm});
            skLineSegment(sketch, "E3.18.0.51", {"start": v(-41.7, 6.7) * mm, "end": v(-38.3, 6.7) * mm});
            skLineSegment(sketch, "E3.18.0.52", {"start": v(-41.7, 11.7) * mm, "end": v(-41.7, 8.3) * mm});
            skLineSegment(sketch, "E3.18.0.53", {"start": v(-41.7, 11.7) * mm, "end": v(-38.3, 11.7) * mm});
            skLineSegment(sketch, "E3.18.0.54", {"start": v(-41.7, 36.7) * mm, "end": v(-38.3, 36.7) * mm});
            skLineSegment(sketch, "E3.18.0.55", {"start": v(-38.3, -23.3) * mm, "end": v(-38.3, -26.7) * mm});
            skLineSegment(sketch, "E3.18.0.56", {"start": v(-41.7, 26.7) * mm, "end": v(-38.3, 26.7) * mm});
            skLineSegment(sketch, "E3.18.0.57", {"start": v(-41.7, 31.7) * mm, "end": v(-38.3, 31.7) * mm});
            skLineSegment(sketch, "E3.18.0.58", {"start": v(-41.7, 21.7) * mm, "end": v(-41.7, 18.3) * mm});
            skLineSegment(sketch, "E3.18.0.59", {"start": v(-41.7, -6.7) * mm, "end": v(-38.3, -6.7) * mm});
            skLineSegment(sketch, "E3.19.0.0", {"start": v(-46.7, 36.7) * mm, "end": v(-46.7, 33.3) * mm});
            skLineSegment(sketch, "E3.19.0.1", {"start": v(-46.7, -21.7) * mm, "end": v(-43.3, -21.7) * mm});
            skLineSegment(sketch, "E3.19.0.2", {"start": v(-46.7, -3.3) * mm, "end": v(-46.7, -6.7) * mm});
            skLineSegment(sketch, "E3.19.0.3", {"start": v(-46.7, 8.3) * mm, "end": v(-43.3, 8.3) * mm});
            skLineSegment(sketch, "E3.19.0.4", {"start": v(-46.7, -33.3) * mm, "end": v(-43.3, -33.3) * mm});
            skLineSegment(sketch, "E3.19.0.5", {"start": v(-46.7, 31.7) * mm, "end": v(-46.7, 28.3) * mm});
            skLineSegment(sketch, "E3.19.0.6", {"start": v(-46.7, 1.7) * mm, "end": v(-46.7, -1.7) * mm});
            skLineSegment(sketch, "E3.19.0.7", {"start": v(-46.7, -18.3) * mm, "end": v(-46.7, -21.7) * mm});
            skLineSegment(sketch, "E3.19.0.8", {"start": v(-43.3, -33.3) * mm, "end": v(-43.3, -36.7) * mm});
            skLineSegment(sketch, "E3.19.0.9", {"start": v(-46.7, 16.7) * mm, "end": v(-46.7, 13.3) * mm});
            skLineSegment(sketch, "E3.19.0.10", {"start": v(-46.7, -8.3) * mm, "end": v(-46.7, -11.7) * mm});
            skLineSegment(sketch, "E3.19.0.11", {"start": v(-46.7, -36.7) * mm, "end": v(-43.3, -36.7) * mm});
            skLineSegment(sketch, "E3.19.0.12", {"start": v(-43.3, 26.7) * mm, "end": v(-43.3, 23.3) * mm});
            skLineSegment(sketch, "E3.19.0.13", {"start": v(-43.3, -28.3) * mm, "end": v(-43.3, -31.7) * mm});
            skLineSegment(sketch, "E3.19.0.14", {"start": v(-46.7, 23.3) * mm, "end": v(-43.3, 23.3) * mm});
            skLineSegment(sketch, "E3.19.0.15", {"start": v(-43.3, 6.7) * mm, "end": v(-43.3, 3.3) * mm});
            skLineSegment(sketch, "E3.19.0.16", {"start": v(-46.7, -28.3) * mm, "end": v(-43.3, -28.3) * mm});
            skLineSegment(sketch, "E3.19.0.17", {"start": v(-46.7, 13.3) * mm, "end": v(-43.3, 13.3) * mm});
            skLineSegment(sketch, "E3.19.0.18", {"start": v(-46.7, 33.3) * mm, "end": v(-43.3, 33.3) * mm});
            skLineSegment(sketch, "E3.19.0.19", {"start": v(-46.7, 3.3) * mm, "end": v(-43.3, 3.3) * mm});
            skLineSegment(sketch, "E3.19.0.20", {"start": v(-43.3, -13.3) * mm, "end": v(-43.3, -16.7) * mm});
            skLineSegment(sketch, "E3.19.0.21", {"start": v(-43.3, 16.7) * mm, "end": v(-43.3, 13.3) * mm});
            skLineSegment(sketch, "E3.19.0.22", {"start": v(-46.7, -23.3) * mm, "end": v(-46.7, -26.7) * mm});
            skLineSegment(sketch, "E3.19.0.23", {"start": v(-46.7, -28.3) * mm, "end": v(-46.7, -31.7) * mm});
            skLineSegment(sketch, "E3.19.0.24", {"start": v(-46.7, -13.3) * mm, "end": v(-46.7, -16.7) * mm});
            skLineSegment(sketch, "E3.19.0.25", {"start": v(-46.7, -23.3) * mm, "end": v(-43.3, -23.3) * mm});
            skLineSegment(sketch, "E3.19.0.26", {"start": v(-46.7, 1.7) * mm, "end": v(-43.3, 1.7) * mm});
            skLineSegment(sketch, "E3.19.0.27", {"start": v(-43.3, -3.3) * mm, "end": v(-43.3, -6.7) * mm});
            skLineSegment(sketch, "E3.19.0.28", {"start": v(-46.7, 28.3) * mm, "end": v(-43.3, 28.3) * mm});
            skLineSegment(sketch, "E3.19.0.29", {"start": v(-46.7, 21.7) * mm, "end": v(-43.3, 21.7) * mm});
            skLineSegment(sketch, "E3.19.0.30", {"start": v(-46.7, -18.3) * mm, "end": v(-43.3, -18.3) * mm});
            skLineSegment(sketch, "E3.19.0.31", {"start": v(-46.7, -13.3) * mm, "end": v(-43.3, -13.3) * mm});
            skLineSegment(sketch, "E3.19.0.32", {"start": v(-43.3, 1.7) * mm, "end": v(-43.3, -1.7) * mm});
            skLineSegment(sketch, "E3.19.0.33", {"start": v(-43.3, 36.7) * mm, "end": v(-43.3, 33.3) * mm});
            skLineSegment(sketch, "E3.19.0.34", {"start": v(-46.7, 18.3) * mm, "end": v(-43.3, 18.3) * mm});
            skLineSegment(sketch, "E3.19.0.35", {"start": v(-43.3, -18.3) * mm, "end": v(-43.3, -21.7) * mm});
            skLineSegment(sketch, "E3.19.0.36", {"start": v(-46.7, -33.3) * mm, "end": v(-46.7, -36.7) * mm});
            skLineSegment(sketch, "E3.19.0.37", {"start": v(-46.7, -3.3) * mm, "end": v(-43.3, -3.3) * mm});
            skLineSegment(sketch, "E3.19.0.38", {"start": v(-43.3, 21.7) * mm, "end": v(-43.3, 18.3) * mm});
            skLineSegment(sketch, "E3.19.0.39", {"start": v(-43.3, -8.3) * mm, "end": v(-43.3, -11.7) * mm});
            skLineSegment(sketch, "E3.19.0.40", {"start": v(-46.7, -16.7) * mm, "end": v(-43.3, -16.7) * mm});
            skLineSegment(sketch, "E3.19.0.41", {"start": v(-46.7, -31.7) * mm, "end": v(-43.3, -31.7) * mm});
            skLineSegment(sketch, "E3.19.0.42", {"start": v(-43.3, 31.7) * mm, "end": v(-43.3, 28.3) * mm});
            skLineSegment(sketch, "E3.19.0.43", {"start": v(-46.7, 26.7) * mm, "end": v(-46.7, 23.3) * mm});
            skLineSegment(sketch, "E3.19.0.44", {"start": v(-46.7, -1.7) * mm, "end": v(-43.3, -1.7) * mm});
            skLineSegment(sketch, "E3.19.0.45", {"start": v(-46.7, -26.7) * mm, "end": v(-43.3, -26.7) * mm});
            skLineSegment(sketch, "E3.19.0.46", {"start": v(-46.7, -8.3) * mm, "end": v(-43.3, -8.3) * mm});
            skLineSegment(sketch, "E3.19.0.47", {"start": v(-43.3, 11.7) * mm, "end": v(-43.3, 8.3) * mm});
            skLineSegment(sketch, "E3.19.0.48", {"start": v(-46.7, 6.7) * mm, "end": v(-46.7, 3.3) * mm});
            skLineSegment(sketch, "E3.19.0.49", {"start": v(-46.7, 16.7) * mm, "end": v(-43.3, 16.7) * mm});
            skLineSegment(sketch, "E3.19.0.50", {"start": v(-46.7, -11.7) * mm, "end": v(-43.3, -11.7) * mm});
            skLineSegment(sketch, "E3.19.0.51", {"start": v(-46.7, 6.7) * mm, "end": v(-43.3, 6.7) * mm});
            skLineSegment(sketch, "E3.19.0.52", {"start": v(-46.7, 11.7) * mm, "end": v(-46.7, 8.3) * mm});
            skLineSegment(sketch, "E3.19.0.53", {"start": v(-46.7, 11.7) * mm, "end": v(-43.3, 11.7) * mm});
            skLineSegment(sketch, "E3.19.0.54", {"start": v(-46.7, 36.7) * mm, "end": v(-43.3, 36.7) * mm});
            skLineSegment(sketch, "E3.19.0.55", {"start": v(-43.3, -23.3) * mm, "end": v(-43.3, -26.7) * mm});
            skLineSegment(sketch, "E3.19.0.56", {"start": v(-46.7, 26.7) * mm, "end": v(-43.3, 26.7) * mm});
            skLineSegment(sketch, "E3.19.0.57", {"start": v(-46.7, 31.7) * mm, "end": v(-43.3, 31.7) * mm});
            skLineSegment(sketch, "E3.19.0.58", {"start": v(-46.7, 21.7) * mm, "end": v(-46.7, 18.3) * mm});
            skLineSegment(sketch, "E3.19.0.59", {"start": v(-46.7, -6.7) * mm, "end": v(-43.3, -6.7) * mm});
            skLineSegment(sketch, "E3.20.0.0", {"start": v(-51.7, 36.7) * mm, "end": v(-51.7, 33.3) * mm});
            skLineSegment(sketch, "E3.20.0.1", {"start": v(-51.7, -21.7) * mm, "end": v(-48.3, -21.7) * mm});
            skLineSegment(sketch, "E3.20.0.2", {"start": v(-51.7, -3.3) * mm, "end": v(-51.7, -6.7) * mm});
            skLineSegment(sketch, "E3.20.0.3", {"start": v(-51.7, 8.3) * mm, "end": v(-48.3, 8.3) * mm});
            skLineSegment(sketch, "E3.20.0.4", {"start": v(-51.7, -33.3) * mm, "end": v(-48.3, -33.3) * mm});
            skLineSegment(sketch, "E3.20.0.5", {"start": v(-51.7, 31.7) * mm, "end": v(-51.7, 28.3) * mm});
            skLineSegment(sketch, "E3.20.0.6", {"start": v(-51.7, 1.7) * mm, "end": v(-51.7, -1.7) * mm});
            skLineSegment(sketch, "E3.20.0.7", {"start": v(-51.7, -18.3) * mm, "end": v(-51.7, -21.7) * mm});
            skLineSegment(sketch, "E3.20.0.8", {"start": v(-48.3, -33.3) * mm, "end": v(-48.3, -36.7) * mm});
            skLineSegment(sketch, "E3.20.0.9", {"start": v(-51.7, 16.7) * mm, "end": v(-51.7, 13.3) * mm});
            skLineSegment(sketch, "E3.20.0.10", {"start": v(-51.7, -8.3) * mm, "end": v(-51.7, -11.7) * mm});
            skLineSegment(sketch, "E3.20.0.11", {"start": v(-51.7, -36.7) * mm, "end": v(-48.3, -36.7) * mm});
            skLineSegment(sketch, "E3.20.0.12", {"start": v(-48.3, 26.7) * mm, "end": v(-48.3, 23.3) * mm});
            skLineSegment(sketch, "E3.20.0.13", {"start": v(-48.3, -28.3) * mm, "end": v(-48.3, -31.7) * mm});
            skLineSegment(sketch, "E3.20.0.14", {"start": v(-51.7, 23.3) * mm, "end": v(-48.3, 23.3) * mm});
            skLineSegment(sketch, "E3.20.0.15", {"start": v(-48.3, 6.7) * mm, "end": v(-48.3, 3.3) * mm});
            skLineSegment(sketch, "E3.20.0.16", {"start": v(-51.7, -28.3) * mm, "end": v(-48.3, -28.3) * mm});
            skLineSegment(sketch, "E3.20.0.17", {"start": v(-51.7, 13.3) * mm, "end": v(-48.3, 13.3) * mm});
            skLineSegment(sketch, "E3.20.0.18", {"start": v(-51.7, 33.3) * mm, "end": v(-48.3, 33.3) * mm});
            skLineSegment(sketch, "E3.20.0.19", {"start": v(-51.7, 3.3) * mm, "end": v(-48.3, 3.3) * mm});
            skLineSegment(sketch, "E3.20.0.20", {"start": v(-48.3, -13.3) * mm, "end": v(-48.3, -16.7) * mm});
            skLineSegment(sketch, "E3.20.0.21", {"start": v(-48.3, 16.7) * mm, "end": v(-48.3, 13.3) * mm});
            skLineSegment(sketch, "E3.20.0.22", {"start": v(-51.7, -23.3) * mm, "end": v(-51.7, -26.7) * mm});
            skLineSegment(sketch, "E3.20.0.23", {"start": v(-51.7, -28.3) * mm, "end": v(-51.7, -31.7) * mm});
            skLineSegment(sketch, "E3.20.0.24", {"start": v(-51.7, -13.3) * mm, "end": v(-51.7, -16.7) * mm});
            skLineSegment(sketch, "E3.20.0.25", {"start": v(-51.7, -23.3) * mm, "end": v(-48.3, -23.3) * mm});
            skLineSegment(sketch, "E3.20.0.26", {"start": v(-51.7, 1.7) * mm, "end": v(-48.3, 1.7) * mm});
            skLineSegment(sketch, "E3.20.0.27", {"start": v(-48.3, -3.3) * mm, "end": v(-48.3, -6.7) * mm});
            skLineSegment(sketch, "E3.20.0.28", {"start": v(-51.7, 28.3) * mm, "end": v(-48.3, 28.3) * mm});
            skLineSegment(sketch, "E3.20.0.29", {"start": v(-51.7, 21.7) * mm, "end": v(-48.3, 21.7) * mm});
            skLineSegment(sketch, "E3.20.0.30", {"start": v(-51.7, -18.3) * mm, "end": v(-48.3, -18.3) * mm});
            skLineSegment(sketch, "E3.20.0.31", {"start": v(-51.7, -13.3) * mm, "end": v(-48.3, -13.3) * mm});
            skLineSegment(sketch, "E3.20.0.32", {"start": v(-48.3, 1.7) * mm, "end": v(-48.3, -1.7) * mm});
            skLineSegment(sketch, "E3.20.0.33", {"start": v(-48.3, 36.7) * mm, "end": v(-48.3, 33.3) * mm});
            skLineSegment(sketch, "E3.20.0.34", {"start": v(-51.7, 18.3) * mm, "end": v(-48.3, 18.3) * mm});
            skLineSegment(sketch, "E3.20.0.35", {"start": v(-48.3, -18.3) * mm, "end": v(-48.3, -21.7) * mm});
            skLineSegment(sketch, "E3.20.0.36", {"start": v(-51.7, -33.3) * mm, "end": v(-51.7, -36.7) * mm});
            skLineSegment(sketch, "E3.20.0.37", {"start": v(-51.7, -3.3) * mm, "end": v(-48.3, -3.3) * mm});
            skLineSegment(sketch, "E3.20.0.38", {"start": v(-48.3, 21.7) * mm, "end": v(-48.3, 18.3) * mm});
            skLineSegment(sketch, "E3.20.0.39", {"start": v(-48.3, -8.3) * mm, "end": v(-48.3, -11.7) * mm});
            skLineSegment(sketch, "E3.20.0.40", {"start": v(-51.7, -16.7) * mm, "end": v(-48.3, -16.7) * mm});
            skLineSegment(sketch, "E3.20.0.41", {"start": v(-51.7, -31.7) * mm, "end": v(-48.3, -31.7) * mm});
            skLineSegment(sketch, "E3.20.0.42", {"start": v(-48.3, 31.7) * mm, "end": v(-48.3, 28.3) * mm});
            skLineSegment(sketch, "E3.20.0.43", {"start": v(-51.7, 26.7) * mm, "end": v(-51.7, 23.3) * mm});
            skLineSegment(sketch, "E3.20.0.44", {"start": v(-51.7, -1.7) * mm, "end": v(-48.3, -1.7) * mm});
            skLineSegment(sketch, "E3.20.0.45", {"start": v(-51.7, -26.7) * mm, "end": v(-48.3, -26.7) * mm});
            skLineSegment(sketch, "E3.20.0.46", {"start": v(-51.7, -8.3) * mm, "end": v(-48.3, -8.3) * mm});
            skLineSegment(sketch, "E3.20.0.47", {"start": v(-48.3, 11.7) * mm, "end": v(-48.3, 8.3) * mm});
            skLineSegment(sketch, "E3.20.0.48", {"start": v(-51.7, 6.7) * mm, "end": v(-51.7, 3.3) * mm});
            skLineSegment(sketch, "E3.20.0.49", {"start": v(-51.7, 16.7) * mm, "end": v(-48.3, 16.7) * mm});
            skLineSegment(sketch, "E3.20.0.50", {"start": v(-51.7, -11.7) * mm, "end": v(-48.3, -11.7) * mm});
            skLineSegment(sketch, "E3.20.0.51", {"start": v(-51.7, 6.7) * mm, "end": v(-48.3, 6.7) * mm});
            skLineSegment(sketch, "E3.20.0.52", {"start": v(-51.7, 11.7) * mm, "end": v(-51.7, 8.3) * mm});
            skLineSegment(sketch, "E3.20.0.53", {"start": v(-51.7, 11.7) * mm, "end": v(-48.3, 11.7) * mm});
            skLineSegment(sketch, "E3.20.0.54", {"start": v(-51.7, 36.7) * mm, "end": v(-48.3, 36.7) * mm});
            skLineSegment(sketch, "E3.20.0.55", {"start": v(-48.3, -23.3) * mm, "end": v(-48.3, -26.7) * mm});
            skLineSegment(sketch, "E3.20.0.56", {"start": v(-51.7, 26.7) * mm, "end": v(-48.3, 26.7) * mm});
            skLineSegment(sketch, "E3.20.0.57", {"start": v(-51.7, 31.7) * mm, "end": v(-48.3, 31.7) * mm});
            skLineSegment(sketch, "E3.20.0.58", {"start": v(-51.7, 21.7) * mm, "end": v(-51.7, 18.3) * mm});
            skLineSegment(sketch, "E3.20.0.59", {"start": v(-51.7, -6.7) * mm, "end": v(-48.3, -6.7) * mm});
            skLineSegment(sketch, "E3.direction1", {"start": v(48.3, -36.7) * mm, "end": v(43.3, -36.7) * mm, "construction": true});
            skSolve(sketch);
        }
        {
            var Q0;
            Q0=makeQuery(id+"F0.imprint","IMPRINT",FACE,{"disambiguationData":[TD([[makeQuery(id+"F0.imprint","IMPRINT",EDGE,{"derivedFrom":sQuery(id+"F0.wireOp",EDGE,"E0.bottom")}),-1.0]])]});
            extrude(context, id + "F1", {"entities" : qUnion([Q0]), "depth" : 2 * mm, "offsetDistance" : 25 * mm});
        }
        {
            var Q0;
            Q0=makeQuery(id+"F1.opExtrude","CAP_FACE",FACE,{"disambiguationData":[OSD([sQuery(id+"F0.wireOp",EDGE,"E0.bottom"),sQuery(id+"F0.wireOp",EDGE,"E0.top"),sQuery(id+"F0.wireOp",EDGE,"E0.left"),sQuery(id+"F0.wireOp",EDGE,"E0.right"),sQuery(id+"F0.wireOp",EDGE,"E1.10.0.0"),sQuery(id+"F0.wireOp",EDGE,"E1.10.0.1"),sQuery(id+"F0.wireOp",EDGE,"E1.10.0.2"),sQuery(id+"F0.wireOp",EDGE,"E1.10.0.3"),sQuery(id+"F0.wireOp",EDGE,"E1.10.1.0"),sQuery(id+"F0.wireOp",EDGE,"E1.10.1.1"),sQuery(id+"F0.wireOp",EDGE,"E1.10.1.2"),sQuery(id+"F0.wireOp",EDGE,"E1.10.1.3"),sQuery(id+"F0.wireOp",EDGE,"E1.10.2.0"),sQuery(id+"F0.wireOp",EDGE,"E1.10.2.1"),sQuery(id+"F0.wireOp",EDGE,"E1.10.2.2"),sQuery(id+"F0.wireOp",EDGE,"E1.10.2.3"),sQuery(id+"F0.wireOp",EDGE,"E1.10.3.0"),sQuery(id+"F0.wireOp",EDGE,"E1.10.3.1"),sQuery(id+"F0.wireOp",EDGE,"E1.10.3.2"),sQuery(id+"F0.wireOp",EDGE,"E1.10.3.3"),sQuery(id+"F0.wireOp",EDGE,"E1.10.4.0"),sQuery(id+"F0.wireOp",EDGE,"E1.10.4.1"),sQuery(id+"F0.wireOp",EDGE,"E1.10.4.2"),sQuery(id+"F0.wireOp",EDGE,"E1.10.4.3"),sQuery(id+"F0.wireOp",EDGE,"E1.10.5.0"),sQuery(id+"F0.wireOp",EDGE,"E1.10.5.1"),sQuery(id+"F0.wireOp",EDGE,"E1.10.5.2"),sQuery(id+"F0.wireOp",EDGE,"E1.10.5.3"),sQuery(id+"F0.wireOp",EDGE,"E1.10.6.0"),sQuery(id+"F0.wireOp",EDGE,"E1.10.6.1"),sQuery(id+"F0.wireOp",EDGE,"E1.10.6.2"),sQuery(id+"F0.wireOp",EDGE,"E1.10.6.3"),sQuery(id+"F0.wireOp",EDGE,"E1.10.7.0"),sQuery(id+"F0.wireOp",EDGE,"E1.10.7.1"),sQuery(id+"F0.wireOp",EDGE,"E1.10.7.2"),sQuery(id+"F0.wireOp",EDGE,"E1.10.7.3"),sQuery(id+"F0.wireOp",EDGE,"E2.0.1.4"),sQuery(id+"F0.wireOp",EDGE,"E2.0.1.13"),sQuery(id+"F0.wireOp",EDGE,"E2.0.1.19"),sQuery(id+"F0.wireOp",EDGE,"E2.0.1.21"),sQuery(id+"F0.wireOp",EDGE,"E2.0.2.4"),sQuery(id+"F0.wireOp",EDGE,"E2.0.2.13"),sQuery(id+"F0.wireOp",EDGE,"E2.0.2.19"),sQuery(id+"F0.wireOp",EDGE,"E2.0.2.21"),sQuery(id+"F0.wireOp",EDGE,"E2.0.3.4"),sQuery(id+"F0.wireOp",EDGE,"E2.0.3.13"),sQuery(id+"F0.wireOp",EDGE,"E2.0.3.19"),sQuery(id+"F0.wireOp",EDGE,"E2.0.3.21"),sQuery(id+"F0.wireOp",EDGE,"E2.0.4.4"),sQuery(id+"F0.wireOp",EDGE,"E2.0.4.13"),sQuery(id+"F0.wireOp",EDGE,"E2.0.4.19"),sQuery(id+"F0.wireOp",EDGE,"E2.0.4.21"),sQuery(id+"F0.wireOp",EDGE,"E2.0.5.4"),sQuery(id+"F0.wireOp",EDGE,"E2.0.5.13"),sQuery(id+"F0.wireOp",EDGE,"E2.0.5.19"),sQuery(id+"F0.wireOp",EDGE,"E2.0.5.21"),sQuery(id+"F0.wireOp",EDGE,"E2.0.6.4"),sQuery(id+"F0.wireOp",EDGE,"E2.0.6.13"),sQuery(id+"F0.wireOp",EDGE,"E2.0.6.19"),sQuery(id+"F0.wireOp",EDGE,"E2.0.6.21"),sQuery(id+"F0.wireOp",EDGE,"E2.0.7.4"),sQuery(id+"F0.wireOp",EDGE,"E2.0.7.13"),sQuery(id+"F0.wireOp",EDGE,"E2.0.7.19"),sQuery(id+"F0.wireOp",EDGE,"E2.0.7.21"),sQuery(id+"F0.wireOp",EDGE,"E3.1.0.0"),sQuery(id+"F0.wireOp",EDGE,"E3.1.0.1"),sQuery(id+"F0.wireOp",EDGE,"E3.1.0.2"),sQuery(id+"F0.wireOp",EDGE,"E3.1.0.3"),sQuery(id+"F0.wireOp",EDGE,"E3.1.0.4"),sQuery(id+"F0.wireOp",EDGE,"E3.1.0.5"),sQuery(id+"F0.wireOp",EDGE,"E3.1.0.6"),sQuery(id+"F0.wireOp",EDGE,"E3.1.0.7"),sQuery(id+"F0.wireOp",EDGE,"E3.1.0.8"),sQuery(id+"F0.wireOp",EDGE,"E3.1.0.9"),sQuery(id+"F0.wireOp",EDGE,"E3.1.0.10"),sQuery(id+"F0.wireOp",EDGE,"E3.1.0.11"),sQuery(id+"F0.wireOp",EDGE,"E3.1.0.12"),sQuery(id+"F0.wireOp",EDGE,"E3.1.0.13"),sQuery(id+"F0.wireOp",EDGE,"E3.1.0.14"),sQuery(id+"F0.wireOp",EDGE,"E3.1.0.15"),sQuery(id+"F0.wireOp",EDGE,"E3.1.0.16"),sQuery(id+"F0.wireOp",EDGE,"E3.1.0.17"),sQuery(id+"F0.wireOp",EDGE,"E3.1.0.18"),sQuery(id+"F0.wireOp",EDGE,"E3.1.0.19"),sQuery(id+"F0.wireOp",EDGE,"E3.1.0.20"),sQuery(id+"F0.wireOp",EDGE,"E3.1.0.21"),sQuery(id+"F0.wireOp",EDGE,"E3.1.0.22"),sQuery(id+"F0.wireOp",EDGE,"E3.1.0.23"),sQuery(id+"F0.wireOp",EDGE,"E3.1.0.24"),sQuery(id+"F0.wireOp",EDGE,"E3.1.0.25"),sQuery(id+"F0.wireOp",EDGE,"E3.1.0.26"),sQuery(id+"F0.wireOp",EDGE,"E3.1.0.27"),sQuery(id+"F0.wireOp",EDGE,"E3.1.0.28"),sQuery(id+"F0.wireOp",EDGE,"E3.1.0.29"),sQuery(id+"F0.wireOp",EDGE,"E3.1.0.30"),sQuery(id+"F0.wireOp",EDGE,"E3.1.0.31"),sQuery(id+"F0.wireOp",EDGE,"E3.1.0.32"),sQuery(id+"F0.wireOp",EDGE,"E3.1.0.33"),sQuery(id+"F0.wireOp",EDGE,"E3.1.0.34"),sQuery(id+"F0.wireOp",EDGE,"E3.1.0.35"),sQuery(id+"F0.wireOp",EDGE,"E3.1.0.36"),sQuery(id+"F0.wireOp",EDGE,"E3.1.0.37"),sQuery(id+"F0.wireOp",EDGE,"E3.1.0.38"),sQuery(id+"F0.wireOp",EDGE,"E3.1.0.39"),sQuery(id+"F0.wireOp",EDGE,"E3.1.0.40"),sQuery(id+"F0.wireOp",EDGE,"E3.1.0.41"),sQuery(id+"F0.wireOp",EDGE,"E3.1.0.42"),sQuery(id+"F0.wireOp",EDGE,"E3.1.0.43"),sQuery(id+"F0.wireOp",EDGE,"E3.1.0.44"),sQuery(id+"F0.wireOp",EDGE,"E3.1.0.45"),sQuery(id+"F0.wireOp",EDGE,"E3.1.0.46"),sQuery(id+"F0.wireOp",EDGE,"E3.1.0.47"),sQuery(id+"F0.wireOp",EDGE,"E3.1.0.48"),sQuery(id+"F0.wireOp",EDGE,"E3.1.0.49"),sQuery(id+"F0.wireOp",EDGE,"E3.1.0.50"),sQuery(id+"F0.wireOp",EDGE,"E3.1.0.51"),sQuery(id+"F0.wireOp",EDGE,"E3.1.0.52"),sQuery(id+"F0.wireOp",EDGE,"E3.1.0.53"),sQuery(id+"F0.wireOp",EDGE,"E3.1.0.54"),sQuery(id+"F0.wireOp",EDGE,"E3.1.0.55"),sQuery(id+"F0.wireOp",EDGE,"E3.1.0.56"),sQuery(id+"F0.wireOp",EDGE,"E3.1.0.57"),sQuery(id+"F0.wireOp",EDGE,"E3.1.0.58"),sQuery(id+"F0.wireOp",EDGE,"E3.1.0.59"),sQuery(id+"F0.wireOp",EDGE,"E3.2.0.0"),sQuery(id+"F0.wireOp",EDGE,"E3.2.0.1"),sQuery(id+"F0.wireOp",EDGE,"E3.2.0.2"),sQuery(id+"F0.wireOp",EDGE,"E3.2.0.3"),sQuery(id+"F0.wireOp",EDGE,"E3.2.0.4"),sQuery(id+"F0.wireOp",EDGE,"E3.2.0.5"),sQuery(id+"F0.wireOp",EDGE,"E3.2.0.6"),sQuery(id+"F0.wireOp",EDGE,"E3.2.0.7"),sQuery(id+"F0.wireOp",EDGE,"E3.2.0.8"),sQuery(id+"F0.wireOp",EDGE,"E3.2.0.9"),sQuery(id+"F0.wireOp",EDGE,"E3.2.0.10"),sQuery(id+"F0.wireOp",EDGE,"E3.2.0.11"),sQuery(id+"F0.wireOp",EDGE,"E3.2.0.12"),sQuery(id+"F0.wireOp",EDGE,"E3.2.0.13"),sQuery(id+"F0.wireOp",EDGE,"E3.2.0.14"),sQuery(id+"F0.wireOp",EDGE,"E3.2.0.15"),sQuery(id+"F0.wireOp",EDGE,"E3.2.0.16"),sQuery(id+"F0.wireOp",EDGE,"E3.2.0.17"),sQuery(id+"F0.wireOp",EDGE,"E3.2.0.18"),sQuery(id+"F0.wireOp",EDGE,"E3.2.0.19"),sQuery(id+"F0.wireOp",EDGE,"E3.2.0.20"),sQuery(id+"F0.wireOp",EDGE,"E3.2.0.21"),sQuery(id+"F0.wireOp",EDGE,"E3.2.0.22"),sQuery(id+"F0.wireOp",EDGE,"E3.2.0.23"),sQuery(id+"F0.wireOp",EDGE,"E3.2.0.24"),sQuery(id+"F0.wireOp",EDGE,"E3.2.0.25"),sQuery(id+"F0.wireOp",EDGE,"E3.2.0.26"),sQuery(id+"F0.wireOp",EDGE,"E3.2.0.27"),sQuery(id+"F0.wireOp",EDGE,"E3.2.0.28"),sQuery(id+"F0.wireOp",EDGE,"E3.2.0.29"),sQuery(id+"F0.wireOp",EDGE,"E3.2.0.30"),sQuery(id+"F0.wireOp",EDGE,"E3.2.0.31"),sQuery(id+"F0.wireOp",EDGE,"E3.2.0.32"),sQuery(id+"F0.wireOp",EDGE,"E3.2.0.33"),sQuery(id+"F0.wireOp",EDGE,"E3.2.0.34"),sQuery(id+"F0.wireOp",EDGE,"E3.2.0.35"),sQuery(id+"F0.wireOp",EDGE,"E3.2.0.36"),sQuery(id+"F0.wireOp",EDGE,"E3.2.0.37"),sQuery(id+"F0.wireOp",EDGE,"E3.2.0.38"),sQuery(id+"F0.wireOp",EDGE,"E3.2.0.39"),sQuery(id+"F0.wireOp",EDGE,"E3.2.0.40"),sQuery(id+"F0.wireOp",EDGE,"E3.2.0.41"),sQuery(id+"F0.wireOp",EDGE,"E3.2.0.42"),sQuery(id+"F0.wireOp",EDGE,"E3.2.0.43"),sQuery(id+"F0.wireOp",EDGE,"E3.2.0.44"),sQuery(id+"F0.wireOp",EDGE,"E3.2.0.45"),sQuery(id+"F0.wireOp",EDGE,"E3.2.0.46"),sQuery(id+"F0.wireOp",EDGE,"E3.2.0.47"),sQuery(id+"F0.wireOp",EDGE,"E3.2.0.48"),sQuery(id+"F0.wireOp",EDGE,"E3.2.0.49"),sQuery(id+"F0.wireOp",EDGE,"E3.2.0.50"),sQuery(id+"F0.wireOp",EDGE,"E3.2.0.51"),sQuery(id+"F0.wireOp",EDGE,"E3.2.0.52"),sQuery(id+"F0.wireOp",EDGE,"E3.2.0.53"),sQuery(id+"F0.wireOp",EDGE,"E3.2.0.54"),sQuery(id+"F0.wireOp",EDGE,"E3.2.0.55"),sQuery(id+"F0.wireOp",EDGE,"E3.2.0.56"),sQuery(id+"F0.wireOp",EDGE,"E3.2.0.57"),sQuery(id+"F0.wireOp",EDGE,"E3.2.0.58"),sQuery(id+"F0.wireOp",EDGE,"E3.2.0.59"),sQuery(id+"F0.wireOp",EDGE,"E3.3.0.0"),sQuery(id+"F0.wireOp",EDGE,"E3.3.0.1"),sQuery(id+"F0.wireOp",EDGE,"E3.3.0.2"),sQuery(id+"F0.wireOp",EDGE,"E3.3.0.3"),sQuery(id+"F0.wireOp",EDGE,"E3.3.0.4"),sQuery(id+"F0.wireOp",EDGE,"E3.3.0.5"),sQuery(id+"F0.wireOp",EDGE,"E3.3.0.6"),sQuery(id+"F0.wireOp",EDGE,"E3.3.0.7"),sQuery(id+"F0.wireOp",EDGE,"E3.3.0.8"),sQuery(id+"F0.wireOp",EDGE,"E3.3.0.9"),sQuery(id+"F0.wireOp",EDGE,"E3.3.0.10"),sQuery(id+"F0.wireOp",EDGE,"E3.3.0.11"),sQuery(id+"F0.wireOp",EDGE,"E3.3.0.12"),sQuery(id+"F0.wireOp",EDGE,"E3.3.0.13"),sQuery(id+"F0.wireOp",EDGE,"E3.3.0.14"),sQuery(id+"F0.wireOp",EDGE,"E3.3.0.15"),sQuery(id+"F0.wireOp",EDGE,"E3.3.0.16"),sQuery(id+"F0.wireOp",EDGE,"E3.3.0.17"),sQuery(id+"F0.wireOp",EDGE,"E3.3.0.18"),sQuery(id+"F0.wireOp",EDGE,"E3.3.0.19"),sQuery(id+"F0.wireOp",EDGE,"E3.3.0.20"),sQuery(id+"F0.wireOp",EDGE,"E3.3.0.21"),sQuery(id+"F0.wireOp",EDGE,"E3.3.0.22"),sQuery(id+"F0.wireOp",EDGE,"E3.3.0.23"),sQuery(id+"F0.wireOp",EDGE,"E3.3.0.24"),sQuery(id+"F0.wireOp",EDGE,"E3.3.0.25"),sQuery(id+"F0.wireOp",EDGE,"E3.3.0.26"),sQuery(id+"F0.wireOp",EDGE,"E3.3.0.27"),sQuery(id+"F0.wireOp",EDGE,"E3.3.0.28"),sQuery(id+"F0.wireOp",EDGE,"E3.3.0.29"),sQuery(id+"F0.wireOp",EDGE,"E3.3.0.30"),sQuery(id+"F0.wireOp",EDGE,"E3.3.0.31"),sQuery(id+"F0.wireOp",EDGE,"E3.3.0.32"),sQuery(id+"F0.wireOp",EDGE,"E3.3.0.33"),sQuery(id+"F0.wireOp",EDGE,"E3.3.0.34"),sQuery(id+"F0.wireOp",EDGE,"E3.3.0.35"),sQuery(id+"F0.wireOp",EDGE,"E3.3.0.36"),sQuery(id+"F0.wireOp",EDGE,"E3.3.0.37"),sQuery(id+"F0.wireOp",EDGE,"E3.3.0.38"),sQuery(id+"F0.wireOp",EDGE,"E3.3.0.39"),sQuery(id+"F0.wireOp",EDGE,"E3.3.0.40"),sQuery(id+"F0.wireOp",EDGE,"E3.3.0.41"),sQuery(id+"F0.wireOp",EDGE,"E3.3.0.42"),sQuery(id+"F0.wireOp",EDGE,"E3.3.0.43"),sQuery(id+"F0.wireOp",EDGE,"E3.3.0.44"),sQuery(id+"F0.wireOp",EDGE,"E3.3.0.45"),sQuery(id+"F0.wireOp",EDGE,"E3.3.0.46"),sQuery(id+"F0.wireOp",EDGE,"E3.3.0.47"),sQuery(id+"F0.wireOp",EDGE,"E3.3.0.48"),sQuery(id+"F0.wireOp",EDGE,"E3.3.0.49"),sQuery(id+"F0.wireOp",EDGE,"E3.3.0.50"),sQuery(id+"F0.wireOp",EDGE,"E3.3.0.51"),sQuery(id+"F0.wireOp",EDGE,"E3.3.0.52"),sQuery(id+"F0.wireOp",EDGE,"E3.3.0.53"),sQuery(id+"F0.wireOp",EDGE,"E3.3.0.54"),sQuery(id+"F0.wireOp",EDGE,"E3.3.0.55"),sQuery(id+"F0.wireOp",EDGE,"E3.3.0.56"),sQuery(id+"F0.wireOp",EDGE,"E3.3.0.57"),sQuery(id+"F0.wireOp",EDGE,"E3.3.0.58"),sQuery(id+"F0.wireOp",EDGE,"E3.3.0.59"),sQuery(id+"F0.wireOp",EDGE,"E3.4.0.0"),sQuery(id+"F0.wireOp",EDGE,"E3.4.0.1"),sQuery(id+"F0.wireOp",EDGE,"E3.4.0.2"),sQuery(id+"F0.wireOp",EDGE,"E3.4.0.3"),sQuery(id+"F0.wireOp",EDGE,"E3.4.0.4"),sQuery(id+"F0.wireOp",EDGE,"E3.4.0.5"),sQuery(id+"F0.wireOp",EDGE,"E3.4.0.6"),sQuery(id+"F0.wireOp",EDGE,"E3.4.0.7"),sQuery(id+"F0.wireOp",EDGE,"E3.4.0.8"),sQuery(id+"F0.wireOp",EDGE,"E3.4.0.9"),sQuery(id+"F0.wireOp",EDGE,"E3.4.0.10"),sQuery(id+"F0.wireOp",EDGE,"E3.4.0.11"),sQuery(id+"F0.wireOp",EDGE,"E3.4.0.12"),sQuery(id+"F0.wireOp",EDGE,"E3.4.0.13"),sQuery(id+"F0.wireOp",EDGE,"E3.4.0.14"),sQuery(id+"F0.wireOp",EDGE,"E3.4.0.15"),sQuery(id+"F0.wireOp",EDGE,"E3.4.0.16"),sQuery(id+"F0.wireOp",EDGE,"E3.4.0.17"),sQuery(id+"F0.wireOp",EDGE,"E3.4.0.18"),sQuery(id+"F0.wireOp",EDGE,"E3.4.0.19"),sQuery(id+"F0.wireOp",EDGE,"E3.4.0.20"),sQuery(id+"F0.wireOp",EDGE,"E3.4.0.21"),sQuery(id+"F0.wireOp",EDGE,"E3.4.0.22"),sQuery(id+"F0.wireOp",EDGE,"E3.4.0.23"),sQuery(id+"F0.wireOp",EDGE,"E3.4.0.24"),sQuery(id+"F0.wireOp",EDGE,"E3.4.0.25"),sQuery(id+"F0.wireOp",EDGE,"E3.4.0.26"),sQuery(id+"F0.wireOp",EDGE,"E3.4.0.27"),sQuery(id+"F0.wireOp",EDGE,"E3.4.0.28"),sQuery(id+"F0.wireOp",EDGE,"E3.4.0.29"),sQuery(id+"F0.wireOp",EDGE,"E3.4.0.30"),sQuery(id+"F0.wireOp",EDGE,"E3.4.0.31"),sQuery(id+"F0.wireOp",EDGE,"E3.4.0.32"),sQuery(id+"F0.wireOp",EDGE,"E3.4.0.33"),sQuery(id+"F0.wireOp",EDGE,"E3.4.0.34"),sQuery(id+"F0.wireOp",EDGE,"E3.4.0.35"),sQuery(id+"F0.wireOp",EDGE,"E3.4.0.36"),sQuery(id+"F0.wireOp",EDGE,"E3.4.0.37"),sQuery(id+"F0.wireOp",EDGE,"E3.4.0.38"),sQuery(id+"F0.wireOp",EDGE,"E3.4.0.39"),sQuery(id+"F0.wireOp",EDGE,"E3.4.0.40"),sQuery(id+"F0.wireOp",EDGE,"E3.4.0.41"),sQuery(id+"F0.wireOp",EDGE,"E3.4.0.42"),sQuery(id+"F0.wireOp",EDGE,"E3.4.0.43"),sQuery(id+"F0.wireOp",EDGE,"E3.4.0.44"),sQuery(id+"F0.wireOp",EDGE,"E3.4.0.45"),sQuery(id+"F0.wireOp",EDGE,"E3.4.0.46"),sQuery(id+"F0.wireOp",EDGE,"E3.4.0.47"),sQuery(id+"F0.wireOp",EDGE,"E3.4.0.48"),sQuery(id+"F0.wireOp",EDGE,"E3.4.0.49"),sQuery(id+"F0.wireOp",EDGE,"E3.4.0.50"),sQuery(id+"F0.wireOp",EDGE,"E3.4.0.51"),sQuery(id+"F0.wireOp",EDGE,"E3.4.0.52"),sQuery(id+"F0.wireOp",EDGE,"E3.4.0.53"),sQuery(id+"F0.wireOp",EDGE,"E3.4.0.54"),sQuery(id+"F0.wireOp",EDGE,"E3.4.0.55"),sQuery(id+"F0.wireOp",EDGE,"E3.4.0.56"),sQuery(id+"F0.wireOp",EDGE,"E3.4.0.57"),sQuery(id+"F0.wireOp",EDGE,"E3.4.0.58"),sQuery(id+"F0.wireOp",EDGE,"E3.4.0.59"),sQuery(id+"F0.wireOp",EDGE,"E3.5.0.0"),sQuery(id+"F0.wireOp",EDGE,"E3.5.0.1"),sQuery(id+"F0.wireOp",EDGE,"E3.5.0.2"),sQuery(id+"F0.wireOp",EDGE,"E3.5.0.3"),sQuery(id+"F0.wireOp",EDGE,"E3.5.0.4"),sQuery(id+"F0.wireOp",EDGE,"E3.5.0.5"),sQuery(id+"F0.wireOp",EDGE,"E3.5.0.6"),sQuery(id+"F0.wireOp",EDGE,"E3.5.0.7"),sQuery(id+"F0.wireOp",EDGE,"E3.5.0.8"),sQuery(id+"F0.wireOp",EDGE,"E3.5.0.9"),sQuery(id+"F0.wireOp",EDGE,"E3.5.0.10"),sQuery(id+"F0.wireOp",EDGE,"E3.5.0.11"),sQuery(id+"F0.wireOp",EDGE,"E3.5.0.12"),sQuery(id+"F0.wireOp",EDGE,"E3.5.0.13"),sQuery(id+"F0.wireOp",EDGE,"E3.5.0.14"),sQuery(id+"F0.wireOp",EDGE,"E3.5.0.15"),sQuery(id+"F0.wireOp",EDGE,"E3.5.0.16"),sQuery(id+"F0.wireOp",EDGE,"E3.5.0.17"),sQuery(id+"F0.wireOp",EDGE,"E3.5.0.18"),sQuery(id+"F0.wireOp",EDGE,"E3.5.0.19"),sQuery(id+"F0.wireOp",EDGE,"E3.5.0.20"),sQuery(id+"F0.wireOp",EDGE,"E3.5.0.21"),sQuery(id+"F0.wireOp",EDGE,"E3.5.0.22"),sQuery(id+"F0.wireOp",EDGE,"E3.5.0.23"),sQuery(id+"F0.wireOp",EDGE,"E3.5.0.24"),sQuery(id+"F0.wireOp",EDGE,"E3.5.0.25"),sQuery(id+"F0.wireOp",EDGE,"E3.5.0.26"),sQuery(id+"F0.wireOp",EDGE,"E3.5.0.27"),sQuery(id+"F0.wireOp",EDGE,"E3.5.0.28"),sQuery(id+"F0.wireOp",EDGE,"E3.5.0.29"),sQuery(id+"F0.wireOp",EDGE,"E3.5.0.30"),sQuery(id+"F0.wireOp",EDGE,"E3.5.0.31"),sQuery(id+"F0.wireOp",EDGE,"E3.5.0.32"),sQuery(id+"F0.wireOp",EDGE,"E3.5.0.33"),sQuery(id+"F0.wireOp",EDGE,"E3.5.0.34"),sQuery(id+"F0.wireOp",EDGE,"E3.5.0.35"),sQuery(id+"F0.wireOp",EDGE,"E3.5.0.36"),sQuery(id+"F0.wireOp",EDGE,"E3.5.0.37"),sQuery(id+"F0.wireOp",EDGE,"E3.5.0.38"),sQuery(id+"F0.wireOp",EDGE,"E3.5.0.39"),sQuery(id+"F0.wireOp",EDGE,"E3.5.0.40"),sQuery(id+"F0.wireOp",EDGE,"E3.5.0.41"),sQuery(id+"F0.wireOp",EDGE,"E3.5.0.42"),sQuery(id+"F0.wireOp",EDGE,"E3.5.0.43"),sQuery(id+"F0.wireOp",EDGE,"E3.5.0.44"),sQuery(id+"F0.wireOp",EDGE,"E3.5.0.45"),sQuery(id+"F0.wireOp",EDGE,"E3.5.0.46"),sQuery(id+"F0.wireOp",EDGE,"E3.5.0.47"),sQuery(id+"F0.wireOp",EDGE,"E3.5.0.48"),sQuery(id+"F0.wireOp",EDGE,"E3.5.0.49"),sQuery(id+"F0.wireOp",EDGE,"E3.5.0.50"),sQuery(id+"F0.wireOp",EDGE,"E3.5.0.51"),sQuery(id+"F0.wireOp",EDGE,"E3.5.0.52"),sQuery(id+"F0.wireOp",EDGE,"E3.5.0.53"),sQuery(id+"F0.wireOp",EDGE,"E3.5.0.54"),sQuery(id+"F0.wireOp",EDGE,"E3.5.0.55"),sQuery(id+"F0.wireOp",EDGE,"E3.5.0.56"),sQuery(id+"F0.wireOp",EDGE,"E3.5.0.57"),sQuery(id+"F0.wireOp",EDGE,"E3.5.0.58"),sQuery(id+"F0.wireOp",EDGE,"E3.5.0.59"),sQuery(id+"F0.wireOp",EDGE,"E3.6.0.0"),sQuery(id+"F0.wireOp",EDGE,"E3.6.0.1"),sQuery(id+"F0.wireOp",EDGE,"E3.6.0.2"),sQuery(id+"F0.wireOp",EDGE,"E3.6.0.3"),sQuery(id+"F0.wireOp",EDGE,"E3.6.0.4"),sQuery(id+"F0.wireOp",EDGE,"E3.6.0.5"),sQuery(id+"F0.wireOp",EDGE,"E3.6.0.6"),sQuery(id+"F0.wireOp",EDGE,"E3.6.0.7"),sQuery(id+"F0.wireOp",EDGE,"E3.6.0.8"),sQuery(id+"F0.wireOp",EDGE,"E3.6.0.9"),sQuery(id+"F0.wireOp",EDGE,"E3.6.0.10"),sQuery(id+"F0.wireOp",EDGE,"E3.6.0.11"),sQuery(id+"F0.wireOp",EDGE,"E3.6.0.12"),sQuery(id+"F0.wireOp",EDGE,"E3.6.0.13"),sQuery(id+"F0.wireOp",EDGE,"E3.6.0.14"),sQuery(id+"F0.wireOp",EDGE,"E3.6.0.15"),sQuery(id+"F0.wireOp",EDGE,"E3.6.0.16"),sQuery(id+"F0.wireOp",EDGE,"E3.6.0.17"),sQuery(id+"F0.wireOp",EDGE,"E3.6.0.18"),sQuery(id+"F0.wireOp",EDGE,"E3.6.0.19"),sQuery(id+"F0.wireOp",EDGE,"E3.6.0.20"),sQuery(id+"F0.wireOp",EDGE,"E3.6.0.21"),sQuery(id+"F0.wireOp",EDGE,"E3.6.0.22"),sQuery(id+"F0.wireOp",EDGE,"E3.6.0.23"),sQuery(id+"F0.wireOp",EDGE,"E3.6.0.24"),sQuery(id+"F0.wireOp",EDGE,"E3.6.0.25"),sQuery(id+"F0.wireOp",EDGE,"E3.6.0.26"),sQuery(id+"F0.wireOp",EDGE,"E3.6.0.27"),sQuery(id+"F0.wireOp",EDGE,"E3.6.0.28"),sQuery(id+"F0.wireOp",EDGE,"E3.6.0.29"),sQuery(id+"F0.wireOp",EDGE,"E3.6.0.30"),sQuery(id+"F0.wireOp",EDGE,"E3.6.0.31"),sQuery(id+"F0.wireOp",EDGE,"E3.6.0.32"),sQuery(id+"F0.wireOp",EDGE,"E3.6.0.33"),sQuery(id+"F0.wireOp",EDGE,"E3.6.0.34"),sQuery(id+"F0.wireOp",EDGE,"E3.6.0.35"),sQuery(id+"F0.wireOp",EDGE,"E3.6.0.36"),sQuery(id+"F0.wireOp",EDGE,"E3.6.0.37"),sQuery(id+"F0.wireOp",EDGE,"E3.6.0.38"),sQuery(id+"F0.wireOp",EDGE,"E3.6.0.39"),sQuery(id+"F0.wireOp",EDGE,"E3.6.0.40"),sQuery(id+"F0.wireOp",EDGE,"E3.6.0.41"),sQuery(id+"F0.wireOp",EDGE,"E3.6.0.42"),sQuery(id+"F0.wireOp",EDGE,"E3.6.0.43"),sQuery(id+"F0.wireOp",EDGE,"E3.6.0.44"),sQuery(id+"F0.wireOp",EDGE,"E3.6.0.45"),sQuery(id+"F0.wireOp",EDGE,"E3.6.0.46"),sQuery(id+"F0.wireOp",EDGE,"E3.6.0.47"),sQuery(id+"F0.wireOp",EDGE,"E3.6.0.48"),sQuery(id+"F0.wireOp",EDGE,"E3.6.0.49"),sQuery(id+"F0.wireOp",EDGE,"E3.6.0.50"),sQuery(id+"F0.wireOp",EDGE,"E3.6.0.51"),sQuery(id+"F0.wireOp",EDGE,"E3.6.0.52"),sQuery(id+"F0.wireOp",EDGE,"E3.6.0.53"),sQuery(id+"F0.wireOp",EDGE,"E3.6.0.54"),sQuery(id+"F0.wireOp",EDGE,"E3.6.0.55"),sQuery(id+"F0.wireOp",EDGE,"E3.6.0.56"),sQuery(id+"F0.wireOp",EDGE,"E3.6.0.57"),sQuery(id+"F0.wireOp",EDGE,"E3.6.0.58"),sQuery(id+"F0.wireOp",EDGE,"E3.6.0.59"),sQuery(id+"F0.wireOp",EDGE,"E3.7.0.0"),sQuery(id+"F0.wireOp",EDGE,"E3.7.0.1"),sQuery(id+"F0.wireOp",EDGE,"E3.7.0.2"),sQuery(id+"F0.wireOp",EDGE,"E3.7.0.3"),sQuery(id+"F0.wireOp",EDGE,"E3.7.0.4"),sQuery(id+"F0.wireOp",EDGE,"E3.7.0.5"),sQuery(id+"F0.wireOp",EDGE,"E3.7.0.6"),sQuery(id+"F0.wireOp",EDGE,"E3.7.0.7"),sQuery(id+"F0.wireOp",EDGE,"E3.7.0.8"),sQuery(id+"F0.wireOp",EDGE,"E3.7.0.9"),sQuery(id+"F0.wireOp",EDGE,"E3.7.0.10"),sQuery(id+"F0.wireOp",EDGE,"E3.7.0.11"),sQuery(id+"F0.wireOp",EDGE,"E3.7.0.12"),sQuery(id+"F0.wireOp",EDGE,"E3.7.0.13"),sQuery(id+"F0.wireOp",EDGE,"E3.7.0.14"),sQuery(id+"F0.wireOp",EDGE,"E3.7.0.15"),sQuery(id+"F0.wireOp",EDGE,"E3.7.0.16"),sQuery(id+"F0.wireOp",EDGE,"E3.7.0.17"),sQuery(id+"F0.wireOp",EDGE,"E3.7.0.18"),sQuery(id+"F0.wireOp",EDGE,"E3.7.0.19"),sQuery(id+"F0.wireOp",EDGE,"E3.7.0.20"),sQuery(id+"F0.wireOp",EDGE,"E3.7.0.21"),sQuery(id+"F0.wireOp",EDGE,"E3.7.0.22"),sQuery(id+"F0.wireOp",EDGE,"E3.7.0.23"),sQuery(id+"F0.wireOp",EDGE,"E3.7.0.24"),sQuery(id+"F0.wireOp",EDGE,"E3.7.0.25"),sQuery(id+"F0.wireOp",EDGE,"E3.7.0.26"),sQuery(id+"F0.wireOp",EDGE,"E3.7.0.27"),sQuery(id+"F0.wireOp",EDGE,"E3.7.0.28"),sQuery(id+"F0.wireOp",EDGE,"E3.7.0.29"),sQuery(id+"F0.wireOp",EDGE,"E3.7.0.30"),sQuery(id+"F0.wireOp",EDGE,"E3.7.0.31"),sQuery(id+"F0.wireOp",EDGE,"E3.7.0.32"),sQuery(id+"F0.wireOp",EDGE,"E3.7.0.33"),sQuery(id+"F0.wireOp",EDGE,"E3.7.0.34"),sQuery(id+"F0.wireOp",EDGE,"E3.7.0.35"),sQuery(id+"F0.wireOp",EDGE,"E3.7.0.36"),sQuery(id+"F0.wireOp",EDGE,"E3.7.0.37"),sQuery(id+"F0.wireOp",EDGE,"E3.7.0.38"),sQuery(id+"F0.wireOp",EDGE,"E3.7.0.39"),sQuery(id+"F0.wireOp",EDGE,"E3.7.0.40"),sQuery(id+"F0.wireOp",EDGE,"E3.7.0.41"),sQuery(id+"F0.wireOp",EDGE,"E3.7.0.42"),sQuery(id+"F0.wireOp",EDGE,"E3.7.0.43"),sQuery(id+"F0.wireOp",EDGE,"E3.7.0.44"),sQuery(id+"F0.wireOp",EDGE,"E3.7.0.45"),sQuery(id+"F0.wireOp",EDGE,"E3.7.0.46"),sQuery(id+"F0.wireOp",EDGE,"E3.7.0.47"),sQuery(id+"F0.wireOp",EDGE,"E3.7.0.48"),sQuery(id+"F0.wireOp",EDGE,"E3.7.0.49"),sQuery(id+"F0.wireOp",EDGE,"E3.7.0.50"),sQuery(id+"F0.wireOp",EDGE,"E3.7.0.51"),sQuery(id+"F0.wireOp",EDGE,"E3.7.0.52"),sQuery(id+"F0.wireOp",EDGE,"E3.7.0.53"),sQuery(id+"F0.wireOp",EDGE,"E3.7.0.54"),sQuery(id+"F0.wireOp",EDGE,"E3.7.0.55"),sQuery(id+"F0.wireOp",EDGE,"E3.7.0.56"),sQuery(id+"F0.wireOp",EDGE,"E3.7.0.57"),sQuery(id+"F0.wireOp",EDGE,"E3.7.0.58"),sQuery(id+"F0.wireOp",EDGE,"E3.7.0.59"),sQuery(id+"F0.wireOp",EDGE,"E3.8.0.0"),sQuery(id+"F0.wireOp",EDGE,"E3.8.0.1"),sQuery(id+"F0.wireOp",EDGE,"E3.8.0.2"),sQuery(id+"F0.wireOp",EDGE,"E3.8.0.3"),sQuery(id+"F0.wireOp",EDGE,"E3.8.0.4"),sQuery(id+"F0.wireOp",EDGE,"E3.8.0.5"),sQuery(id+"F0.wireOp",EDGE,"E3.8.0.6"),sQuery(id+"F0.wireOp",EDGE,"E3.8.0.7"),sQuery(id+"F0.wireOp",EDGE,"E3.8.0.8"),sQuery(id+"F0.wireOp",EDGE,"E3.8.0.9"),sQuery(id+"F0.wireOp",EDGE,"E3.8.0.10"),sQuery(id+"F0.wireOp",EDGE,"E3.8.0.11"),sQuery(id+"F0.wireOp",EDGE,"E3.8.0.12"),sQuery(id+"F0.wireOp",EDGE,"E3.8.0.13"),sQuery(id+"F0.wireOp",EDGE,"E3.8.0.14"),sQuery(id+"F0.wireOp",EDGE,"E3.8.0.15"),sQuery(id+"F0.wireOp",EDGE,"E3.8.0.16"),sQuery(id+"F0.wireOp",EDGE,"E3.8.0.17"),sQuery(id+"F0.wireOp",EDGE,"E3.8.0.18"),sQuery(id+"F0.wireOp",EDGE,"E3.8.0.19"),sQuery(id+"F0.wireOp",EDGE,"E3.8.0.20"),sQuery(id+"F0.wireOp",EDGE,"E3.8.0.21"),sQuery(id+"F0.wireOp",EDGE,"E3.8.0.22"),sQuery(id+"F0.wireOp",EDGE,"E3.8.0.23"),sQuery(id+"F0.wireOp",EDGE,"E3.8.0.24"),sQuery(id+"F0.wireOp",EDGE,"E3.8.0.25"),sQuery(id+"F0.wireOp",EDGE,"E3.8.0.26"),sQuery(id+"F0.wireOp",EDGE,"E3.8.0.27"),sQuery(id+"F0.wireOp",EDGE,"E3.8.0.28"),sQuery(id+"F0.wireOp",EDGE,"E3.8.0.29"),sQuery(id+"F0.wireOp",EDGE,"E3.8.0.30"),sQuery(id+"F0.wireOp",EDGE,"E3.8.0.31"),sQuery(id+"F0.wireOp",EDGE,"E3.8.0.32"),sQuery(id+"F0.wireOp",EDGE,"E3.8.0.33"),sQuery(id+"F0.wireOp",EDGE,"E3.8.0.34"),sQuery(id+"F0.wireOp",EDGE,"E3.8.0.35"),sQuery(id+"F0.wireOp",EDGE,"E3.8.0.36"),sQuery(id+"F0.wireOp",EDGE,"E3.8.0.37"),sQuery(id+"F0.wireOp",EDGE,"E3.8.0.38"),sQuery(id+"F0.wireOp",EDGE,"E3.8.0.39"),sQuery(id+"F0.wireOp",EDGE,"E3.8.0.40"),sQuery(id+"F0.wireOp",EDGE,"E3.8.0.41"),sQuery(id+"F0.wireOp",EDGE,"E3.8.0.42"),sQuery(id+"F0.wireOp",EDGE,"E3.8.0.43"),sQuery(id+"F0.wireOp",EDGE,"E3.8.0.44"),sQuery(id+"F0.wireOp",EDGE,"E3.8.0.45"),sQuery(id+"F0.wireOp",EDGE,"E3.8.0.46"),sQuery(id+"F0.wireOp",EDGE,"E3.8.0.47"),sQuery(id+"F0.wireOp",EDGE,"E3.8.0.48"),sQuery(id+"F0.wireOp",EDGE,"E3.8.0.49"),sQuery(id+"F0.wireOp",EDGE,"E3.8.0.50"),sQuery(id+"F0.wireOp",EDGE,"E3.8.0.51"),sQuery(id+"F0.wireOp",EDGE,"E3.8.0.52"),sQuery(id+"F0.wireOp",EDGE,"E3.8.0.53"),sQuery(id+"F0.wireOp",EDGE,"E3.8.0.54"),sQuery(id+"F0.wireOp",EDGE,"E3.8.0.55"),sQuery(id+"F0.wireOp",EDGE,"E3.8.0.56"),sQuery(id+"F0.wireOp",EDGE,"E3.8.0.57"),sQuery(id+"F0.wireOp",EDGE,"E3.8.0.58"),sQuery(id+"F0.wireOp",EDGE,"E3.8.0.59"),sQuery(id+"F0.wireOp",EDGE,"E3.9.0.0"),sQuery(id+"F0.wireOp",EDGE,"E3.9.0.1"),sQuery(id+"F0.wireOp",EDGE,"E3.9.0.2"),sQuery(id+"F0.wireOp",EDGE,"E3.9.0.3"),sQuery(id+"F0.wireOp",EDGE,"E3.9.0.4"),sQuery(id+"F0.wireOp",EDGE,"E3.9.0.5"),sQuery(id+"F0.wireOp",EDGE,"E3.9.0.6"),sQuery(id+"F0.wireOp",EDGE,"E3.9.0.7"),sQuery(id+"F0.wireOp",EDGE,"E3.9.0.8"),sQuery(id+"F0.wireOp",EDGE,"E3.9.0.9"),sQuery(id+"F0.wireOp",EDGE,"E3.9.0.10"),sQuery(id+"F0.wireOp",EDGE,"E3.9.0.11"),sQuery(id+"F0.wireOp",EDGE,"E3.9.0.12"),sQuery(id+"F0.wireOp",EDGE,"E3.9.0.13"),sQuery(id+"F0.wireOp",EDGE,"E3.9.0.14"),sQuery(id+"F0.wireOp",EDGE,"E3.9.0.15"),sQuery(id+"F0.wireOp",EDGE,"E3.9.0.16"),sQuery(id+"F0.wireOp",EDGE,"E3.9.0.17"),sQuery(id+"F0.wireOp",EDGE,"E3.9.0.18"),sQuery(id+"F0.wireOp",EDGE,"E3.9.0.19"),sQuery(id+"F0.wireOp",EDGE,"E3.9.0.20"),sQuery(id+"F0.wireOp",EDGE,"E3.9.0.21"),sQuery(id+"F0.wireOp",EDGE,"E3.9.0.22"),sQuery(id+"F0.wireOp",EDGE,"E3.9.0.23"),sQuery(id+"F0.wireOp",EDGE,"E3.9.0.24"),sQuery(id+"F0.wireOp",EDGE,"E3.9.0.25"),sQuery(id+"F0.wireOp",EDGE,"E3.9.0.26"),sQuery(id+"F0.wireOp",EDGE,"E3.9.0.27"),sQuery(id+"F0.wireOp",EDGE,"E3.9.0.28"),sQuery(id+"F0.wireOp",EDGE,"E3.9.0.29"),sQuery(id+"F0.wireOp",EDGE,"E3.9.0.30"),sQuery(id+"F0.wireOp",EDGE,"E3.9.0.31"),sQuery(id+"F0.wireOp",EDGE,"E3.9.0.32"),sQuery(id+"F0.wireOp",EDGE,"E3.9.0.33"),sQuery(id+"F0.wireOp",EDGE,"E3.9.0.34"),sQuery(id+"F0.wireOp",EDGE,"E3.9.0.35"),sQuery(id+"F0.wireOp",EDGE,"E3.9.0.36"),sQuery(id+"F0.wireOp",EDGE,"E3.9.0.37"),sQuery(id+"F0.wireOp",EDGE,"E3.9.0.38"),sQuery(id+"F0.wireOp",EDGE,"E3.9.0.39"),sQuery(id+"F0.wireOp",EDGE,"E3.9.0.40"),sQuery(id+"F0.wireOp",EDGE,"E3.9.0.41"),sQuery(id+"F0.wireOp",EDGE,"E3.9.0.42"),sQuery(id+"F0.wireOp",EDGE,"E3.9.0.43"),sQuery(id+"F0.wireOp",EDGE,"E3.9.0.44"),sQuery(id+"F0.wireOp",EDGE,"E3.9.0.45"),sQuery(id+"F0.wireOp",EDGE,"E3.9.0.46"),sQuery(id+"F0.wireOp",EDGE,"E3.9.0.47"),sQuery(id+"F0.wireOp",EDGE,"E3.9.0.48"),sQuery(id+"F0.wireOp",EDGE,"E3.9.0.49"),sQuery(id+"F0.wireOp",EDGE,"E3.9.0.50"),sQuery(id+"F0.wireOp",EDGE,"E3.9.0.51"),sQuery(id+"F0.wireOp",EDGE,"E3.9.0.52"),sQuery(id+"F0.wireOp",EDGE,"E3.9.0.53"),sQuery(id+"F0.wireOp",EDGE,"E3.9.0.54"),sQuery(id+"F0.wireOp",EDGE,"E3.9.0.55"),sQuery(id+"F0.wireOp",EDGE,"E3.9.0.56"),sQuery(id+"F0.wireOp",EDGE,"E3.9.0.57"),sQuery(id+"F0.wireOp",EDGE,"E3.9.0.58"),sQuery(id+"F0.wireOp",EDGE,"E3.9.0.59"),sQuery(id+"F0.wireOp",EDGE,"E3.10.0.0"),sQuery(id+"F0.wireOp",EDGE,"E3.10.0.1"),sQuery(id+"F0.wireOp",EDGE,"E3.10.0.2"),sQuery(id+"F0.wireOp",EDGE,"E3.10.0.3"),sQuery(id+"F0.wireOp",EDGE,"E3.10.0.4"),sQuery(id+"F0.wireOp",EDGE,"E3.10.0.5"),sQuery(id+"F0.wireOp",EDGE,"E3.10.0.6"),sQuery(id+"F0.wireOp",EDGE,"E3.10.0.7"),sQuery(id+"F0.wireOp",EDGE,"E3.10.0.8"),sQuery(id+"F0.wireOp",EDGE,"E3.10.0.9"),sQuery(id+"F0.wireOp",EDGE,"E3.10.0.10"),sQuery(id+"F0.wireOp",EDGE,"E3.10.0.11"),sQuery(id+"F0.wireOp",EDGE,"E3.10.0.12"),sQuery(id+"F0.wireOp",EDGE,"E3.10.0.13"),sQuery(id+"F0.wireOp",EDGE,"E3.10.0.14"),sQuery(id+"F0.wireOp",EDGE,"E3.10.0.15"),sQuery(id+"F0.wireOp",EDGE,"E3.10.0.16"),sQuery(id+"F0.wireOp",EDGE,"E3.10.0.17"),sQuery(id+"F0.wireOp",EDGE,"E3.10.0.18"),sQuery(id+"F0.wireOp",EDGE,"E3.10.0.19"),sQuery(id+"F0.wireOp",EDGE,"E3.10.0.20"),sQuery(id+"F0.wireOp",EDGE,"E3.10.0.21"),sQuery(id+"F0.wireOp",EDGE,"E3.10.0.22"),sQuery(id+"F0.wireOp",EDGE,"E3.10.0.23"),sQuery(id+"F0.wireOp",EDGE,"E3.10.0.24"),sQuery(id+"F0.wireOp",EDGE,"E3.10.0.25"),sQuery(id+"F0.wireOp",EDGE,"E3.10.0.26"),sQuery(id+"F0.wireOp",EDGE,"E3.10.0.27"),sQuery(id+"F0.wireOp",EDGE,"E3.10.0.28"),sQuery(id+"F0.wireOp",EDGE,"E3.10.0.29"),sQuery(id+"F0.wireOp",EDGE,"E3.10.0.30"),sQuery(id+"F0.wireOp",EDGE,"E3.10.0.31"),sQuery(id+"F0.wireOp",EDGE,"E3.10.0.32"),sQuery(id+"F0.wireOp",EDGE,"E3.10.0.33"),sQuery(id+"F0.wireOp",EDGE,"E3.10.0.34"),sQuery(id+"F0.wireOp",EDGE,"E3.10.0.35"),sQuery(id+"F0.wireOp",EDGE,"E3.10.0.36"),sQuery(id+"F0.wireOp",EDGE,"E3.10.0.37"),sQuery(id+"F0.wireOp",EDGE,"E3.10.0.38"),sQuery(id+"F0.wireOp",EDGE,"E3.10.0.39"),sQuery(id+"F0.wireOp",EDGE,"E3.10.0.40"),sQuery(id+"F0.wireOp",EDGE,"E3.10.0.41"),sQuery(id+"F0.wireOp",EDGE,"E3.10.0.42"),sQuery(id+"F0.wireOp",EDGE,"E3.10.0.43"),sQuery(id+"F0.wireOp",EDGE,"E3.10.0.44"),sQuery(id+"F0.wireOp",EDGE,"E3.10.0.45"),sQuery(id+"F0.wireOp",EDGE,"E3.10.0.46"),sQuery(id+"F0.wireOp",EDGE,"E3.10.0.47"),sQuery(id+"F0.wireOp",EDGE,"E3.10.0.48"),sQuery(id+"F0.wireOp",EDGE,"E3.10.0.49"),sQuery(id+"F0.wireOp",EDGE,"E3.10.0.50"),sQuery(id+"F0.wireOp",EDGE,"E3.10.0.51"),sQuery(id+"F0.wireOp",EDGE,"E3.10.0.52"),sQuery(id+"F0.wireOp",EDGE,"E3.10.0.53"),sQuery(id+"F0.wireOp",EDGE,"E3.10.0.54"),sQuery(id+"F0.wireOp",EDGE,"E3.10.0.55"),sQuery(id+"F0.wireOp",EDGE,"E3.10.0.56"),sQuery(id+"F0.wireOp",EDGE,"E3.10.0.57"),sQuery(id+"F0.wireOp",EDGE,"E3.10.0.58"),sQuery(id+"F0.wireOp",EDGE,"E3.10.0.59"),sQuery(id+"F0.wireOp",EDGE,"E3.11.0.0"),sQuery(id+"F0.wireOp",EDGE,"E3.11.0.1"),sQuery(id+"F0.wireOp",EDGE,"E3.11.0.2"),sQuery(id+"F0.wireOp",EDGE,"E3.11.0.3"),sQuery(id+"F0.wireOp",EDGE,"E3.11.0.4"),sQuery(id+"F0.wireOp",EDGE,"E3.11.0.5"),sQuery(id+"F0.wireOp",EDGE,"E3.11.0.6"),sQuery(id+"F0.wireOp",EDGE,"E3.11.0.7"),sQuery(id+"F0.wireOp",EDGE,"E3.11.0.8"),sQuery(id+"F0.wireOp",EDGE,"E3.11.0.9"),sQuery(id+"F0.wireOp",EDGE,"E3.11.0.10"),sQuery(id+"F0.wireOp",EDGE,"E3.11.0.11"),sQuery(id+"F0.wireOp",EDGE,"E3.11.0.12"),sQuery(id+"F0.wireOp",EDGE,"E3.11.0.13"),sQuery(id+"F0.wireOp",EDGE,"E3.11.0.14"),sQuery(id+"F0.wireOp",EDGE,"E3.11.0.15"),sQuery(id+"F0.wireOp",EDGE,"E3.11.0.16"),sQuery(id+"F0.wireOp",EDGE,"E3.11.0.17"),sQuery(id+"F0.wireOp",EDGE,"E3.11.0.18"),sQuery(id+"F0.wireOp",EDGE,"E3.11.0.19"),sQuery(id+"F0.wireOp",EDGE,"E3.11.0.20"),sQuery(id+"F0.wireOp",EDGE,"E3.11.0.21"),sQuery(id+"F0.wireOp",EDGE,"E3.11.0.22"),sQuery(id+"F0.wireOp",EDGE,"E3.11.0.23"),sQuery(id+"F0.wireOp",EDGE,"E3.11.0.24"),sQuery(id+"F0.wireOp",EDGE,"E3.11.0.25"),sQuery(id+"F0.wireOp",EDGE,"E3.11.0.26"),sQuery(id+"F0.wireOp",EDGE,"E3.11.0.27"),sQuery(id+"F0.wireOp",EDGE,"E3.11.0.28"),sQuery(id+"F0.wireOp",EDGE,"E3.11.0.29"),sQuery(id+"F0.wireOp",EDGE,"E3.11.0.30"),sQuery(id+"F0.wireOp",EDGE,"E3.11.0.31"),sQuery(id+"F0.wireOp",EDGE,"E3.11.0.32"),sQuery(id+"F0.wireOp",EDGE,"E3.11.0.33"),sQuery(id+"F0.wireOp",EDGE,"E3.11.0.34"),sQuery(id+"F0.wireOp",EDGE,"E3.11.0.35"),sQuery(id+"F0.wireOp",EDGE,"E3.11.0.36"),sQuery(id+"F0.wireOp",EDGE,"E3.11.0.37"),sQuery(id+"F0.wireOp",EDGE,"E3.11.0.38"),sQuery(id+"F0.wireOp",EDGE,"E3.11.0.39"),sQuery(id+"F0.wireOp",EDGE,"E3.11.0.40"),sQuery(id+"F0.wireOp",EDGE,"E3.11.0.41"),sQuery(id+"F0.wireOp",EDGE,"E3.11.0.42"),sQuery(id+"F0.wireOp",EDGE,"E3.11.0.43"),sQuery(id+"F0.wireOp",EDGE,"E3.11.0.44"),sQuery(id+"F0.wireOp",EDGE,"E3.11.0.45"),sQuery(id+"F0.wireOp",EDGE,"E3.11.0.46"),sQuery(id+"F0.wireOp",EDGE,"E3.11.0.47"),sQuery(id+"F0.wireOp",EDGE,"E3.11.0.48"),sQuery(id+"F0.wireOp",EDGE,"E3.11.0.49"),sQuery(id+"F0.wireOp",EDGE,"E3.11.0.50"),sQuery(id+"F0.wireOp",EDGE,"E3.11.0.51"),sQuery(id+"F0.wireOp",EDGE,"E3.11.0.52"),sQuery(id+"F0.wireOp",EDGE,"E3.11.0.53"),sQuery(id+"F0.wireOp",EDGE,"E3.11.0.54"),sQuery(id+"F0.wireOp",EDGE,"E3.11.0.55"),sQuery(id+"F0.wireOp",EDGE,"E3.11.0.56"),sQuery(id+"F0.wireOp",EDGE,"E3.11.0.57"),sQuery(id+"F0.wireOp",EDGE,"E3.11.0.58"),sQuery(id+"F0.wireOp",EDGE,"E3.11.0.59"),sQuery(id+"F0.wireOp",EDGE,"E3.12.0.0"),sQuery(id+"F0.wireOp",EDGE,"E3.12.0.1"),sQuery(id+"F0.wireOp",EDGE,"E3.12.0.2"),sQuery(id+"F0.wireOp",EDGE,"E3.12.0.3"),sQuery(id+"F0.wireOp",EDGE,"E3.12.0.4"),sQuery(id+"F0.wireOp",EDGE,"E3.12.0.5"),sQuery(id+"F0.wireOp",EDGE,"E3.12.0.6"),sQuery(id+"F0.wireOp",EDGE,"E3.12.0.7"),sQuery(id+"F0.wireOp",EDGE,"E3.12.0.8"),sQuery(id+"F0.wireOp",EDGE,"E3.12.0.9"),sQuery(id+"F0.wireOp",EDGE,"E3.12.0.10"),sQuery(id+"F0.wireOp",EDGE,"E3.12.0.11"),sQuery(id+"F0.wireOp",EDGE,"E3.12.0.12"),sQuery(id+"F0.wireOp",EDGE,"E3.12.0.13"),sQuery(id+"F0.wireOp",EDGE,"E3.12.0.14"),sQuery(id+"F0.wireOp",EDGE,"E3.12.0.15"),sQuery(id+"F0.wireOp",EDGE,"E3.12.0.16"),sQuery(id+"F0.wireOp",EDGE,"E3.12.0.17"),sQuery(id+"F0.wireOp",EDGE,"E3.12.0.18"),sQuery(id+"F0.wireOp",EDGE,"E3.12.0.19"),sQuery(id+"F0.wireOp",EDGE,"E3.12.0.20"),sQuery(id+"F0.wireOp",EDGE,"E3.12.0.21"),sQuery(id+"F0.wireOp",EDGE,"E3.12.0.22"),sQuery(id+"F0.wireOp",EDGE,"E3.12.0.23"),sQuery(id+"F0.wireOp",EDGE,"E3.12.0.24"),sQuery(id+"F0.wireOp",EDGE,"E3.12.0.25"),sQuery(id+"F0.wireOp",EDGE,"E3.12.0.26"),sQuery(id+"F0.wireOp",EDGE,"E3.12.0.27"),sQuery(id+"F0.wireOp",EDGE,"E3.12.0.28"),sQuery(id+"F0.wireOp",EDGE,"E3.12.0.29"),sQuery(id+"F0.wireOp",EDGE,"E3.12.0.30"),sQuery(id+"F0.wireOp",EDGE,"E3.12.0.31"),sQuery(id+"F0.wireOp",EDGE,"E3.12.0.32"),sQuery(id+"F0.wireOp",EDGE,"E3.12.0.33"),sQuery(id+"F0.wireOp",EDGE,"E3.12.0.34"),sQuery(id+"F0.wireOp",EDGE,"E3.12.0.35"),sQuery(id+"F0.wireOp",EDGE,"E3.12.0.36"),sQuery(id+"F0.wireOp",EDGE,"E3.12.0.37"),sQuery(id+"F0.wireOp",EDGE,"E3.12.0.38"),sQuery(id+"F0.wireOp",EDGE,"E3.12.0.39"),sQuery(id+"F0.wireOp",EDGE,"E3.12.0.40"),sQuery(id+"F0.wireOp",EDGE,"E3.12.0.41"),sQuery(id+"F0.wireOp",EDGE,"E3.12.0.42"),sQuery(id+"F0.wireOp",EDGE,"E3.12.0.43"),sQuery(id+"F0.wireOp",EDGE,"E3.12.0.44"),sQuery(id+"F0.wireOp",EDGE,"E3.12.0.45"),sQuery(id+"F0.wireOp",EDGE,"E3.12.0.46"),sQuery(id+"F0.wireOp",EDGE,"E3.12.0.47"),sQuery(id+"F0.wireOp",EDGE,"E3.12.0.48"),sQuery(id+"F0.wireOp",EDGE,"E3.12.0.49"),sQuery(id+"F0.wireOp",EDGE,"E3.12.0.50"),sQuery(id+"F0.wireOp",EDGE,"E3.12.0.51"),sQuery(id+"F0.wireOp",EDGE,"E3.12.0.52"),sQuery(id+"F0.wireOp",EDGE,"E3.12.0.53"),sQuery(id+"F0.wireOp",EDGE,"E3.12.0.54"),sQuery(id+"F0.wireOp",EDGE,"E3.12.0.55"),sQuery(id+"F0.wireOp",EDGE,"E3.12.0.56"),sQuery(id+"F0.wireOp",EDGE,"E3.12.0.57"),sQuery(id+"F0.wireOp",EDGE,"E3.12.0.58"),sQuery(id+"F0.wireOp",EDGE,"E3.12.0.59"),sQuery(id+"F0.wireOp",EDGE,"E3.13.0.0"),sQuery(id+"F0.wireOp",EDGE,"E3.13.0.1"),sQuery(id+"F0.wireOp",EDGE,"E3.13.0.2"),sQuery(id+"F0.wireOp",EDGE,"E3.13.0.3"),sQuery(id+"F0.wireOp",EDGE,"E3.13.0.4"),sQuery(id+"F0.wireOp",EDGE,"E3.13.0.5"),sQuery(id+"F0.wireOp",EDGE,"E3.13.0.6"),sQuery(id+"F0.wireOp",EDGE,"E3.13.0.7"),sQuery(id+"F0.wireOp",EDGE,"E3.13.0.8"),sQuery(id+"F0.wireOp",EDGE,"E3.13.0.9"),sQuery(id+"F0.wireOp",EDGE,"E3.13.0.10"),sQuery(id+"F0.wireOp",EDGE,"E3.13.0.11"),sQuery(id+"F0.wireOp",EDGE,"E3.13.0.12"),sQuery(id+"F0.wireOp",EDGE,"E3.13.0.13"),sQuery(id+"F0.wireOp",EDGE,"E3.13.0.14"),sQuery(id+"F0.wireOp",EDGE,"E3.13.0.15"),sQuery(id+"F0.wireOp",EDGE,"E3.13.0.16"),sQuery(id+"F0.wireOp",EDGE,"E3.13.0.17"),sQuery(id+"F0.wireOp",EDGE,"E3.13.0.18"),sQuery(id+"F0.wireOp",EDGE,"E3.13.0.19"),sQuery(id+"F0.wireOp",EDGE,"E3.13.0.20"),sQuery(id+"F0.wireOp",EDGE,"E3.13.0.21"),sQuery(id+"F0.wireOp",EDGE,"E3.13.0.22"),sQuery(id+"F0.wireOp",EDGE,"E3.13.0.23"),sQuery(id+"F0.wireOp",EDGE,"E3.13.0.24"),sQuery(id+"F0.wireOp",EDGE,"E3.13.0.25"),sQuery(id+"F0.wireOp",EDGE,"E3.13.0.26"),sQuery(id+"F0.wireOp",EDGE,"E3.13.0.27"),sQuery(id+"F0.wireOp",EDGE,"E3.13.0.28"),sQuery(id+"F0.wireOp",EDGE,"E3.13.0.29"),sQuery(id+"F0.wireOp",EDGE,"E3.13.0.30"),sQuery(id+"F0.wireOp",EDGE,"E3.13.0.31"),sQuery(id+"F0.wireOp",EDGE,"E3.13.0.32"),sQuery(id+"F0.wireOp",EDGE,"E3.13.0.33"),sQuery(id+"F0.wireOp",EDGE,"E3.13.0.34"),sQuery(id+"F0.wireOp",EDGE,"E3.13.0.35"),sQuery(id+"F0.wireOp",EDGE,"E3.13.0.36"),sQuery(id+"F0.wireOp",EDGE,"E3.13.0.37"),sQuery(id+"F0.wireOp",EDGE,"E3.13.0.38"),sQuery(id+"F0.wireOp",EDGE,"E3.13.0.39"),sQuery(id+"F0.wireOp",EDGE,"E3.13.0.40"),sQuery(id+"F0.wireOp",EDGE,"E3.13.0.41"),sQuery(id+"F0.wireOp",EDGE,"E3.13.0.42"),sQuery(id+"F0.wireOp",EDGE,"E3.13.0.43"),sQuery(id+"F0.wireOp",EDGE,"E3.13.0.44"),sQuery(id+"F0.wireOp",EDGE,"E3.13.0.45"),sQuery(id+"F0.wireOp",EDGE,"E3.13.0.46"),sQuery(id+"F0.wireOp",EDGE,"E3.13.0.47"),sQuery(id+"F0.wireOp",EDGE,"E3.13.0.48"),sQuery(id+"F0.wireOp",EDGE,"E3.13.0.49"),sQuery(id+"F0.wireOp",EDGE,"E3.13.0.50"),sQuery(id+"F0.wireOp",EDGE,"E3.13.0.51"),sQuery(id+"F0.wireOp",EDGE,"E3.13.0.52"),sQuery(id+"F0.wireOp",EDGE,"E3.13.0.53"),sQuery(id+"F0.wireOp",EDGE,"E3.13.0.54"),sQuery(id+"F0.wireOp",EDGE,"E3.13.0.55"),sQuery(id+"F0.wireOp",EDGE,"E3.13.0.56"),sQuery(id+"F0.wireOp",EDGE,"E3.13.0.57"),sQuery(id+"F0.wireOp",EDGE,"E3.13.0.58"),sQuery(id+"F0.wireOp",EDGE,"E3.13.0.59"),sQuery(id+"F0.wireOp",EDGE,"E3.14.0.0"),sQuery(id+"F0.wireOp",EDGE,"E3.14.0.1"),sQuery(id+"F0.wireOp",EDGE,"E3.14.0.2"),sQuery(id+"F0.wireOp",EDGE,"E3.14.0.3"),sQuery(id+"F0.wireOp",EDGE,"E3.14.0.4"),sQuery(id+"F0.wireOp",EDGE,"E3.14.0.5"),sQuery(id+"F0.wireOp",EDGE,"E3.14.0.6"),sQuery(id+"F0.wireOp",EDGE,"E3.14.0.7"),sQuery(id+"F0.wireOp",EDGE,"E3.14.0.8"),sQuery(id+"F0.wireOp",EDGE,"E3.14.0.9"),sQuery(id+"F0.wireOp",EDGE,"E3.14.0.10"),sQuery(id+"F0.wireOp",EDGE,"E3.14.0.11"),sQuery(id+"F0.wireOp",EDGE,"E3.14.0.12"),sQuery(id+"F0.wireOp",EDGE,"E3.14.0.13"),sQuery(id+"F0.wireOp",EDGE,"E3.14.0.14"),sQuery(id+"F0.wireOp",EDGE,"E3.14.0.15"),sQuery(id+"F0.wireOp",EDGE,"E3.14.0.16"),sQuery(id+"F0.wireOp",EDGE,"E3.14.0.17"),sQuery(id+"F0.wireOp",EDGE,"E3.14.0.18"),sQuery(id+"F0.wireOp",EDGE,"E3.14.0.19"),sQuery(id+"F0.wireOp",EDGE,"E3.14.0.20"),sQuery(id+"F0.wireOp",EDGE,"E3.14.0.21"),sQuery(id+"F0.wireOp",EDGE,"E3.14.0.22"),sQuery(id+"F0.wireOp",EDGE,"E3.14.0.23"),sQuery(id+"F0.wireOp",EDGE,"E3.14.0.24"),sQuery(id+"F0.wireOp",EDGE,"E3.14.0.25"),sQuery(id+"F0.wireOp",EDGE,"E3.14.0.26"),sQuery(id+"F0.wireOp",EDGE,"E3.14.0.27"),sQuery(id+"F0.wireOp",EDGE,"E3.14.0.28"),sQuery(id+"F0.wireOp",EDGE,"E3.14.0.29"),sQuery(id+"F0.wireOp",EDGE,"E3.14.0.30"),sQuery(id+"F0.wireOp",EDGE,"E3.14.0.31"),sQuery(id+"F0.wireOp",EDGE,"E3.14.0.32"),sQuery(id+"F0.wireOp",EDGE,"E3.14.0.33"),sQuery(id+"F0.wireOp",EDGE,"E3.14.0.34"),sQuery(id+"F0.wireOp",EDGE,"E3.14.0.35"),sQuery(id+"F0.wireOp",EDGE,"E3.14.0.36"),sQuery(id+"F0.wireOp",EDGE,"E3.14.0.37"),sQuery(id+"F0.wireOp",EDGE,"E3.14.0.38"),sQuery(id+"F0.wireOp",EDGE,"E3.14.0.39"),sQuery(id+"F0.wireOp",EDGE,"E3.14.0.40"),sQuery(id+"F0.wireOp",EDGE,"E3.14.0.41"),sQuery(id+"F0.wireOp",EDGE,"E3.14.0.42"),sQuery(id+"F0.wireOp",EDGE,"E3.14.0.43"),sQuery(id+"F0.wireOp",EDGE,"E3.14.0.44"),sQuery(id+"F0.wireOp",EDGE,"E3.14.0.45"),sQuery(id+"F0.wireOp",EDGE,"E3.14.0.46"),sQuery(id+"F0.wireOp",EDGE,"E3.14.0.47"),sQuery(id+"F0.wireOp",EDGE,"E3.14.0.48"),sQuery(id+"F0.wireOp",EDGE,"E3.14.0.49"),sQuery(id+"F0.wireOp",EDGE,"E3.14.0.50"),sQuery(id+"F0.wireOp",EDGE,"E3.14.0.51"),sQuery(id+"F0.wireOp",EDGE,"E3.14.0.52"),sQuery(id+"F0.wireOp",EDGE,"E3.14.0.53"),sQuery(id+"F0.wireOp",EDGE,"E3.14.0.54"),sQuery(id+"F0.wireOp",EDGE,"E3.14.0.55"),sQuery(id+"F0.wireOp",EDGE,"E3.14.0.56"),sQuery(id+"F0.wireOp",EDGE,"E3.14.0.57"),sQuery(id+"F0.wireOp",EDGE,"E3.14.0.58"),sQuery(id+"F0.wireOp",EDGE,"E3.14.0.59"),sQuery(id+"F0.wireOp",EDGE,"E3.15.0.0"),sQuery(id+"F0.wireOp",EDGE,"E3.15.0.1"),sQuery(id+"F0.wireOp",EDGE,"E3.15.0.2"),sQuery(id+"F0.wireOp",EDGE,"E3.15.0.3"),sQuery(id+"F0.wireOp",EDGE,"E3.15.0.4"),sQuery(id+"F0.wireOp",EDGE,"E3.15.0.5"),sQuery(id+"F0.wireOp",EDGE,"E3.15.0.6"),sQuery(id+"F0.wireOp",EDGE,"E3.15.0.7"),sQuery(id+"F0.wireOp",EDGE,"E3.15.0.8"),sQuery(id+"F0.wireOp",EDGE,"E3.15.0.9"),sQuery(id+"F0.wireOp",EDGE,"E3.15.0.10"),sQuery(id+"F0.wireOp",EDGE,"E3.15.0.11"),sQuery(id+"F0.wireOp",EDGE,"E3.15.0.12"),sQuery(id+"F0.wireOp",EDGE,"E3.15.0.13"),sQuery(id+"F0.wireOp",EDGE,"E3.15.0.14"),sQuery(id+"F0.wireOp",EDGE,"E3.15.0.15"),sQuery(id+"F0.wireOp",EDGE,"E3.15.0.16"),sQuery(id+"F0.wireOp",EDGE,"E3.15.0.17"),sQuery(id+"F0.wireOp",EDGE,"E3.15.0.18"),sQuery(id+"F0.wireOp",EDGE,"E3.15.0.19"),sQuery(id+"F0.wireOp",EDGE,"E3.15.0.20"),sQuery(id+"F0.wireOp",EDGE,"E3.15.0.21"),sQuery(id+"F0.wireOp",EDGE,"E3.15.0.22"),sQuery(id+"F0.wireOp",EDGE,"E3.15.0.23"),sQuery(id+"F0.wireOp",EDGE,"E3.15.0.24"),sQuery(id+"F0.wireOp",EDGE,"E3.15.0.25"),sQuery(id+"F0.wireOp",EDGE,"E3.15.0.26"),sQuery(id+"F0.wireOp",EDGE,"E3.15.0.27"),sQuery(id+"F0.wireOp",EDGE,"E3.15.0.28"),sQuery(id+"F0.wireOp",EDGE,"E3.15.0.29"),sQuery(id+"F0.wireOp",EDGE,"E3.15.0.30"),sQuery(id+"F0.wireOp",EDGE,"E3.15.0.31"),sQuery(id+"F0.wireOp",EDGE,"E3.15.0.32"),sQuery(id+"F0.wireOp",EDGE,"E3.15.0.33"),sQuery(id+"F0.wireOp",EDGE,"E3.15.0.34"),sQuery(id+"F0.wireOp",EDGE,"E3.15.0.35"),sQuery(id+"F0.wireOp",EDGE,"E3.15.0.36"),sQuery(id+"F0.wireOp",EDGE,"E3.15.0.37"),sQuery(id+"F0.wireOp",EDGE,"E3.15.0.38"),sQuery(id+"F0.wireOp",EDGE,"E3.15.0.39"),sQuery(id+"F0.wireOp",EDGE,"E3.15.0.40"),sQuery(id+"F0.wireOp",EDGE,"E3.15.0.41"),sQuery(id+"F0.wireOp",EDGE,"E3.15.0.42"),sQuery(id+"F0.wireOp",EDGE,"E3.15.0.43"),sQuery(id+"F0.wireOp",EDGE,"E3.15.0.44"),sQuery(id+"F0.wireOp",EDGE,"E3.15.0.45"),sQuery(id+"F0.wireOp",EDGE,"E3.15.0.46"),sQuery(id+"F0.wireOp",EDGE,"E3.15.0.47"),sQuery(id+"F0.wireOp",EDGE,"E3.15.0.48"),sQuery(id+"F0.wireOp",EDGE,"E3.15.0.49"),sQuery(id+"F0.wireOp",EDGE,"E3.15.0.50"),sQuery(id+"F0.wireOp",EDGE,"E3.15.0.51"),sQuery(id+"F0.wireOp",EDGE,"E3.15.0.52"),sQuery(id+"F0.wireOp",EDGE,"E3.15.0.53"),sQuery(id+"F0.wireOp",EDGE,"E3.15.0.54"),sQuery(id+"F0.wireOp",EDGE,"E3.15.0.55"),sQuery(id+"F0.wireOp",EDGE,"E3.15.0.56"),sQuery(id+"F0.wireOp",EDGE,"E3.15.0.57"),sQuery(id+"F0.wireOp",EDGE,"E3.15.0.58"),sQuery(id+"F0.wireOp",EDGE,"E3.15.0.59"),sQuery(id+"F0.wireOp",EDGE,"E3.16.0.0"),sQuery(id+"F0.wireOp",EDGE,"E3.16.0.1"),sQuery(id+"F0.wireOp",EDGE,"E3.16.0.2"),sQuery(id+"F0.wireOp",EDGE,"E3.16.0.3"),sQuery(id+"F0.wireOp",EDGE,"E3.16.0.4"),sQuery(id+"F0.wireOp",EDGE,"E3.16.0.5"),sQuery(id+"F0.wireOp",EDGE,"E3.16.0.6"),sQuery(id+"F0.wireOp",EDGE,"E3.16.0.7"),sQuery(id+"F0.wireOp",EDGE,"E3.16.0.8"),sQuery(id+"F0.wireOp",EDGE,"E3.16.0.9"),sQuery(id+"F0.wireOp",EDGE,"E3.16.0.10"),sQuery(id+"F0.wireOp",EDGE,"E3.16.0.11"),sQuery(id+"F0.wireOp",EDGE,"E3.16.0.12"),sQuery(id+"F0.wireOp",EDGE,"E3.16.0.13"),sQuery(id+"F0.wireOp",EDGE,"E3.16.0.14"),sQuery(id+"F0.wireOp",EDGE,"E3.16.0.15"),sQuery(id+"F0.wireOp",EDGE,"E3.16.0.16"),sQuery(id+"F0.wireOp",EDGE,"E3.16.0.17"),sQuery(id+"F0.wireOp",EDGE,"E3.16.0.18"),sQuery(id+"F0.wireOp",EDGE,"E3.16.0.19"),sQuery(id+"F0.wireOp",EDGE,"E3.16.0.20"),sQuery(id+"F0.wireOp",EDGE,"E3.16.0.21"),sQuery(id+"F0.wireOp",EDGE,"E3.16.0.22"),sQuery(id+"F0.wireOp",EDGE,"E3.16.0.23"),sQuery(id+"F0.wireOp",EDGE,"E3.16.0.24"),sQuery(id+"F0.wireOp",EDGE,"E3.16.0.25"),sQuery(id+"F0.wireOp",EDGE,"E3.16.0.26"),sQuery(id+"F0.wireOp",EDGE,"E3.16.0.27"),sQuery(id+"F0.wireOp",EDGE,"E3.16.0.28"),sQuery(id+"F0.wireOp",EDGE,"E3.16.0.29"),sQuery(id+"F0.wireOp",EDGE,"E3.16.0.30"),sQuery(id+"F0.wireOp",EDGE,"E3.16.0.31"),sQuery(id+"F0.wireOp",EDGE,"E3.16.0.32"),sQuery(id+"F0.wireOp",EDGE,"E3.16.0.33"),sQuery(id+"F0.wireOp",EDGE,"E3.16.0.34"),sQuery(id+"F0.wireOp",EDGE,"E3.16.0.35"),sQuery(id+"F0.wireOp",EDGE,"E3.16.0.36"),sQuery(id+"F0.wireOp",EDGE,"E3.16.0.37"),sQuery(id+"F0.wireOp",EDGE,"E3.16.0.38"),sQuery(id+"F0.wireOp",EDGE,"E3.16.0.39"),sQuery(id+"F0.wireOp",EDGE,"E3.16.0.40"),sQuery(id+"F0.wireOp",EDGE,"E3.16.0.41"),sQuery(id+"F0.wireOp",EDGE,"E3.16.0.42"),sQuery(id+"F0.wireOp",EDGE,"E3.16.0.43"),sQuery(id+"F0.wireOp",EDGE,"E3.16.0.44"),sQuery(id+"F0.wireOp",EDGE,"E3.16.0.45"),sQuery(id+"F0.wireOp",EDGE,"E3.16.0.46"),sQuery(id+"F0.wireOp",EDGE,"E3.16.0.47"),sQuery(id+"F0.wireOp",EDGE,"E3.16.0.48"),sQuery(id+"F0.wireOp",EDGE,"E3.16.0.49"),sQuery(id+"F0.wireOp",EDGE,"E3.16.0.50"),sQuery(id+"F0.wireOp",EDGE,"E3.16.0.51"),sQuery(id+"F0.wireOp",EDGE,"E3.16.0.52"),sQuery(id+"F0.wireOp",EDGE,"E3.16.0.53"),sQuery(id+"F0.wireOp",EDGE,"E3.16.0.54"),sQuery(id+"F0.wireOp",EDGE,"E3.16.0.55"),sQuery(id+"F0.wireOp",EDGE,"E3.16.0.56"),sQuery(id+"F0.wireOp",EDGE,"E3.16.0.57"),sQuery(id+"F0.wireOp",EDGE,"E3.16.0.58"),sQuery(id+"F0.wireOp",EDGE,"E3.16.0.59"),sQuery(id+"F0.wireOp",EDGE,"E3.17.0.0"),sQuery(id+"F0.wireOp",EDGE,"E3.17.0.1"),sQuery(id+"F0.wireOp",EDGE,"E3.17.0.2"),sQuery(id+"F0.wireOp",EDGE,"E3.17.0.3"),sQuery(id+"F0.wireOp",EDGE,"E3.17.0.4"),sQuery(id+"F0.wireOp",EDGE,"E3.17.0.5"),sQuery(id+"F0.wireOp",EDGE,"E3.17.0.6"),sQuery(id+"F0.wireOp",EDGE,"E3.17.0.7"),sQuery(id+"F0.wireOp",EDGE,"E3.17.0.8"),sQuery(id+"F0.wireOp",EDGE,"E3.17.0.9"),sQuery(id+"F0.wireOp",EDGE,"E3.17.0.10"),sQuery(id+"F0.wireOp",EDGE,"E3.17.0.11"),sQuery(id+"F0.wireOp",EDGE,"E3.17.0.12"),sQuery(id+"F0.wireOp",EDGE,"E3.17.0.13"),sQuery(id+"F0.wireOp",EDGE,"E3.17.0.14"),sQuery(id+"F0.wireOp",EDGE,"E3.17.0.15"),sQuery(id+"F0.wireOp",EDGE,"E3.17.0.16"),sQuery(id+"F0.wireOp",EDGE,"E3.17.0.17"),sQuery(id+"F0.wireOp",EDGE,"E3.17.0.18"),sQuery(id+"F0.wireOp",EDGE,"E3.17.0.19"),sQuery(id+"F0.wireOp",EDGE,"E3.17.0.20"),sQuery(id+"F0.wireOp",EDGE,"E3.17.0.21"),sQuery(id+"F0.wireOp",EDGE,"E3.17.0.22"),sQuery(id+"F0.wireOp",EDGE,"E3.17.0.23"),sQuery(id+"F0.wireOp",EDGE,"E3.17.0.24"),sQuery(id+"F0.wireOp",EDGE,"E3.17.0.25"),sQuery(id+"F0.wireOp",EDGE,"E3.17.0.26"),sQuery(id+"F0.wireOp",EDGE,"E3.17.0.27"),sQuery(id+"F0.wireOp",EDGE,"E3.17.0.28"),sQuery(id+"F0.wireOp",EDGE,"E3.17.0.29"),sQuery(id+"F0.wireOp",EDGE,"E3.17.0.30"),sQuery(id+"F0.wireOp",EDGE,"E3.17.0.31"),sQuery(id+"F0.wireOp",EDGE,"E3.17.0.32"),sQuery(id+"F0.wireOp",EDGE,"E3.17.0.33"),sQuery(id+"F0.wireOp",EDGE,"E3.17.0.34"),sQuery(id+"F0.wireOp",EDGE,"E3.17.0.35"),sQuery(id+"F0.wireOp",EDGE,"E3.17.0.36"),sQuery(id+"F0.wireOp",EDGE,"E3.17.0.37"),sQuery(id+"F0.wireOp",EDGE,"E3.17.0.38"),sQuery(id+"F0.wireOp",EDGE,"E3.17.0.39"),sQuery(id+"F0.wireOp",EDGE,"E3.17.0.40"),sQuery(id+"F0.wireOp",EDGE,"E3.17.0.41"),sQuery(id+"F0.wireOp",EDGE,"E3.17.0.42"),sQuery(id+"F0.wireOp",EDGE,"E3.17.0.43"),sQuery(id+"F0.wireOp",EDGE,"E3.17.0.44"),sQuery(id+"F0.wireOp",EDGE,"E3.17.0.45"),sQuery(id+"F0.wireOp",EDGE,"E3.17.0.46"),sQuery(id+"F0.wireOp",EDGE,"E3.17.0.47"),sQuery(id+"F0.wireOp",EDGE,"E3.17.0.48"),sQuery(id+"F0.wireOp",EDGE,"E3.17.0.49"),sQuery(id+"F0.wireOp",EDGE,"E3.17.0.50"),sQuery(id+"F0.wireOp",EDGE,"E3.17.0.51"),sQuery(id+"F0.wireOp",EDGE,"E3.17.0.52"),sQuery(id+"F0.wireOp",EDGE,"E3.17.0.53"),sQuery(id+"F0.wireOp",EDGE,"E3.17.0.54"),sQuery(id+"F0.wireOp",EDGE,"E3.17.0.55"),sQuery(id+"F0.wireOp",EDGE,"E3.17.0.56"),sQuery(id+"F0.wireOp",EDGE,"E3.17.0.57"),sQuery(id+"F0.wireOp",EDGE,"E3.17.0.58"),sQuery(id+"F0.wireOp",EDGE,"E3.17.0.59"),sQuery(id+"F0.wireOp",EDGE,"E3.18.0.0"),sQuery(id+"F0.wireOp",EDGE,"E3.18.0.1"),sQuery(id+"F0.wireOp",EDGE,"E3.18.0.2"),sQuery(id+"F0.wireOp",EDGE,"E3.18.0.3"),sQuery(id+"F0.wireOp",EDGE,"E3.18.0.4"),sQuery(id+"F0.wireOp",EDGE,"E3.18.0.5"),sQuery(id+"F0.wireOp",EDGE,"E3.18.0.6"),sQuery(id+"F0.wireOp",EDGE,"E3.18.0.7"),sQuery(id+"F0.wireOp",EDGE,"E3.18.0.8"),sQuery(id+"F0.wireOp",EDGE,"E3.18.0.9"),sQuery(id+"F0.wireOp",EDGE,"E3.18.0.10"),sQuery(id+"F0.wireOp",EDGE,"E3.18.0.11"),sQuery(id+"F0.wireOp",EDGE,"E3.18.0.12"),sQuery(id+"F0.wireOp",EDGE,"E3.18.0.13"),sQuery(id+"F0.wireOp",EDGE,"E3.18.0.14"),sQuery(id+"F0.wireOp",EDGE,"E3.18.0.15"),sQuery(id+"F0.wireOp",EDGE,"E3.18.0.16"),sQuery(id+"F0.wireOp",EDGE,"E3.18.0.17"),sQuery(id+"F0.wireOp",EDGE,"E3.18.0.18"),sQuery(id+"F0.wireOp",EDGE,"E3.18.0.19"),sQuery(id+"F0.wireOp",EDGE,"E3.18.0.20"),sQuery(id+"F0.wireOp",EDGE,"E3.18.0.21"),sQuery(id+"F0.wireOp",EDGE,"E3.18.0.22"),sQuery(id+"F0.wireOp",EDGE,"E3.18.0.23"),sQuery(id+"F0.wireOp",EDGE,"E3.18.0.24"),sQuery(id+"F0.wireOp",EDGE,"E3.18.0.25"),sQuery(id+"F0.wireOp",EDGE,"E3.18.0.26"),sQuery(id+"F0.wireOp",EDGE,"E3.18.0.27"),sQuery(id+"F0.wireOp",EDGE,"E3.18.0.28"),sQuery(id+"F0.wireOp",EDGE,"E3.18.0.29"),sQuery(id+"F0.wireOp",EDGE,"E3.18.0.30"),sQuery(id+"F0.wireOp",EDGE,"E3.18.0.31"),sQuery(id+"F0.wireOp",EDGE,"E3.18.0.32"),sQuery(id+"F0.wireOp",EDGE,"E3.18.0.33"),sQuery(id+"F0.wireOp",EDGE,"E3.18.0.34"),sQuery(id+"F0.wireOp",EDGE,"E3.18.0.35"),sQuery(id+"F0.wireOp",EDGE,"E3.18.0.36"),sQuery(id+"F0.wireOp",EDGE,"E3.18.0.37"),sQuery(id+"F0.wireOp",EDGE,"E3.18.0.38"),sQuery(id+"F0.wireOp",EDGE,"E3.18.0.39"),sQuery(id+"F0.wireOp",EDGE,"E3.18.0.40"),sQuery(id+"F0.wireOp",EDGE,"E3.18.0.41"),sQuery(id+"F0.wireOp",EDGE,"E3.18.0.42"),sQuery(id+"F0.wireOp",EDGE,"E3.18.0.43"),sQuery(id+"F0.wireOp",EDGE,"E3.18.0.44"),sQuery(id+"F0.wireOp",EDGE,"E3.18.0.45"),sQuery(id+"F0.wireOp",EDGE,"E3.18.0.46"),sQuery(id+"F0.wireOp",EDGE,"E3.18.0.47"),sQuery(id+"F0.wireOp",EDGE,"E3.18.0.48"),sQuery(id+"F0.wireOp",EDGE,"E3.18.0.49"),sQuery(id+"F0.wireOp",EDGE,"E3.18.0.50"),sQuery(id+"F0.wireOp",EDGE,"E3.18.0.51"),sQuery(id+"F0.wireOp",EDGE,"E3.18.0.52"),sQuery(id+"F0.wireOp",EDGE,"E3.18.0.53"),sQuery(id+"F0.wireOp",EDGE,"E3.18.0.54"),sQuery(id+"F0.wireOp",EDGE,"E3.18.0.55"),sQuery(id+"F0.wireOp",EDGE,"E3.18.0.56"),sQuery(id+"F0.wireOp",EDGE,"E3.18.0.57"),sQuery(id+"F0.wireOp",EDGE,"E3.18.0.58"),sQuery(id+"F0.wireOp",EDGE,"E3.18.0.59"),sQuery(id+"F0.wireOp",EDGE,"E3.19.0.0"),sQuery(id+"F0.wireOp",EDGE,"E3.19.0.1"),sQuery(id+"F0.wireOp",EDGE,"E3.19.0.2"),sQuery(id+"F0.wireOp",EDGE,"E3.19.0.3"),sQuery(id+"F0.wireOp",EDGE,"E3.19.0.4"),sQuery(id+"F0.wireOp",EDGE,"E3.19.0.5"),sQuery(id+"F0.wireOp",EDGE,"E3.19.0.6"),sQuery(id+"F0.wireOp",EDGE,"E3.19.0.7"),sQuery(id+"F0.wireOp",EDGE,"E3.19.0.8"),sQuery(id+"F0.wireOp",EDGE,"E3.19.0.9"),sQuery(id+"F0.wireOp",EDGE,"E3.19.0.10"),sQuery(id+"F0.wireOp",EDGE,"E3.19.0.11"),sQuery(id+"F0.wireOp",EDGE,"E3.19.0.12"),sQuery(id+"F0.wireOp",EDGE,"E3.19.0.13"),sQuery(id+"F0.wireOp",EDGE,"E3.19.0.14"),sQuery(id+"F0.wireOp",EDGE,"E3.19.0.15"),sQuery(id+"F0.wireOp",EDGE,"E3.19.0.16"),sQuery(id+"F0.wireOp",EDGE,"E3.19.0.17"),sQuery(id+"F0.wireOp",EDGE,"E3.19.0.18"),sQuery(id+"F0.wireOp",EDGE,"E3.19.0.19"),sQuery(id+"F0.wireOp",EDGE,"E3.19.0.20"),sQuery(id+"F0.wireOp",EDGE,"E3.19.0.21"),sQuery(id+"F0.wireOp",EDGE,"E3.19.0.22"),sQuery(id+"F0.wireOp",EDGE,"E3.19.0.23"),sQuery(id+"F0.wireOp",EDGE,"E3.19.0.24"),sQuery(id+"F0.wireOp",EDGE,"E3.19.0.25"),sQuery(id+"F0.wireOp",EDGE,"E3.19.0.26"),sQuery(id+"F0.wireOp",EDGE,"E3.19.0.27"),sQuery(id+"F0.wireOp",EDGE,"E3.19.0.28"),sQuery(id+"F0.wireOp",EDGE,"E3.19.0.29"),sQuery(id+"F0.wireOp",EDGE,"E3.19.0.30"),sQuery(id+"F0.wireOp",EDGE,"E3.19.0.31"),sQuery(id+"F0.wireOp",EDGE,"E3.19.0.32"),sQuery(id+"F0.wireOp",EDGE,"E3.19.0.33"),sQuery(id+"F0.wireOp",EDGE,"E3.19.0.34"),sQuery(id+"F0.wireOp",EDGE,"E3.19.0.35"),sQuery(id+"F0.wireOp",EDGE,"E3.19.0.36"),sQuery(id+"F0.wireOp",EDGE,"E3.19.0.37"),sQuery(id+"F0.wireOp",EDGE,"E3.19.0.38"),sQuery(id+"F0.wireOp",EDGE,"E3.19.0.39"),sQuery(id+"F0.wireOp",EDGE,"E3.19.0.40"),sQuery(id+"F0.wireOp",EDGE,"E3.19.0.41"),sQuery(id+"F0.wireOp",EDGE,"E3.19.0.42"),sQuery(id+"F0.wireOp",EDGE,"E3.19.0.43"),sQuery(id+"F0.wireOp",EDGE,"E3.19.0.44"),sQuery(id+"F0.wireOp",EDGE,"E3.19.0.45"),sQuery(id+"F0.wireOp",EDGE,"E3.19.0.46"),sQuery(id+"F0.wireOp",EDGE,"E3.19.0.47"),sQuery(id+"F0.wireOp",EDGE,"E3.19.0.48"),sQuery(id+"F0.wireOp",EDGE,"E3.19.0.49"),sQuery(id+"F0.wireOp",EDGE,"E3.19.0.50"),sQuery(id+"F0.wireOp",EDGE,"E3.19.0.51"),sQuery(id+"F0.wireOp",EDGE,"E3.19.0.52"),sQuery(id+"F0.wireOp",EDGE,"E3.19.0.53"),sQuery(id+"F0.wireOp",EDGE,"E3.19.0.54"),sQuery(id+"F0.wireOp",EDGE,"E3.19.0.55"),sQuery(id+"F0.wireOp",EDGE,"E3.19.0.56"),sQuery(id+"F0.wireOp",EDGE,"E3.19.0.57"),sQuery(id+"F0.wireOp",EDGE,"E3.19.0.58"),sQuery(id+"F0.wireOp",EDGE,"E3.19.0.59"),sQuery(id+"F0.wireOp",EDGE,"E3.20.0.0"),sQuery(id+"F0.wireOp",EDGE,"E3.20.0.1"),sQuery(id+"F0.wireOp",EDGE,"E3.20.0.2"),sQuery(id+"F0.wireOp",EDGE,"E3.20.0.3"),sQuery(id+"F0.wireOp",EDGE,"E3.20.0.4"),sQuery(id+"F0.wireOp",EDGE,"E3.20.0.5"),sQuery(id+"F0.wireOp",EDGE,"E3.20.0.6"),sQuery(id+"F0.wireOp",EDGE,"E3.20.0.7"),sQuery(id+"F0.wireOp",EDGE,"E3.20.0.8"),sQuery(id+"F0.wireOp",EDGE,"E3.20.0.9"),sQuery(id+"F0.wireOp",EDGE,"E3.20.0.10"),sQuery(id+"F0.wireOp",EDGE,"E3.20.0.11"),sQuery(id+"F0.wireOp",EDGE,"E3.20.0.12"),sQuery(id+"F0.wireOp",EDGE,"E3.20.0.13"),sQuery(id+"F0.wireOp",EDGE,"E3.20.0.14"),sQuery(id+"F0.wireOp",EDGE,"E3.20.0.15"),sQuery(id+"F0.wireOp",EDGE,"E3.20.0.16"),sQuery(id+"F0.wireOp",EDGE,"E3.20.0.17"),sQuery(id+"F0.wireOp",EDGE,"E3.20.0.18"),sQuery(id+"F0.wireOp",EDGE,"E3.20.0.19"),sQuery(id+"F0.wireOp",EDGE,"E3.20.0.20"),sQuery(id+"F0.wireOp",EDGE,"E3.20.0.21"),sQuery(id+"F0.wireOp",EDGE,"E3.20.0.22"),sQuery(id+"F0.wireOp",EDGE,"E3.20.0.23"),sQuery(id+"F0.wireOp",EDGE,"E3.20.0.24"),sQuery(id+"F0.wireOp",EDGE,"E3.20.0.25"),sQuery(id+"F0.wireOp",EDGE,"E3.20.0.26"),sQuery(id+"F0.wireOp",EDGE,"E3.20.0.27"),sQuery(id+"F0.wireOp",EDGE,"E3.20.0.28"),sQuery(id+"F0.wireOp",EDGE,"E3.20.0.29"),sQuery(id+"F0.wireOp",EDGE,"E3.20.0.30"),sQuery(id+"F0.wireOp",EDGE,"E3.20.0.31"),sQuery(id+"F0.wireOp",EDGE,"E3.20.0.32"),sQuery(id+"F0.wireOp",EDGE,"E3.20.0.33"),sQuery(id+"F0.wireOp",EDGE,"E3.20.0.34"),sQuery(id+"F0.wireOp",EDGE,"E3.20.0.35"),sQuery(id+"F0.wireOp",EDGE,"E3.20.0.36"),sQuery(id+"F0.wireOp",EDGE,"E3.20.0.37"),sQuery(id+"F0.wireOp",EDGE,"E3.20.0.38"),sQuery(id+"F0.wireOp",EDGE,"E3.20.0.39"),sQuery(id+"F0.wireOp",EDGE,"E3.20.0.40"),sQuery(id+"F0.wireOp",EDGE,"E3.20.0.41"),sQuery(id+"F0.wireOp",EDGE,"E3.20.0.42"),sQuery(id+"F0.wireOp",EDGE,"E3.20.0.43"),sQuery(id+"F0.wireOp",EDGE,"E3.20.0.44"),sQuery(id+"F0.wireOp",EDGE,"E3.20.0.45"),sQuery(id+"F0.wireOp",EDGE,"E3.20.0.46"),sQuery(id+"F0.wireOp",EDGE,"E3.20.0.47"),sQuery(id+"F0.wireOp",EDGE,"E3.20.0.48"),sQuery(id+"F0.wireOp",EDGE,"E3.20.0.49"),sQuery(id+"F0.wireOp",EDGE,"E3.20.0.50"),sQuery(id+"F0.wireOp",EDGE,"E3.20.0.51"),sQuery(id+"F0.wireOp",EDGE,"E3.20.0.52"),sQuery(id+"F0.wireOp",EDGE,"E3.20.0.53"),sQuery(id+"F0.wireOp",EDGE,"E3.20.0.54"),sQuery(id+"F0.wireOp",EDGE,"E3.20.0.55"),sQuery(id+"F0.wireOp",EDGE,"E3.20.0.56"),sQuery(id+"F0.wireOp",EDGE,"E3.20.0.57"),sQuery(id+"F0.wireOp",EDGE,"E3.20.0.58"),sQuery(id+"F0.wireOp",EDGE,"E3.20.0.59")])],"isStart":false});
            var sketch = newSketch(context, id + "F2", { "sketchPlane" : qUnion([Q0])});
            skLineSegment(sketch, "E4.bottom", {"start": v(-53.7, 38.7) * mm, "end": v(53.7, 38.7) * mm});
            skLineSegment(sketch, "E4.top", {"start": v(-53.7, -38.7) * mm, "end": v(53.7, -38.7) * mm});
            skLineSegment(sketch, "E4.left", {"start": v(-53.7, 38.7) * mm, "end": v(-53.7, -38.7) * mm});
            skLineSegment(sketch, "E4.right", {"start": v(53.7, 38.7) * mm, "end": v(53.7, -38.7) * mm});
            skSolve(sketch);
        }
        {
            var Q0;
            Q0=makeQuery(id+"F2.imprint","IMPRINT",FACE,{"disambiguationData":[TD([[makeQuery(id+"F2.imprint","IMPRINT",EDGE,{"derivedFrom":sQuery(id+"F2.wireOp",EDGE,"E4.bottom")}),1.0]])]});
            extrude(context, id + "F3", {"entities" : qUnion([Q0]), "operationType" : NewBodyOperationType.ADD, "depth" : 5 * mm, "offsetDistance" : 25 * mm});
        }
    });
